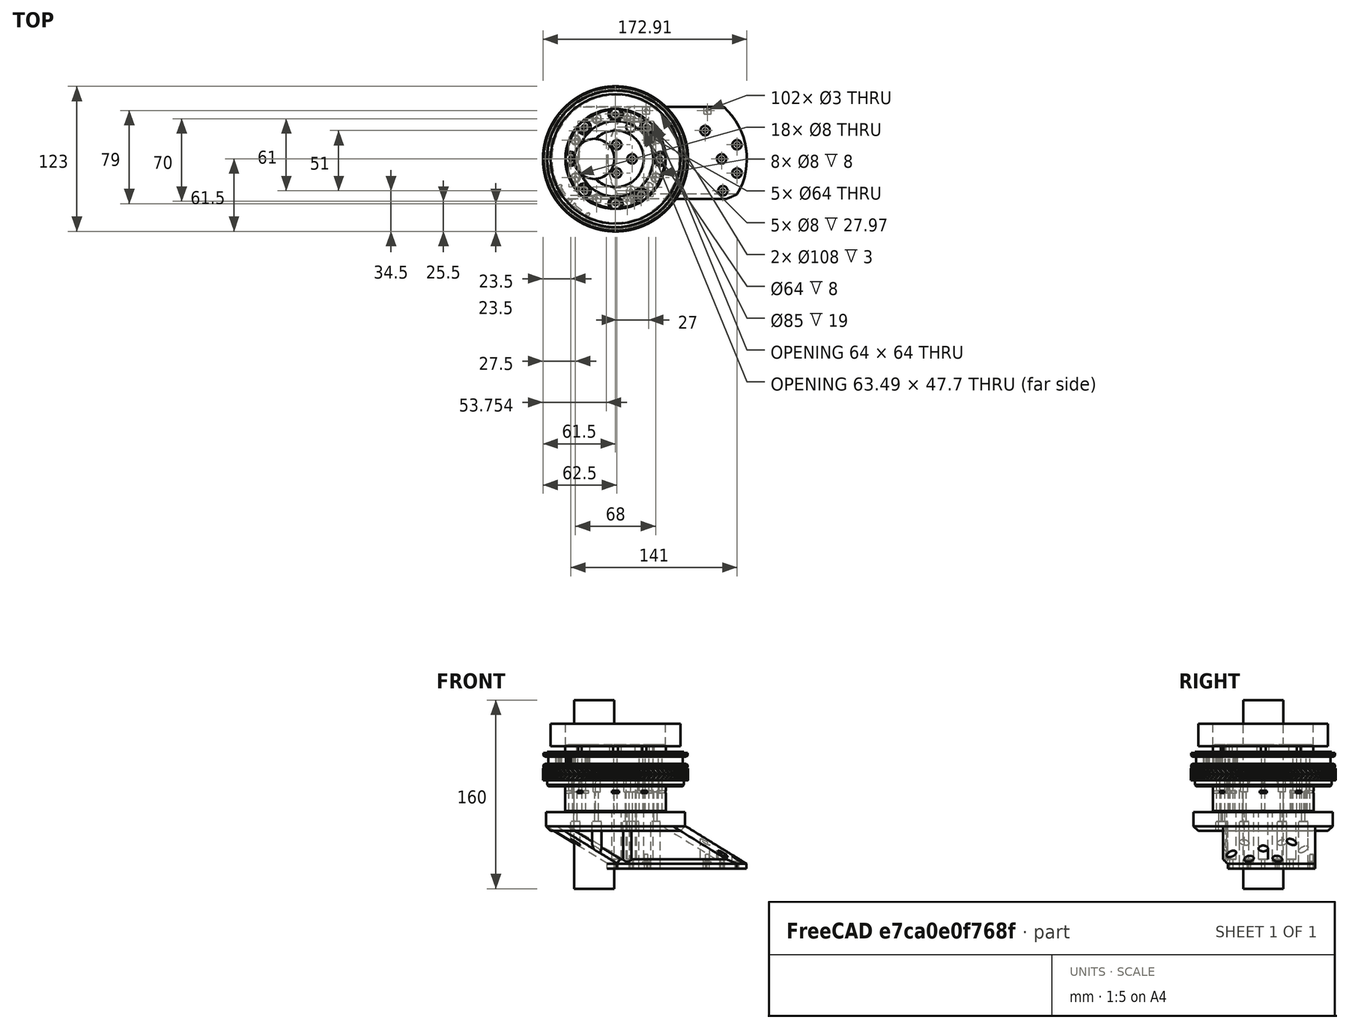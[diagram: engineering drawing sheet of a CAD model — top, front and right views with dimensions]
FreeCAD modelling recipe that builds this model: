
FCSTD DOCUMENT  (FreeCAD 0.19R24276 (Git))
Label: Base_inner-barrel_034
License: All rights reserved
LicenseURL: http://en.wikipedia.org/wiki/All_rights_reserved
objects: Part::Cylinder×576, Part::Box×255, Part::Compound×174, Part::Cut×167, Part::FeaturePython×49, Part::Chamfer×31, Part::Mirroring×10, Part::Fillet×9, Part::Common×3, Part::Torus×2, Mesh::Feature×2, Sketcher::SketchObject×1, Part::Extrusion×1
note: 1278 computed .brp shape members not serialized (recipe doc carries the construction recipe); baked Part::Feature solids carry a one-line shape summary decoded from their .brp

FEATURE [Part::Cylinder] Cylinder288  label="Válec288"
  Angle = 360
  AttacherType = Attacher::AttachEngine3D
  Height = 20
  Placement = pos=(0,-64.5,4.5) rot=(0,0,1;0rad)
  Radius = 3.5
FEATURE [Part::Cylinder] Cylinder371  label="Válec371"
  Angle = 360
  AttacherType = Attacher::AttachEngine3D
  Height = 50
  Placement = pos=(34,36,0) rot=(0,0,1;0rad)
  Radius = 1.5
FEATURE [Part::Cylinder] Cylinder372  label="Válec372"
  Angle = 360
  AttacherType = Attacher::AttachEngine3D
  Height = 50
  Placement = pos=(-34,-36,0) rot=(0,0,1;0rad)
  Radius = 1.5
FEATURE [Part::Torus] Torus  label="Anuloid"
  Angle1 = -180
  Angle2 = 180
  Angle3 = 360
  AttacherType = Attacher::AttachEngine3D
  Placement = pos=(0,0,24.5) rot=(0,0,1;0rad)
  Radius1 = 64.2
  Radius2 = 3.1
FEATURE [Part::FeaturePython] Tube019  # WARN: FeaturePython — macro-defined, semantics opaque (R4)
  AttacherType = Attacher::AttachEngine3D
  Height = 13
  InnerRadius = 38
  OuterRadius = 64
  Placement = pos=(0,0,18) rot=(0,0,1;0rad)
FEATURE [Part::Cut] Cut129
  Base = -> Tube019
  Tool = -> Torus
FEATURE [Part::Cut] Cut130
  Base = -> Cut129
  Tool = -> Cylinder288
FEATURE [Part::FeaturePython] Tube020  # WARN: FeaturePython — macro-defined, semantics opaque (R4)
  AttacherType = Attacher::AttachEngine3D
  Height = 1
  InnerRadius = 38
  OuterRadius = 58
  Placement = pos=(0,0,31) rot=(0,0,1;0rad)
FEATURE [Part::Box] Box149  label="Krychle149"
  AttacherType = Attacher::AttachEngine3D
  Height = 10
  Length = 6
  Placement = pos=(-37,33,40) rot=(0,0,1;0rad)
  Width = 6
FEATURE [Part::Cylinder] Cylinder378  label="Válec378"
  Angle = 360
  AttacherType = Attacher::AttachEngine3D
  Height = 50
  Placement = pos=(-51,6,0) rot=(0,0,1;0rad)
  Radius = 1.5
FEATURE [Part::Cylinder] Cylinder370  label="Válec370"
  Angle = 360
  AttacherType = Attacher::AttachEngine3D
  Height = 50
  Placement = pos=(-34,36,0) rot=(0,0,1;0rad)
  Radius = 1.5
FEATURE [Part::Cylinder] Cylinder373  label="Válec373"
  Angle = 360
  AttacherType = Attacher::AttachEngine3D
  Height = 50
  Placement = pos=(34,-36,0) rot=(0,0,1;0rad)
  Radius = 1.5
FEATURE [Part::Box] Box150  label="Krychle150"
  AttacherType = Attacher::AttachEngine3D
  Height = 10
  Length = 6
  Placement = pos=(31,-39,40) rot=(0,0,1;0rad)
  Width = 6
FEATURE [Part::Cylinder] Cylinder379  label="Válec379"
  Angle = 360
  AttacherType = Attacher::AttachEngine3D
  Height = 100
  Placement = pos=(51,-12,0) rot=(0,0,1;0rad)
  Radius = 1.5
FEATURE [Part::Cylinder] Cylinder377  label="Válec377"
  Angle = 360
  AttacherType = Attacher::AttachEngine3D
  Height = 50
  Placement = pos=(51,6,0) rot=(0,0,1;0rad)
  Radius = 1.5
FEATURE [Part::Cylinder] Cylinder375  label="Válec375"
  Angle = 360
  AttacherType = Attacher::AttachEngine3D
  Height = 50
  Placement = pos=(0,-50,0) rot=(0,0,1;0rad)
  Radius = 1.5
FEATURE [Part::Cylinder] Cylinder409  label="Válec409"
  Angle = 360
  AttacherType = Attacher::AttachEngine3D
  Height = 7
  Placement = pos=(51,6,50) rot=(0,0,1;0rad)
  Radius = 3
FEATURE [Part::Cylinder] Cylinder411  label="Válec411"
  Angle = 360
  AttacherType = Attacher::AttachEngine3D
  Height = 7
  Placement = pos=(51,-12,50) rot=(0,0,1;0rad)
  Radius = 3
FEATURE [Part::Cylinder] Cylinder406  label="Válec406"
  Angle = 360
  AttacherType = Attacher::AttachEngine3D
  Height = 7
  Placement = pos=(-51,-12,50) rot=(0,0,1;0rad)
  Radius = 3
FEATURE [Part::Cylinder] Cylinder405  label="Válec405"
  Angle = 360
  AttacherType = Attacher::AttachEngine3D
  Height = 7
  Placement = pos=(51,6,50) rot=(0,0,1;0rad)
  Radius = 3
FEATURE [Part::Cylinder] Cylinder404  label="Válec404"
  Angle = 360
  AttacherType = Attacher::AttachEngine3D
  Height = 7
  Placement = pos=(-51,6,50) rot=(0,0,1;0rad)
  Radius = 3
FEATURE [Part::Cylinder] Cylinder374  label="Válec374"
  Angle = 360
  AttacherType = Attacher::AttachEngine3D
  Height = 50
  Placement = pos=(0,50,0) rot=(0,0,1;0rad)
  Radius = 1.5
FEATURE [Part::Cylinder] Cylinder376  label="Válec376"
  Angle = 360
  AttacherType = Attacher::AttachEngine3D
  Height = 100
  Placement = pos=(-51,-12,0) rot=(0,0,1;0rad)
  Radius = 1.5
FEATURE [Part::Compound] Compound308
  Links = -> [Cylinder370,Cylinder371,Cylinder372,Cylinder373,Cylinder374,Cylinder375,Cylinder376,Cylinder377,Cylinder378,Cylinder379]
FEATURE [Part::Cut] Cut160
  Base = -> Cut130
  Tool = -> Compound308
FEATURE [Part::Cylinder] Cylinder408  label="Válec408"
  Angle = 360
  AttacherType = Attacher::AttachEngine3D
  Height = 7
  Placement = pos=(-51,-12,50) rot=(0,0,1;0rad)
  Radius = 3
FEATURE [Part::Box] Box153  label="Krychle153"
  AttacherType = Attacher::AttachEngine3D
  Height = 10
  Length = 6
  Placement = pos=(-37,33,40) rot=(0,0,1;0rad)
  Width = 6
FEATURE [Part::Box] Box154  label="Krychle154"
  AttacherType = Attacher::AttachEngine3D
  Height = 10
  Length = 6
  Placement = pos=(-37,-39,40) rot=(0,0,1;0rad)
  Width = 6
FEATURE [Part::Box] Box155  label="Krychle155"
  AttacherType = Attacher::AttachEngine3D
  Height = 10
  Length = 6
  Placement = pos=(31,33,40) rot=(0,0,1;0rad)
  Width = 6
FEATURE [Part::Cylinder] Cylinder410  label="Válec410"
  Angle = 360
  AttacherType = Attacher::AttachEngine3D
  Height = 7
  Placement = pos=(-51,6,50) rot=(0,0,1;0rad)
  Radius = 3
FEATURE [Part::Compound] Compound313
  Links = -> [Cylinder408,Cylinder411,Cylinder409,Cylinder410]
  Placement = pos=(0,0,-25) rot=(0,0,1;0rad)
FEATURE [Part::Cut] Cut162
  Base = -> Cut160
  Tool = -> Compound313
FEATURE [Part::Box] Box158  label="Krychle158"
  AttacherType = Attacher::AttachEngine3D
  Height = 2
  Length = 6
  Placement = pos=(43.284,-12.6687,25) rot=(0,0,1;1.35263rad)
  Width = 8
FEATURE [Part::Box] Box145  label="Krychle145"
  AttacherType = Attacher::AttachEngine3D
  Height = 10
  Length = 6
  Placement = pos=(-3,47,40) rot=(0,0,1;0rad)
  Width = 6
FEATURE [Part::Box] Box151  label="Krychle151"
  AttacherType = Attacher::AttachEngine3D
  Height = 10
  Length = 6
  Placement = pos=(-3,-53,40) rot=(0,0,1;0rad)
  Width = 6
FEATURE [Part::Box] Box159  label="Krychle159"
  AttacherType = Attacher::AttachEngine3D
  Height = 2
  Length = 6
  Placement = pos=(42.7226,14.4491,25) rot=(0,0,1;1.96349rad)
  Width = 8
FEATURE [Part::Box] Box146  label="Krychle146"
  AttacherType = Attacher::AttachEngine3D
  Height = 10
  Length = 6
  Placement = pos=(-3,-53,40) rot=(0,0,1;0rad)
  Width = 6
FEATURE [Part::Box] Box148  label="Krychle148"
  AttacherType = Attacher::AttachEngine3D
  Height = 10
  Length = 6
  Placement = pos=(31,33,40) rot=(0,0,1;0rad)
  Width = 6
FEATURE [Part::Box] Box157  label="Krychle157"
  AttacherType = Attacher::AttachEngine3D
  Height = 2
  Length = 6
  Placement = pos=(14.4491,-42.7226,25) rot=(0,0,1;0.392699rad)
  Width = 8
FEATURE [Part::Box] Box162  label="Krychle162"
  AttacherType = Attacher::AttachEngine3D
  Height = 2
  Length = 6
  Placement = pos=(-40.4265,19.9924,25) rot=(0,0,-1;1.96349rad)
  Width = 8
FEATURE [Part::Box] Box147  label="Krychle147"
  AttacherType = Attacher::AttachEngine3D
  Height = 10
  Length = 6
  Placement = pos=(-37,-39,40) rot=(0,0,1;0rad)
  Width = 6
FEATURE [Part::Compound] Compound315
  Links = -> [Box145,Box147,Box146,Box148,Box149,Box150]
  Placement = pos=(0,0,-18) rot=(0,0,1;0rad)
FEATURE [Part::Cylinder] Cylinder407  label="Válec407"
  Angle = 360
  AttacherType = Attacher::AttachEngine3D
  Height = 7
  Placement = pos=(51,-12,50) rot=(0,0,1;0rad)
  Radius = 3
FEATURE [Part::Compound] Compound312
  Links = -> [Cylinder406,Cylinder407,Cylinder405,Cylinder404]
  Placement = pos=(0,0,-25) rot=(0,0,1;0rad)
FEATURE [Part::Cut] Cut161
  Base = -> Tube020
  Tool = -> Compound312
FEATURE [Part::Box] Box156  label="Krychle156"
  AttacherType = Attacher::AttachEngine3D
  Height = 10
  Length = 6
  Placement = pos=(31,-39,40) rot=(0,0,1;0rad)
  Width = 6
FEATURE [Part::Box] Box152  label="Krychle152"
  AttacherType = Attacher::AttachEngine3D
  Height = 10
  Length = 6
  Placement = pos=(-3,47,40) rot=(0,0,1;0rad)
  Width = 6
FEATURE [Part::Compound] Compound316
  Links = -> [Box152,Box154,Box151,Box155,Box153,Box156]
  Placement = pos=(0,0,-18) rot=(0,0,1;0rad)
FEATURE [Part::Cut] Cut163
  Base = -> Cut161
  Tool = -> Compound316
FEATURE [Part::Cut] Cut164
  Base = -> Cut162
  Tool = -> Compound315
FEATURE [Part::Box] Box160  label="Krychle160"
  AttacherType = Attacher::AttachEngine3D
  Height = 2
  Length = 6
  Placement = pos=(19.9924,40.4265,25) rot=(0,0,1;2.74889rad)
  Width = 8
FEATURE [Part::Box] Box163  label="Krychle163"
  AttacherType = Attacher::AttachEngine3D
  Height = 2
  Length = 6
  Placement = pos=(-44.5826,-6.81089,25) rot=(0,0,-1;1.35263rad)
  Width = 8
FEATURE [Part::Cylinder] Cylinder444  label="Válec444"
  Angle = 360
  AttacherType = Attacher::AttachEngine3D
  Height = 100
  Placement = pos=(16.0727,-38.8029,0) rot=(0,0,1;0.785398rad)
  Radius = 1.5
FEATURE [Part::Cylinder] Cylinder445  label="Válec445"
  Angle = 360
  AttacherType = Attacher::AttachEngine3D
  Height = 100
  Placement = pos=(41.0044,-9.09046,0) rot=(0,0,1;1.74533rad)
  Radius = 1.5
FEATURE [Part::Cylinder] Cylinder446  label="Válec446"
  Angle = 360
  AttacherType = Attacher::AttachEngine3D
  Height = 100
  Placement = pos=(38.8029,16.0727,0) rot=(0,0,1;2.35619rad)
  Radius = 1.5
FEATURE [Part::Box] Box164  label="Krychle164"
  AttacherType = Attacher::AttachEngine3D
  Height = 2
  Length = 6
  Placement = pos=(-19.9924,-40.4265,25) rot=(0,0,-1;0.392699rad)
  Width = 8
FEATURE [Part::Cylinder] Cylinder447  label="Válec447"
  Angle = 360
  AttacherType = Attacher::AttachEngine3D
  Height = 100
  Placement = pos=(16.0727,38.8029,0) rot=(0,0,1;3.14159rad)
  Radius = 1.5
FEATURE [Part::Cylinder] Cylinder449  label="Válec449"
  Angle = 360
  AttacherType = Attacher::AttachEngine3D
  Height = 100
  Placement = pos=(-38.8029,16.0727,0) rot=(0,0,-1;1.5708rad)
  Radius = 1.5
FEATURE [Part::Cylinder] Cylinder450  label="Válec450"
  Angle = 360
  AttacherType = Attacher::AttachEngine3D
  Height = 100
  Placement = pos=(-41.0044,-9.09046,0) rot=(0,0,-1;0.959931rad)
  Radius = 1.5
FEATURE [Part::Cylinder] Cylinder471  label="Válec471"
  Angle = 360
  AttacherType = Attacher::AttachEngine3D
  Height = 100
  Placement = pos=(16.0727,38.8029,0) rot=(0,0,1;3.14159rad)
  Radius = 1.5
FEATURE [Part::Cylinder] Cylinder468  label="Válec468"
  Angle = 360
  AttacherType = Attacher::AttachEngine3D
  Height = 100
  Placement = pos=(16.0727,-38.8029,0) rot=(0,0,1;0.785398rad)
  Radius = 1.5
FEATURE [Part::Cylinder] Cylinder473  label="Válec473"
  Angle = 360
  AttacherType = Attacher::AttachEngine3D
  Height = 100
  Placement = pos=(-38.8029,16.0727,0) rot=(0,0,-1;1.5708rad)
  Radius = 1.5
FEATURE [Part::Cylinder] Cylinder474  label="Válec474"
  Angle = 360
  AttacherType = Attacher::AttachEngine3D
  Height = 100
  Placement = pos=(-41.0044,-9.09046,0) rot=(0,0,-1;0.959931rad)
  Radius = 1.5
FEATURE [Part::Cylinder] Cylinder448  label="Válec448"
  Angle = 360
  AttacherType = Attacher::AttachEngine3D
  Height = 100
  Placement = pos=(-16.0727,38.8029,0) rot=(0,0,1;3.92699rad)
  Radius = 1.5
FEATURE [Part::Cylinder] Cylinder451  label="Válec451"
  Angle = 360
  AttacherType = Attacher::AttachEngine3D
  Height = 100
  Placement = pos=(-16.0727,-38.8029,0) rot=(0,0,1;0rad)
  Radius = 1.5
FEATURE [Part::Compound] Compound325
  Links = -> [Cylinder444,Cylinder445,Cylinder446,Cylinder447,Cylinder448,Cylinder449,Cylinder450,Cylinder451]
FEATURE [Part::Cut] Cut173
  Base = -> Cut163
  Tool = -> Compound325
FEATURE [Part::Box] Box161  label="Krychle161"
  AttacherType = Attacher::AttachEngine3D
  Height = 2
  Length = 6
  Placement = pos=(-14.4491,42.7226,25) rot=(0,0,1;3.53429rad)
  Width = 8
FEATURE [Part::Compound] Compound322
  Links = -> [Box157,Box158,Box159,Box160,Box161,Box162,Box163,Box164]
FEATURE [Part::Cylinder] Cylinder469  label="Válec469"
  Angle = 360
  AttacherType = Attacher::AttachEngine3D
  Height = 100
  Placement = pos=(41.0044,-9.09046,0) rot=(0,0,1;1.74533rad)
  Radius = 1.5
FEATURE [Part::Cylinder] Cylinder529  label="Válec529"
  Angle = 360
  AttacherType = Attacher::AttachEngine3D
  Height = 100
  Placement = pos=(39,-21,0) rot=(0,0,1;0rad)
  Radius = 1.5
FEATURE [Part::Cylinder] Cylinder470  label="Válec470"
  Angle = 360
  AttacherType = Attacher::AttachEngine3D
  Height = 100
  Placement = pos=(38.8029,16.0727,0) rot=(0,0,1;2.35619rad)
  Radius = 1.5
FEATURE [Part::Cylinder] Cylinder472  label="Válec472"
  Angle = 360
  AttacherType = Attacher::AttachEngine3D
  Height = 100
  Placement = pos=(-16.0727,38.8029,0) rot=(0,0,1;3.92699rad)
  Radius = 1.5
FEATURE [Part::Cylinder] Cylinder475  label="Válec475"
  Angle = 360
  AttacherType = Attacher::AttachEngine3D
  Height = 100
  Placement = pos=(-16.0727,-38.8029,0) rot=(0,0,1;0rad)
  Radius = 1.5
FEATURE [Part::Compound] Compound328
  Links = -> [Cylinder468,Cylinder469,Cylinder470,Cylinder471,Cylinder472,Cylinder473,Cylinder474,Cylinder475]
  Placement = pos=(0,0,20) rot=(0,0,1;0rad)
FEATURE [Part::Cut] Cut174
  Base = -> Cut164
  Tool = -> Compound328
FEATURE [Part::Cut] Cut175
  Base = -> Cut174
  Tool = -> Compound322
FEATURE [Part::Cylinder] Cylinder533  label="Válec533"
  Angle = 360
  AttacherType = Attacher::AttachEngine3D
  Height = 7
  Placement = pos=(39,-21,50) rot=(0,0,1;0rad)
  Radius = 3
FEATURE [Part::Cylinder] Cylinder528  label="Válec528"
  Angle = 360
  AttacherType = Attacher::AttachEngine3D
  Height = 100
  Placement = pos=(-39,-21,0) rot=(0,0,1;0rad)
  Radius = 1.5
FEATURE [Part::Cylinder] Cylinder532  label="Válec532"
  Angle = 360
  AttacherType = Attacher::AttachEngine3D
  Height = 7
  Placement = pos=(-39,-21,50) rot=(0,0,1;0rad)
  Radius = 3
FEATURE [Part::Cylinder] Cylinder530  label="Válec530"
  Angle = 360
  AttacherType = Attacher::AttachEngine3D
  Height = 7
  Placement = pos=(-39,-21,50) rot=(0,0,1;0rad)
  Radius = 3
FEATURE [Part::Cylinder] Cylinder531  label="Válec531"
  Angle = 360
  AttacherType = Attacher::AttachEngine3D
  Height = 7
  Placement = pos=(39,-21,50) rot=(0,0,1;0rad)
  Radius = 3
FEATURE [Part::Compound] Compound
  Links = -> [Cylinder528,Cylinder529]
FEATURE [Part::Compound] Compound337
  Links = -> [Cylinder530,Cylinder531]
  Placement = pos=(0,0,-25) rot=(0,0,1;0rad)
FEATURE [Part::Cut] Cut
  Base = -> Cut173
  Tool = -> Compound337
FEATURE [Part::Compound] Compound338
  Links = -> [Cylinder532,Cylinder533]
  Placement = pos=(0,0,-25) rot=(0,0,1;0rad)
FEATURE [Part::Cut] Cut176
  Base = -> Cut175
  Tool = -> Compound338
FEATURE [Part::Cut] Cut177
  Base = -> Cut176
  Tool = -> Compound
FEATURE [Part::Compound] Compound339  label="bazovina-part-C_loziskovina"
  Links = -> [Cut,Cut177]
FEATURE [Part::Cylinder] Cylinder476  label="Válec476"
  Angle = 360
  AttacherType = Attacher::AttachEngine3D
  Height = 20
  Placement = pos=(0,-63.8,4.5) rot=(0,0,1;0rad)
  Radius = 3.5
FEATURE [Part::Box] Box176  label="Krychle176"
  AttacherType = Attacher::AttachEngine3D
  Height = 15
  Length = 148
  Placement = pos=(-74,0,16) rot=(0,0,1;0rad)
  Width = 48
FEATURE [Part::Cylinder] Cylinder482  label="Válec482"
  Angle = 360
  AttacherType = Attacher::AttachEngine3D
  Height = 15
  Placement = pos=(0,0,16) rot=(0,0,1;0rad)
  Radius = 74
FEATURE [Part::FeaturePython] Tube024  # WARN: FeaturePython — macro-defined, semantics opaque (R4)
  AttacherType = Attacher::AttachEngine3D
  Height = 15
  InnerRadius = 64.5
  OuterRadius = 74
  Placement = pos=(0,0,16) rot=(0,0,1;0rad)
FEATURE [Part::Torus] Torus001  label="Anuloid001"
  Angle1 = -180
  Angle2 = 180
  Angle3 = 360
  AttacherType = Attacher::AttachEngine3D
  Placement = pos=(0,0,24.5) rot=(0,0,1;0rad)
  Radius1 = 64.2
  Radius2 = 3.1
FEATURE [Part::Cut] Cut178
  Base = -> Tube024
  Tool = -> Torus001
FEATURE [Part::Cut] Cut179
  Base = -> Cut178
  Tool = -> Cylinder476
FEATURE [Part::Cut] Cut185
  Base = -> Box176
  Tool = -> Cylinder482
FEATURE [Part::Cylinder] Cylinder485  label="Válec485"
  Angle = 360
  AttacherType = Attacher::AttachEngine3D
  Height = 15
  Placement = pos=(0,0,16) rot=(0,0,1;0rad)
  Radius = 74
FEATURE [Part::Cut] Cut188
  Base = -> Cut185
  Tool = -> Cylinder485
FEATURE [Part::Compound] Compound341
  Links = -> [Cut188,Cut179]
FEATURE [Part::Cylinder] Cylinder509  label="Válec509"
  Angle = 360
  AttacherType = Attacher::AttachEngine3D
  Height = 50
  Placement = pos=(71,80,24) rot=(1,0,0;1.5708rad)
  Radius = 1.5
FEATURE [Part::Box] Box208  label="Krychle208"
  AttacherType = Attacher::AttachEngine3D
  Height = 6
  Length = 8
  Placement = pos=(67,38,21) rot=(0,0,1;0rad)
  Width = 2
FEATURE [Part::Cylinder] Cylinder510  label="Válec510"
  Angle = 360
  AttacherType = Attacher::AttachEngine3D
  Height = 50
  Placement = pos=(-71,80,24) rot=(1,0,0;1.5708rad)
  Radius = 1.5
FEATURE [Part::Compound] Compound342
  Links = -> [Cylinder509,Cylinder510]
FEATURE [Part::Box] Box209  label="Krychle209"
  AttacherType = Attacher::AttachEngine3D
  Height = 6
  Length = 8
  Placement = pos=(-75,38,21) rot=(0,0,1;0rad)
  Width = 2
FEATURE [Part::Compound] Compound340
  Links = -> [Box208,Box209]
FEATURE [Part::Cut] Cut201
  Base = -> Compound341
  Tool = -> Compound340
FEATURE [Part::Cut] Cut202
  Base = -> Cut201
  Tool = -> Compound342
FEATURE [Part::Box] Box179  label="Krychle179"
  AttacherType = Attacher::AttachEngine3D
  Height = 47
  Length = 56
  Placement = pos=(-28,0,29) rot=(0,0,1;0rad)
  Width = 200
FEATURE [Part::Cut] Cut203
  Base = -> Cut202
  Tool = -> Box179
FEATURE [Part::Cylinder] Cylinder982  label="Válec982"
  Angle = 360
  AttacherType = Attacher::AttachEngine3D
  Height = 60
  Placement = pos=(-71,2.7e-14,0) rot=(0,0,-1;1.5708rad)
  Radius = 1.5
FEATURE [Part::Cylinder] Cylinder978  label="Válec978"
  Angle = 360
  AttacherType = Attacher::AttachEngine3D
  Height = 60
  Placement = pos=(35.5,61.4878,0) rot=(0,0,1;2.61799rad)
  Radius = 1.5
FEATURE [Part::Cylinder] Cylinder983  label="Válec983"
  Angle = 360
  AttacherType = Attacher::AttachEngine3D
  Height = 60
  Placement = pos=(-61.4878,-35.5,0) rot=(0,0,-1;1.0472rad)
  Radius = 1.5
FEATURE [Part::Cylinder] Cylinder977  label="Válec977"
  Angle = 360
  AttacherType = Attacher::AttachEngine3D
  Height = 60
  Placement = pos=(61.4878,35.5,0) rot=(0,0,1;2.0944rad)
  Radius = 1.5
FEATURE [Part::Cylinder] Cylinder984  label="Válec984"
  Angle = 360
  AttacherType = Attacher::AttachEngine3D
  Height = 60
  Placement = pos=(-35.5,-61.4878,0) rot=(0,0,-1;0.523599rad)
  Radius = 1.5
FEATURE [Part::Cylinder] Cylinder974  label="Válec974"
  Angle = 360
  AttacherType = Attacher::AttachEngine3D
  Height = 60
  Placement = pos=(35.5,-61.4878,0) rot=(0,0,1;0.523599rad)
  Radius = 1.5
FEATURE [Part::Cylinder] Cylinder976  label="Válec976"
  Angle = 360
  AttacherType = Attacher::AttachEngine3D
  Height = 60
  Placement = pos=(71,-1.8e-14,0) rot=(0,0,1;1.5708rad)
  Radius = 1.5
FEATURE [Part::Cylinder] Cylinder973  label="Válec973"
  Angle = 360
  AttacherType = Attacher::AttachEngine3D
  Height = 60
  Placement = pos=(0,-71,0) rot=(0,0,1;0rad)
  Radius = 1.5
FEATURE [Part::Cylinder] Cylinder980  label="Válec980"
  Angle = 360
  AttacherType = Attacher::AttachEngine3D
  Height = 60
  Placement = pos=(-35.5,61.4878,0) rot=(0,0,1;3.66519rad)
  Radius = 1.5
FEATURE [Part::Cylinder] Cylinder981  label="Válec981"
  Angle = 360
  AttacherType = Attacher::AttachEngine3D
  Height = 60
  Placement = pos=(-61.4878,35.5,0) rot=(0,0,1;4.18879rad)
  Radius = 1.5
FEATURE [Part::Cylinder] Cylinder975  label="Válec975"
  Angle = 360
  AttacherType = Attacher::AttachEngine3D
  Height = 60
  Placement = pos=(61.4878,-35.5,0) rot=(0,0,1;1.0472rad)
  Radius = 1.5
FEATURE [Part::Compound] Compound525
  Links = -> [Cylinder973,Cylinder974,Cylinder975,Cylinder976,Cylinder977,Cylinder978,Cylinder980,Cylinder981,Cylinder982,Cylinder983,Cylinder984]
FEATURE [Part::Cut] Cut204  label="bazovina_part-E_lozo-okruh-novo"
  Base = -> Cut203
  Tool = -> Compound525
FEATURE [Part::FeaturePython] wormgear022  # WARN: FeaturePython — macro-defined, semantics opaque (R4)
  AttacherType = Attacher::AttachEngine3D
  Placement = pos=(0,0,100) rot=(0,0,1;0rad)
  beta = 33.6901
  clearance = 0.25
  diameter = 120
  head = 0
  height = 5
  module = 1
  pressure_angle = 20
  reverse_pitch = true
  teeth = 80
  version = 0.0.3
FEATURE [Part::FeaturePython] wormgear023  # WARN: FeaturePython — macro-defined, semantics opaque (R4)
  AttacherType = Attacher::AttachEngine3D
  Placement = pos=(0,0,95) rot=(0,0,1;0.032289rad)
  beta = 33.6901
  clearance = 0.25
  diameter = 120
  head = 0
  height = 5
  module = 1
  pressure_angle = 20
  reverse_pitch = false
  teeth = 80
  version = 0.0.3
FEATURE [Part::Cylinder] Cylinder289  label="Válec289"
  Angle = 360
  AttacherType = Attacher::AttachEngine3D
  Height = 20
  Placement = pos=(0,0,91) rot=(0,0,1;0rad)
  Radius = 38
FEATURE [Part::Cylinder] Cylinder290  label="Válec290"
  Angle = 360
  AttacherType = Attacher::AttachEngine3D
  Height = 20
  Placement = pos=(0,0,91) rot=(0,0,1;0rad)
  Radius = 38
FEATURE [Part::Cylinder] Cylinder461  label="Válec461"
  Angle = 360
  AttacherType = Attacher::AttachEngine3D
  Height = 100
  Placement = pos=(38.8029,-16.0727,0) rot=(0,0,1;1.5708rad)
  Radius = 1.5
FEATURE [Part::Cut] Cut128
  Base = -> wormgear022
  Placement = pos=(0,0,-63) rot=(0,0,1;0rad)
  Tool = -> Cylinder289
FEATURE [Part::Cut] Cut127
  Base = -> wormgear023
  Placement = pos=(0,0,-63) rot=(0,0,1;0rad)
  Tool = -> Cylinder290
FEATURE [Part::Cylinder] Cylinder452  label="Válec452"
  Angle = 360
  AttacherType = Attacher::AttachEngine3D
  Height = 100
  Placement = pos=(9.09046,-41.0044,0) rot=(0,0,1;0.610865rad)
  Radius = 1.5
FEATURE [Part::Cylinder] Cylinder456  label="Válec456"
  Angle = 360
  AttacherType = Attacher::AttachEngine3D
  Height = 100
  Placement = pos=(-16.0727,38.8029,0) rot=(0,0,1;3.92699rad)
  Radius = 1.5
FEATURE [Part::Cylinder] Cylinder457  label="Válec457"
  Angle = 360
  AttacherType = Attacher::AttachEngine3D
  Height = 100
  Placement = pos=(-38.8029,16.0727,0) rot=(0,0,-1;1.5708rad)
  Radius = 1.5
FEATURE [Part::Cylinder] Cylinder453  label="Válec453"
  Angle = 360
  AttacherType = Attacher::AttachEngine3D
  Height = 100
  Placement = pos=(38.8029,-16.0727,0) rot=(0,0,1;1.5708rad)
  Radius = 1.5
FEATURE [Part::Cylinder] Cylinder454  label="Válec454"
  Angle = 360
  AttacherType = Attacher::AttachEngine3D
  Height = 100
  Placement = pos=(38.8029,16.0727,0) rot=(0,0,1;2.35619rad)
  Radius = 1.5
FEATURE [Part::Cylinder] Cylinder455  label="Válec455"
  Angle = 360
  AttacherType = Attacher::AttachEngine3D
  Height = 100
  Placement = pos=(9.09046,41.0044,0) rot=(0,0,1;3.31613rad)
  Radius = 1.5
FEATURE [Part::Cylinder] Cylinder459  label="Válec459"
  Angle = 360
  AttacherType = Attacher::AttachEngine3D
  Height = 100
  Placement = pos=(-16.0727,-38.8029,0) rot=(0,0,1;0rad)
  Radius = 1.5
FEATURE [Part::Cylinder] Cylinder458  label="Válec458"
  Angle = 360
  AttacherType = Attacher::AttachEngine3D
  Height = 100
  Placement = pos=(-38.8029,-16.0727,0) rot=(0,0,-1;0.785398rad)
  Radius = 1.5
FEATURE [Part::Compound] Compound326
  Links = -> [Cylinder452,Cylinder453,Cylinder454,Cylinder455,Cylinder456,Cylinder457,Cylinder458,Cylinder459]
FEATURE [Part::Cut] Cut171
  Base = -> Cut128
  Tool = -> Compound326
FEATURE [Part::Cylinder] Cylinder466  label="Válec466"
  Angle = 360
  AttacherType = Attacher::AttachEngine3D
  Height = 100
  Placement = pos=(-38.8029,-16.0727,0) rot=(0,0,-1;0.785398rad)
  Radius = 1.5
FEATURE [Part::Cylinder] Cylinder465  label="Válec465"
  Angle = 360
  AttacherType = Attacher::AttachEngine3D
  Height = 100
  Placement = pos=(-38.8029,16.0727,0) rot=(0,0,-1;1.5708rad)
  Radius = 1.5
FEATURE [Part::Cylinder] Cylinder462  label="Válec462"
  Angle = 360
  AttacherType = Attacher::AttachEngine3D
  Height = 100
  Placement = pos=(38.8029,16.0727,0) rot=(0,0,1;2.35619rad)
  Radius = 1.5
FEATURE [Part::Cylinder] Cylinder460  label="Válec460"
  Angle = 360
  AttacherType = Attacher::AttachEngine3D
  Height = 100
  Placement = pos=(9.09046,-41.0044,0) rot=(0,0,1;0.610865rad)
  Radius = 1.5
FEATURE [Part::Cylinder] Cylinder467  label="Válec467"
  Angle = 360
  AttacherType = Attacher::AttachEngine3D
  Height = 100
  Placement = pos=(-16.0727,-38.8029,0) rot=(0,0,1;0rad)
  Radius = 1.5
FEATURE [Part::Cylinder] Cylinder756  label="Válec756"
  Angle = 360
  AttacherType = Attacher::AttachEngine3D
  Height = 100
  Placement = pos=(-16.0727,-38.8029,0) rot=(0,0,1;0rad)
  Radius = 1.5
FEATURE [Part::Cylinder] Cylinder463  label="Válec463"
  Angle = 360
  AttacherType = Attacher::AttachEngine3D
  Height = 100
  Placement = pos=(9.09046,41.0044,0) rot=(0,0,1;3.31613rad)
  Radius = 1.5
FEATURE [Part::Cylinder] Cylinder464  label="Válec464"
  Angle = 360
  AttacherType = Attacher::AttachEngine3D
  Height = 100
  Placement = pos=(-16.0727,38.8029,0) rot=(0,0,1;3.92699rad)
  Radius = 1.5
FEATURE [Part::Compound] Compound327
  Links = -> [Cylinder460,Cylinder461,Cylinder462,Cylinder463,Cylinder464,Cylinder465,Cylinder466,Cylinder467]
FEATURE [Part::Cut] Cut172
  Base = -> Cut127
  Tool = -> Compound327
FEATURE [Part::FeaturePython] Tube079  # WARN: FeaturePython — macro-defined, semantics opaque (R4)
  AttacherType = Attacher::AttachEngine3D
  Height = 1
  InnerRadius = 38
  OuterRadius = 58
  Placement = pos=(0,0,42) rot=(0,0,1;0rad)
FEATURE [Part::Compound] Compound335  label="bazovina-part-D_ozubo2"
  Links = -> [Cut171,Cut172]
FEATURE [Part::Cylinder] Cylinder758  label="Válec758"
  Angle = 360
  AttacherType = Attacher::AttachEngine3D
  Height = 100
  Placement = pos=(-41.0044,-9.09046,0) rot=(0,0,-1;0.959931rad)
  Radius = 1.5
FEATURE [Part::Cylinder] Cylinder759  label="Válec759"
  Angle = 360
  AttacherType = Attacher::AttachEngine3D
  Height = 100
  Placement = pos=(16.0727,38.8029,0) rot=(0,0,1;3.14159rad)
  Radius = 1.5
FEATURE [Part::Cylinder] Cylinder755  label="Válec755"
  Angle = 360
  AttacherType = Attacher::AttachEngine3D
  Height = 100
  Placement = pos=(38.8029,16.0727,0) rot=(0,0,1;2.35619rad)
  Radius = 1.5
FEATURE [Part::Cylinder] Cylinder760  label="Válec760"
  Angle = 360
  AttacherType = Attacher::AttachEngine3D
  Height = 100
  Placement = pos=(16.0727,-38.8029,0) rot=(0,0,1;0.785398rad)
  Radius = 1.5
FEATURE [Part::Cylinder] Cylinder761  label="Válec761"
  Angle = 360
  AttacherType = Attacher::AttachEngine3D
  Height = 100
  Placement = pos=(-16.0727,38.8029,0) rot=(0,0,1;3.92699rad)
  Radius = 1.5
FEATURE [Part::Cylinder] Cylinder757  label="Válec757"
  Angle = 360
  AttacherType = Attacher::AttachEngine3D
  Height = 100
  Placement = pos=(41.0044,-9.09046,0) rot=(0,0,1;1.74533rad)
  Radius = 1.5
FEATURE [Part::Cylinder] Cylinder754  label="Válec754"
  Angle = 360
  AttacherType = Attacher::AttachEngine3D
  Height = 100
  Placement = pos=(-38.8029,16.0727,0) rot=(0,0,-1;1.5708rad)
  Radius = 1.5
FEATURE [Part::Compound] Compound709
  Links = -> [Cylinder760,Cylinder757,Cylinder755,Cylinder759,Cylinder761,Cylinder754,Cylinder758,Cylinder756]
FEATURE [Part::Cut] Cut325  label="bazovina_part-F_washer001"
  Base = -> Tube079
  Placement = pos=(0,0,0) rot=(0,0,1;1.5708rad)
  Tool = -> Compound709
FEATURE [Part::Compound] Compound710  label="bazovina_part-D_ozubo-washer"
  Links = -> [Compound335,Cut325]
FEATURE [Part::Cylinder] Cylinder746  label="Válec746"
  Angle = 360
  AttacherType = Attacher::AttachEngine3D
  Height = 20
  Placement = pos=(-38.8029,16.0727,0) rot=(0,0,-1;1.5708rad)
  Radius = 8
FEATURE [Part::Cylinder] Cylinder749  label="Válec749"
  Angle = 360
  AttacherType = Attacher::AttachEngine3D
  Height = 20
  Placement = pos=(41.0044,-9.09046,0) rot=(0,0,1;1.74533rad)
  Radius = 8
FEATURE [Part::Cylinder] Cylinder751  label="Válec751"
  Angle = 360
  AttacherType = Attacher::AttachEngine3D
  Height = 20
  Placement = pos=(16.0727,38.8029,0) rot=(0,0,1;3.14159rad)
  Radius = 8
FEATURE [Part::Cylinder] Cylinder747  label="Válec747"
  Angle = 360
  AttacherType = Attacher::AttachEngine3D
  Height = 20
  Placement = pos=(38.8029,16.0727,0) rot=(0,0,1;2.35619rad)
  Radius = 8
FEATURE [Part::Cylinder] Cylinder748  label="Válec748"
  Angle = 360
  AttacherType = Attacher::AttachEngine3D
  Height = 20
  Placement = pos=(-16.0727,-38.8029,0) rot=(0,0,1;0rad)
  Radius = 8
FEATURE [Part::Cylinder] Cylinder750  label="Válec750"
  Angle = 360
  AttacherType = Attacher::AttachEngine3D
  Height = 20
  Placement = pos=(-41.0044,-9.09046,0) rot=(0,0,-1;0.959931rad)
  Radius = 8
FEATURE [Part::Cylinder] Cylinder752  label="Válec752"
  Angle = 360
  AttacherType = Attacher::AttachEngine3D
  Height = 20
  Placement = pos=(16.0727,-38.8029,0) rot=(0,0,1;0.785398rad)
  Radius = 8
FEATURE [Part::Cylinder] Cylinder762  label="Válec762"
  Angle = 360
  AttacherType = Attacher::AttachEngine3D
  Height = 20
  Placement = pos=(-16.0727,38.8029,0) rot=(0,0,1;3.92699rad)
  Radius = 8
FEATURE [Part::Cylinder] Cylinder764  label="Válec764"
  Angle = 360
  AttacherType = Attacher::AttachEngine3D
  Height = 20
  Placement = pos=(-41.0044,-9.09046,0) rot=(0,0,-1;0.959931rad)
  Radius = 8
FEATURE [Part::Cylinder] Cylinder766  label="Válec766"
  Angle = 360
  AttacherType = Attacher::AttachEngine3D
  Height = 20
  Placement = pos=(41.0044,-9.09046,0) rot=(0,0,1;1.74533rad)
  Radius = 8
FEATURE [Part::Cylinder] Cylinder763  label="Válec763"
  Angle = 360
  AttacherType = Attacher::AttachEngine3D
  Height = 20
  Placement = pos=(-16.0727,-38.8029,0) rot=(0,0,1;0rad)
  Radius = 8
FEATURE [Part::Cylinder] Cylinder753  label="Válec753"
  Angle = 360
  AttacherType = Attacher::AttachEngine3D
  Height = 20
  Placement = pos=(-16.0727,38.8029,0) rot=(0,0,1;3.92699rad)
  Radius = 8
FEATURE [Part::Compound] Compound708
  Links = -> [Cylinder752,Cylinder749,Cylinder747,Cylinder751,Cylinder753,Cylinder746,Cylinder750,Cylinder748]
  Placement = pos=(0,0,56) rot=(0,0,1;0rad)
FEATURE [Part::Cylinder] Cylinder765  label="Válec765"
  Angle = 360
  AttacherType = Attacher::AttachEngine3D
  Height = 20
  Placement = pos=(38.8029,16.0727,0) rot=(0,0,1;2.35619rad)
  Radius = 8
FEATURE [Part::Cylinder] Cylinder767  label="Válec767"
  Angle = 360
  AttacherType = Attacher::AttachEngine3D
  Height = 20
  Placement = pos=(16.0727,38.8029,0) rot=(0,0,1;3.14159rad)
  Radius = 8
FEATURE [Part::Cylinder] Cylinder769  label="Válec769"
  Angle = 360
  AttacherType = Attacher::AttachEngine3D
  Height = 20
  Placement = pos=(-38.8029,16.0727,0) rot=(0,0,-1;1.5708rad)
  Radius = 8
FEATURE [Part::Cylinder] Cylinder768  label="Válec768"
  Angle = 360
  AttacherType = Attacher::AttachEngine3D
  Height = 20
  Placement = pos=(16.0727,-38.8029,0) rot=(0,0,1;0.785398rad)
  Radius = 8
FEATURE [Part::Compound] Compound719
  Links = -> [Cylinder768,Cylinder766,Cylinder765,Cylinder767,Cylinder762,Cylinder769,Cylinder764,Cylinder763]
  Placement = pos=(0,0,56) rot=(0,0,1;0rad)
FEATURE [Part::Cylinder] Cylinder796  label="Válec796"
  Angle = 360
  AttacherType = Attacher::AttachEngine3D
  Height = 100
  Placement = pos=(-38.8029,16.0727,0) rot=(0,0,-1;1.5708rad)
  Radius = 1.5
FEATURE [Part::Cylinder] Cylinder798  label="Válec798"
  Angle = 360
  AttacherType = Attacher::AttachEngine3D
  Height = 100
  Placement = pos=(-16.0727,-38.8029,0) rot=(0,0,1;0rad)
  Radius = 1.5
FEATURE [Part::Cylinder] Cylinder797  label="Válec797"
  Angle = 360
  AttacherType = Attacher::AttachEngine3D
  Height = 100
  Placement = pos=(38.8029,16.0727,0) rot=(0,0,1;2.35619rad)
  Radius = 1.5
FEATURE [Part::Cylinder] Cylinder799  label="Válec799"
  Angle = 360
  AttacherType = Attacher::AttachEngine3D
  Height = 100
  Placement = pos=(41.0044,-9.09046,0) rot=(0,0,1;1.74533rad)
  Radius = 1.5
FEATURE [Part::FeaturePython] Tube084  # WARN: FeaturePython — macro-defined, semantics opaque (R4)
  AttacherType = Attacher::AttachEngine3D
  Height = 7
  InnerRadius = 53
  OuterRadius = 54.4
  Placement = pos=(0,0,-22) rot=(0,0,1;0rad)
FEATURE [Part::FeaturePython] Tube081  # WARN: FeaturePython — macro-defined, semantics opaque (R4)
  AttacherType = Attacher::AttachEngine3D
  Height = 8
  InnerRadius = 30
  OuterRadius = 38.75
  Placement = pos=(0,0,58) rot=(0,0,1;0rad)
FEATURE [Part::Cut] Cut331
  Base = -> Tube081
  Tool = -> Compound708
FEATURE [Part::Chamfer] Chamfer004
  Base = -> Cut331
  Edges = 9 edges r=1: [Edge4,Edge5,Edge26,Edge28,Edge30,Edge32,Edge34,Edge36,Edge38]
FEATURE [Part::FeaturePython] Tube082  # WARN: FeaturePython — macro-defined, semantics opaque (R4)
  AttacherType = Attacher::AttachEngine3D
  Height = 8
  InnerRadius = 30
  OuterRadius = 58
  Placement = pos=(0,0,52) rot=(0,0,1;0rad)
FEATURE [Part::Cut] Cut332
  Base = -> Tube082
  Tool = -> Compound719
FEATURE [Part::FeaturePython] Tube083  # WARN: FeaturePython — macro-defined, semantics opaque (R4)
  AttacherType = Attacher::AttachEngine3D
  Height = 3
  InnerRadius = 54
  OuterRadius = 61
  Placement = pos=(0,0,52) rot=(0,0,1;0rad)
FEATURE [Part::Chamfer] Chamfer003
  Base = -> Tube083
  Edges = 1 edges r=1: [Edge3]
FEATURE [Part::FeaturePython] Tube085  # WARN: FeaturePython — macro-defined, semantics opaque (R4)
  AttacherType = Attacher::AttachEngine3D
  Height = 7
  InnerRadius = 53
  OuterRadius = 54.4
  Placement = pos=(0,0,-22) rot=(0,0,1;0rad)
FEATURE [Part::FeaturePython] Tube086  # WARN: FeaturePython — macro-defined, semantics opaque (R4)
  AttacherType = Attacher::AttachEngine3D
  Height = 3
  InnerRadius = 54
  OuterRadius = 61
  Placement = pos=(0,0,42) rot=(0,0,1;0rad)
FEATURE [Part::FeaturePython] Tube087  # WARN: FeaturePython — macro-defined, semantics opaque (R4)
  AttacherType = Attacher::AttachEngine3D
  Height = 10
  InnerRadius = 30
  OuterRadius = 57
  Placement = pos=(0,0,42) rot=(0,0,1;0rad)
FEATURE [Part::Cylinder] Cylinder807  label="Válec807"
  Angle = 360
  AttacherType = Attacher::AttachEngine3D
  Height = 100
  Placement = pos=(-16.0727,-38.8029,0) rot=(0,0,1;0rad)
  Radius = 1.5
FEATURE [Part::Box] Box312  label="Krychle312"
  AttacherType = Attacher::AttachEngine3D
  Height = 7
  Length = 60
  Placement = pos=(0,0,-22) rot=(0,0,-1;0.034907rad)
  Width = 60
FEATURE [Part::Cylinder] Cylinder800  label="Válec800"
  Angle = 360
  AttacherType = Attacher::AttachEngine3D
  Height = 100
  Placement = pos=(-41.0044,-9.09046,0) rot=(0,0,-1;0.959931rad)
  Radius = 1.5
FEATURE [Part::Cylinder] Cylinder801  label="Válec801"
  Angle = 360
  AttacherType = Attacher::AttachEngine3D
  Height = 100
  Placement = pos=(16.0727,38.8029,0) rot=(0,0,1;3.14159rad)
  Radius = 1.5
FEATURE [Part::Cylinder] Cylinder802  label="Válec802"
  Angle = 360
  AttacherType = Attacher::AttachEngine3D
  Height = 100
  Placement = pos=(16.0727,-38.8029,0) rot=(0,0,1;0.785398rad)
  Radius = 1.5
FEATURE [Part::Cylinder] Cylinder803  label="Válec803"
  Angle = 360
  AttacherType = Attacher::AttachEngine3D
  Height = 100
  Placement = pos=(-16.0727,38.8029,0) rot=(0,0,1;3.92699rad)
  Radius = 1.5
FEATURE [Part::Compound] Compound716
  Links = -> [Cylinder802,Cylinder799,Cylinder797,Cylinder801,Cylinder803,Cylinder796,Cylinder800,Cylinder798]
FEATURE [Part::Cut] Cut333
  Base = -> Cut332
  Tool = -> Compound716
FEATURE [Part::Compound] Compound717  label="bazovina_part-F_pedestal-axial-B"
  Links = -> [Chamfer003,Chamfer004,Cut333]
FEATURE [Part::Box] Box309  label="Krychle309"
  AttacherType = Attacher::AttachEngine3D
  Height = 7
  Length = 120
  Placement = pos=(-60,-60,-22) rot=(0,0,-1;0rad)
  Width = 60
FEATURE [Part::Cut] Cut334
  Base = -> Tube085
  Tool = -> Box309
FEATURE [Part::Box] Box311  label="Krychle311"
  AttacherType = Attacher::AttachEngine3D
  Height = 7
  Length = 60
  Placement = pos=(-59.9909,-1.04714,-22) rot=(0,0,1;0.017453rad)
  Width = 60
FEATURE [Part::Compound] Compound720
  Links = -> [Box312,Box311]
FEATURE [Part::Box] Box307  label="Krychle307"
  AttacherType = Attacher::AttachEngine3D
  Height = 7
  Length = 60
  Placement = pos=(0,0,-22) rot=(0,0,-1;0.349066rad)
  Width = 60
FEATURE [Part::Cylinder] Cylinder804  label="Válec804"
  Angle = 360
  AttacherType = Attacher::AttachEngine3D
  Height = 7
  Placement = pos=(0,0,-22) rot=(0,0,1;0rad)
  Radius = 52
FEATURE [Part::Box] Box314  label="Krychle314"
  AttacherType = Attacher::AttachEngine3D
  Height = 7
  Length = 1.4
  Placement = pos=(0,0,-22) rot=(0,0,-1;0.034907rad)
  Width = 60
FEATURE [Part::Box] Box308  label="Krychle308"
  AttacherType = Attacher::AttachEngine3D
  Height = 7
  Length = 60
  Placement = pos=(-56.3816,-20.5212,-22) rot=(0,0,1;0.349066rad)
  Width = 60
FEATURE [Part::Compound] Compound718
  Links = -> [Box307,Box308]
FEATURE [Part::Cut] Cut336
  Base = -> Cut334
  Placement = pos=(0,0,-7) rot=(0,0,1;0rad)
  Tool = -> Compound718
FEATURE [Part::Box] Box313  label="Krychle313"
  AttacherType = Attacher::AttachEngine3D
  Height = 7
  Length = 1.4
  Placement = pos=(0,0,-22) rot=(0,0,1;0.047124rad)
  Width = 60
FEATURE [Part::Cylinder] Cylinder805  label="Válec805"
  Angle = 360
  AttacherType = Attacher::AttachEngine3D
  Height = 100
  Placement = pos=(-38.8029,16.0727,0) rot=(0,0,-1;1.5708rad)
  Radius = 1.5
FEATURE [Part::Box] Box310  label="Krychle310"
  AttacherType = Attacher::AttachEngine3D
  Height = 7
  Length = 120
  Placement = pos=(-60,-60,-22) rot=(0,0,-1;0rad)
  Width = 60
FEATURE [Part::Cut] Cut337
  Base = -> Tube084
  Tool = -> Box310
FEATURE [Part::Cut] Cut338
  Base = -> Cut337
  Placement = pos=(0,0,-7) rot=(0,0,1;0rad)
  Tool = -> Compound720
FEATURE [Part::Cut] Cut335
  Base = -> Cut336
  Placement = pos=(0,0,74) rot=(0,0,1;3.92699rad)
  Tool = -> Cut338
FEATURE [Part::Cylinder] Cylinder806  label="Válec806"
  Angle = 360
  AttacherType = Attacher::AttachEngine3D
  Height = 100
  Placement = pos=(38.8029,16.0727,0) rot=(0,0,1;2.35619rad)
  Radius = 1.5
FEATURE [Part::Cylinder] Cylinder808  label="Válec808"
  Angle = 360
  AttacherType = Attacher::AttachEngine3D
  Height = 100
  Placement = pos=(41.0044,-9.09046,0) rot=(0,0,1;1.74533rad)
  Radius = 1.5
FEATURE [Part::Cylinder] Cylinder809  label="Válec809"
  Angle = 360
  AttacherType = Attacher::AttachEngine3D
  Height = 100
  Placement = pos=(-41.0044,-9.09046,0) rot=(0,0,-1;0.959931rad)
  Radius = 1.5
FEATURE [Part::Cylinder] Cylinder811  label="Válec811"
  Angle = 360
  AttacherType = Attacher::AttachEngine3D
  Height = 100
  Placement = pos=(16.0727,-38.8029,0) rot=(0,0,1;0.785398rad)
  Radius = 1.5
FEATURE [Part::Cylinder] Cylinder810  label="Válec810"
  Angle = 360
  AttacherType = Attacher::AttachEngine3D
  Height = 100
  Placement = pos=(16.0727,38.8029,0) rot=(0,0,1;3.14159rad)
  Radius = 1.5
FEATURE [Part::Cylinder] Cylinder812  label="Válec812"
  Angle = 360
  AttacherType = Attacher::AttachEngine3D
  Height = 100
  Placement = pos=(-16.0727,38.8029,0) rot=(0,0,1;3.92699rad)
  Radius = 1.5
FEATURE [Part::Chamfer] Chamfer005
  Base = -> Tube086
  Edges = 1 edges r=1: [Edge1]
FEATURE [Part::Compound] Compound723
  Links = -> [Box314,Box313]
FEATURE [Part::Cut] Cut339
  Base = -> Compound723
  Placement = pos=(0,0,67) rot=(0,0,1;3.92524rad)
  Tool = -> Cylinder804
FEATURE [Part::Compound] Compound721
  Links = -> [Cylinder811,Cylinder808,Cylinder806,Cylinder810,Cylinder812,Cylinder805,Cylinder809,Cylinder807]
FEATURE [Part::Cut] Cut340
  Base = -> Tube087
  Tool = -> Compound721
FEATURE [Part::Cut] Cut341
  Base = -> Cut340
  Tool = -> Cut339
FEATURE [Part::Cut] Cut342
  Base = -> Cut341
  Tool = -> Cut335
FEATURE [Part::Compound] Compound722  label="bazovina_part-F_pedestal-axial-A-belt"
  Links = -> [Chamfer005,Cut342]
FEATURE [Part::Cylinder] Cylinder2007  label="Válec2007"
  Angle = 360
  AttacherType = Attacher::AttachEngine3D
  Height = 72
  Placement = pos=(35.5,-61.4878,0) rot=(0,0,1;0.523599rad)
  Radius = 1.5
FEATURE [Part::Cylinder] Cylinder2006  label="Válec2006"
  Angle = 360
  AttacherType = Attacher::AttachEngine3D
  Height = 72
  Placement = pos=(61.4878,-35.5,0) rot=(0,0,1;1.0472rad)
  Radius = 1.5
FEATURE [Part::Cylinder] Cylinder2011  label="Válec2011"
  Angle = 360
  AttacherType = Attacher::AttachEngine3D
  Height = 72
  Placement = pos=(71,-1.8e-14,0) rot=(0,0,1;1.5708rad)
  Radius = 1.5
FEATURE [Part::Cylinder] Cylinder2019  label="Válec2019"
  Angle = 360
  AttacherType = Attacher::AttachEngine3D
  Height = 72
  Placement = pos=(35.5,-61.4878,0) rot=(0,0,1;0.523599rad)
  Radius = 1.5
FEATURE [Part::Cylinder] Cylinder2021  label="Válec2021"
  Angle = 360
  AttacherType = Attacher::AttachEngine3D
  Height = 72
  Placement = pos=(0,-71,0) rot=(0,0,1;0rad)
  Radius = 1.5
FEATURE [Part::Cylinder] Cylinder2009  label="Válec2009"
  Angle = 360
  AttacherType = Attacher::AttachEngine3D
  Height = 72
  Placement = pos=(0,-71,0) rot=(0,0,1;0rad)
  Radius = 1.5
FEATURE [Part::Cylinder] Cylinder2016  label="Válec2016"
  Angle = 360
  AttacherType = Attacher::AttachEngine3D
  Height = 72
  Placement = pos=(-61.4878,35.5,0) rot=(0,0,1;4.18879rad)
  Radius = 1.5
FEATURE [Part::Cylinder] Cylinder2015  label="Válec2015"
  Angle = 360
  AttacherType = Attacher::AttachEngine3D
  Height = 72
  Placement = pos=(-71,2.7e-14,0) rot=(0,0,-1;1.5708rad)
  Radius = 1.5
FEATURE [Part::Cylinder] Cylinder2010  label="Válec2010"
  Angle = 360
  AttacherType = Attacher::AttachEngine3D
  Height = 72
  Placement = pos=(3.1e-14,71,0) rot=(0,0,1;3.14159rad)
  Radius = 1.5
FEATURE [Part::Cylinder] Cylinder2008  label="Válec2008"
  Angle = 360
  AttacherType = Attacher::AttachEngine3D
  Height = 72
  Placement = pos=(-61.4878,-35.5,0) rot=(0,0,-1;1.0472rad)
  Radius = 1.5
FEATURE [Part::Cylinder] Cylinder2012  label="Válec2012"
  Angle = 360
  AttacherType = Attacher::AttachEngine3D
  Height = 72
  Placement = pos=(61.4878,35.5,0) rot=(0,0,1;2.0944rad)
  Radius = 1.5
FEATURE [Part::Cylinder] Cylinder2013  label="Válec2013"
  Angle = 360
  AttacherType = Attacher::AttachEngine3D
  Height = 72
  Placement = pos=(35.5,61.4878,0) rot=(0,0,1;2.61799rad)
  Radius = 1.5
FEATURE [Part::Cylinder] Cylinder2014  label="Válec2014"
  Angle = 360
  AttacherType = Attacher::AttachEngine3D
  Height = 72
  Placement = pos=(-35.5,-61.4878,0) rot=(0,0,-1;0.523599rad)
  Radius = 1.5
FEATURE [Part::Cylinder] Cylinder2017  label="Válec2017"
  Angle = 360
  AttacherType = Attacher::AttachEngine3D
  Height = 72
  Placement = pos=(-35.5,61.4878,0) rot=(0,0,1;3.66519rad)
  Radius = 1.5
FEATURE [Part::Cylinder] Cylinder2018  label="Válec2018"
  Angle = 360
  AttacherType = Attacher::AttachEngine3D
  Height = 72
  Placement = pos=(61.4878,-35.5,0) rot=(0,0,1;1.0472rad)
  Radius = 1.5
FEATURE [Part::Cylinder] Cylinder2020  label="Válec2020"
  Angle = 360
  AttacherType = Attacher::AttachEngine3D
  Height = 72
  Placement = pos=(-61.4878,-35.5,0) rot=(0,0,-1;1.0472rad)
  Radius = 1.5
FEATURE [Part::Cylinder] Cylinder2025  label="Válec2025"
  Angle = 360
  AttacherType = Attacher::AttachEngine3D
  Height = 72
  Placement = pos=(35.5,61.4878,0) rot=(0,0,1;2.61799rad)
  Radius = 1.5
FEATURE [Part::Cylinder] Cylinder2029  label="Válec2029"
  Angle = 360
  AttacherType = Attacher::AttachEngine3D
  Height = 72
  Placement = pos=(-71,2.7e-14,0) rot=(0,0,-1;1.5708rad)
  Radius = 1.5
FEATURE [Part::Cylinder] Cylinder2031  label="Válec2031"
  Angle = 360
  AttacherType = Attacher::AttachEngine3D
  Height = 32
  Placement = pos=(35.5,-61.4878,0) rot=(0,0,1;0.523599rad)
  Radius = 4
FEATURE [Part::Cylinder] Cylinder2032  label="Válec2032"
  Angle = 360
  AttacherType = Attacher::AttachEngine3D
  Height = 32
  Placement = pos=(-61.4878,-35.5,0) rot=(0,0,-1;1.0472rad)
  Radius = 4
FEATURE [Part::Cylinder] Cylinder2036  label="Válec2036"
  Angle = 360
  AttacherType = Attacher::AttachEngine3D
  Height = 32
  Placement = pos=(61.4878,35.5,0) rot=(0,0,1;2.0944rad)
  Radius = 4
FEATURE [Part::Cylinder] Cylinder2034  label="Válec2034"
  Angle = 360
  AttacherType = Attacher::AttachEngine3D
  Height = 32
  Placement = pos=(3.1e-14,71,0) rot=(0,0,1;3.14159rad)
  Radius = 4
FEATURE [Part::Cylinder] Cylinder2035  label="Válec2035"
  Angle = 360
  AttacherType = Attacher::AttachEngine3D
  Height = 32
  Placement = pos=(71,-1.8e-14,0) rot=(0,0,1;1.5708rad)
  Radius = 4
FEATURE [Part::Cylinder] Cylinder2037  label="Válec2037"
  Angle = 360
  AttacherType = Attacher::AttachEngine3D
  Height = 32
  Placement = pos=(35.5,61.4878,0) rot=(0,0,1;2.61799rad)
  Radius = 4
FEATURE [Part::Cylinder] Cylinder2038  label="Válec2038"
  Angle = 360
  AttacherType = Attacher::AttachEngine3D
  Height = 32
  Placement = pos=(-61.4878,35.5,0) rot=(0,0,1;4.18879rad)
  Radius = 4
FEATURE [Part::Cylinder] Cylinder2039  label="Válec2039"
  Angle = 360
  AttacherType = Attacher::AttachEngine3D
  Height = 32
  Placement = pos=(-35.5,61.4878,0) rot=(0,0,1;3.66519rad)
  Radius = 4
FEATURE [Part::Cylinder] Cylinder2022  label="Válec2022"
  Angle = 360
  AttacherType = Attacher::AttachEngine3D
  Height = 72
  Placement = pos=(3.1e-14,71,0) rot=(0,0,1;3.14159rad)
  Radius = 1.5
FEATURE [Part::Cylinder] Cylinder2028  label="Válec2028"
  Angle = 360
  AttacherType = Attacher::AttachEngine3D
  Height = 72
  Placement = pos=(-35.5,-61.4878,0) rot=(0,0,-1;0.523599rad)
  Radius = 1.5
FEATURE [Part::Cylinder] Cylinder2040  label="Válec2040"
  Angle = 360
  AttacherType = Attacher::AttachEngine3D
  Height = 32
  Placement = pos=(-35.5,-61.4878,0) rot=(0,0,-1;0.523599rad)
  Radius = 4
FEATURE [Part::Cylinder] Cylinder2023  label="Válec2023"
  Angle = 360
  AttacherType = Attacher::AttachEngine3D
  Height = 72
  Placement = pos=(71,-1.8e-14,0) rot=(0,0,1;1.5708rad)
  Radius = 1.5
FEATURE [Part::Cylinder] Cylinder2026  label="Válec2026"
  Angle = 360
  AttacherType = Attacher::AttachEngine3D
  Height = 72
  Placement = pos=(-61.4878,35.5,0) rot=(0,0,1;4.18879rad)
  Radius = 1.5
FEATURE [Part::Cylinder] Cylinder2024  label="Válec2024"
  Angle = 360
  AttacherType = Attacher::AttachEngine3D
  Height = 72
  Placement = pos=(61.4878,35.5,0) rot=(0,0,1;2.0944rad)
  Radius = 1.5
FEATURE [Part::Cylinder] Cylinder2027  label="Válec2027"
  Angle = 360
  AttacherType = Attacher::AttachEngine3D
  Height = 72
  Placement = pos=(-35.5,61.4878,0) rot=(0,0,1;3.66519rad)
  Radius = 1.5
FEATURE [Part::Cylinder] Cylinder2030  label="Válec2030"
  Angle = 360
  AttacherType = Attacher::AttachEngine3D
  Height = 32
  Placement = pos=(61.4878,-35.5,0) rot=(0,0,1;1.0472rad)
  Radius = 4
FEATURE [Part::Cylinder] Cylinder2033  label="Válec2033"
  Angle = 360
  AttacherType = Attacher::AttachEngine3D
  Height = 32
  Placement = pos=(0,-71,0) rot=(0,0,1;0rad)
  Radius = 4
FEATURE [Part::Cylinder] Cylinder2041  label="Válec2041"
  Angle = 360
  AttacherType = Attacher::AttachEngine3D
  Height = 32
  Placement = pos=(-71,2.7e-14,0) rot=(0,0,-1;1.5708rad)
  Radius = 4
FEATURE [Part::Box] Box315  label="Krychle315"
  AttacherType = Attacher::AttachEngine3D
  Height = 15
  Length = 148
  Placement = pos=(-74,0,16) rot=(0,0,1;0rad)
  Width = 48
FEATURE [Part::Box] Box316  label="Krychle316"
  AttacherType = Attacher::AttachEngine3D
  Height = 6
  Length = 8
  Placement = pos=(67,38,21) rot=(0,0,1;0rad)
  Width = 2
FEATURE [Part::Cylinder] Cylinder2042  label="Válec2042"
  Angle = 360
  AttacherType = Attacher::AttachEngine3D
  Height = 15
  Placement = pos=(0,0,16) rot=(0,0,1;0rad)
  Radius = 74
FEATURE [Part::Cylinder] Cylinder2043  label="Válec2043"
  Angle = 360
  AttacherType = Attacher::AttachEngine3D
  Height = 15
  Placement = pos=(0,0,16) rot=(0,0,1;0rad)
  Radius = 74
FEATURE [Part::Cylinder] Cylinder2044  label="Válec2044"
  Angle = 360
  AttacherType = Attacher::AttachEngine3D
  Height = 50
  Placement = pos=(-71,80,24) rot=(1,0,0;1.5708rad)
  Radius = 1.5
FEATURE [Part::Cylinder] Cylinder2045  label="Válec2045"
  Angle = 360
  AttacherType = Attacher::AttachEngine3D
  Height = 50
  Placement = pos=(71,80,24) rot=(1,0,0;1.5708rad)
  Radius = 1.5
FEATURE [Part::Box] Box317  label="Krychle317"
  AttacherType = Attacher::AttachEngine3D
  Height = 6
  Length = 8
  Placement = pos=(-75,38,21) rot=(0,0,1;0rad)
  Width = 2
FEATURE [Part::Box] Box318  label="Krychle318"
  AttacherType = Attacher::AttachEngine3D
  Height = 47
  Length = 56
  Placement = pos=(-28,0,27) rot=(0,0,1;0rad)
  Width = 200
FEATURE [Part::Cut] Cut684
  Base = -> Box315
  Tool = -> Cylinder2043
FEATURE [Part::Cut] Cut685
  Base = -> Cut684
  Tool = -> Cylinder2042
FEATURE [Part::FeaturePython] Tube052  label="ring001"  # WARN: FeaturePython — macro-defined, semantics opaque (R4)
  AttacherType = Attacher::AttachEngine3D
  Height = 4
  InnerRadius = 60
  OuterRadius = 74
  Placement = pos=(0,0,25) rot=(0,0,1;0rad)
FEATURE [Part::FeaturePython] Tube051  label="ring"  # WARN: FeaturePython — macro-defined, semantics opaque (R4)
  AttacherType = Attacher::AttachEngine3D
  Height = 22
  InnerRadius = 65.1
  OuterRadius = 74
  Placement = pos=(0,0,3) rot=(0,0,1;0rad)
FEATURE [Part::Compound] Compound1086
  Links = -> [Cylinder2033,Cylinder2031,Cylinder2030,Cylinder2035,Cylinder2036,Cylinder2037,Cylinder2034,Cylinder2039,Cylinder2038,Cylinder2041,Cylinder2032,Cylinder2040]
  Placement = pos=(0,0,-18) rot=(0,0,1;0rad)
FEATURE [Part::Compound] Compound1084
  Links = -> [Cylinder2009,Cylinder2007,Cylinder2006,Cylinder2011,Cylinder2012,Cylinder2013,Cylinder2010,Cylinder2017,Cylinder2016,Cylinder2015,Cylinder2008,Cylinder2014]
  Placement = pos=(0,0,-4) rot=(0,0,1;0rad)
FEATURE [Part::Cut] Cut678
  Base = -> Tube052
  Tool = -> Compound1084
FEATURE [Part::Cut] Cut683
  Base = -> Cut678
  Tool = -> Box318
FEATURE [Part::Compound] Compound1087
  Links = -> [Box316,Box317]
FEATURE [Part::Cut] Cut681
  Base = -> Cut685
  Tool = -> Compound1087
FEATURE [Part::Compound] Compound1085
  Links = -> [Cylinder2021,Cylinder2019,Cylinder2018,Cylinder2023,Cylinder2024,Cylinder2025,Cylinder2022,Cylinder2027,Cylinder2026,Cylinder2029,Cylinder2020,Cylinder2028]
  Placement = pos=(0,0,-4) rot=(0,0,1;0rad)
FEATURE [Part::Cut] Cut679
  Base = -> Tube051
  Tool = -> Compound1085
FEATURE [Part::Cut] Cut680
  Base = -> Cut679
  Tool = -> Compound1086
FEATURE [Part::Compound] Compound1088
  Links = -> [Cylinder2045,Cylinder2044]
FEATURE [Part::Cut] Cut682
  Base = -> Cut681
  Placement = pos=(0,0,-2) rot=(0,0,1;0rad)
  Tool = -> Compound1088
FEATURE [Part::Cylinder] Cylinder2105  label="Válec2105"
  Angle = 360
  AttacherType = Attacher::AttachEngine3D
  Height = 32
  Placement = pos=(61.4878,35.5,0) rot=(0,0,1;2.0944rad)
  Radius = 1.5
FEATURE [Part::Cylinder] Cylinder2103  label="Válec2103"
  Angle = 360
  AttacherType = Attacher::AttachEngine3D
  Height = 32
  Placement = pos=(3.1e-14,71,0) rot=(0,0,1;3.14159rad)
  Radius = 1.5
FEATURE [Part::Cylinder] Cylinder2104  label="Válec2104"
  Angle = 360
  AttacherType = Attacher::AttachEngine3D
  Height = 32
  Placement = pos=(71,-1.8e-14,0) rot=(0,0,1;1.5708rad)
  Radius = 1.5
FEATURE [Part::Cylinder] Cylinder2099  label="Válec2099"
  Angle = 360
  AttacherType = Attacher::AttachEngine3D
  Height = 32
  Placement = pos=(61.4878,-35.5,0) rot=(0,0,1;1.0472rad)
  Radius = 1.5
FEATURE [Part::Cylinder] Cylinder2106  label="Válec2106"
  Angle = 360
  AttacherType = Attacher::AttachEngine3D
  Height = 32
  Placement = pos=(35.5,61.4878,0) rot=(0,0,1;2.61799rad)
  Radius = 1.5
FEATURE [Part::Box] Box1003  label="Krychle1003"
  AttacherType = Attacher::AttachEngine3D
  Height = 2
  Length = 6
  Placement = pos=(-40.0981,-63.4519,39) rot=(0,0,-1;0.523599rad)
  Width = 8
FEATURE [Part::Cylinder] Cylinder2107  label="Válec2107"
  Angle = 360
  AttacherType = Attacher::AttachEngine3D
  Height = 32
  Placement = pos=(-35.5,-61.4878,0) rot=(0,0,-1;0.523599rad)
  Radius = 1.5
FEATURE [Part::Cylinder] Cylinder2102  label="Válec2102"
  Angle = 360
  AttacherType = Attacher::AttachEngine3D
  Height = 32
  Placement = pos=(0,-71,0) rot=(0,0,1;0rad)
  Radius = 1.5
FEATURE [Part::Cylinder] Cylinder2108  label="Válec2108"
  Angle = 360
  AttacherType = Attacher::AttachEngine3D
  Height = 32
  Placement = pos=(-71,2.7e-14,0) rot=(0,0,-1;1.5708rad)
  Radius = 1.5
FEATURE [Part::Cylinder] Cylinder2110  label="Válec2110"
  Angle = 360
  AttacherType = Attacher::AttachEngine3D
  Height = 32
  Placement = pos=(-35.5,61.4878,0) rot=(0,0,1;3.66519rad)
  Radius = 1.5
FEATURE [Part::Cylinder] Cylinder2101  label="Válec2101"
  Angle = 360
  AttacherType = Attacher::AttachEngine3D
  Height = 32
  Placement = pos=(-61.4878,-35.5,0) rot=(0,0,-1;1.0472rad)
  Radius = 1.5
FEATURE [Part::Cylinder] Cylinder2100  label="Válec2100"
  Angle = 360
  AttacherType = Attacher::AttachEngine3D
  Height = 32
  Placement = pos=(35.5,-61.4878,0) rot=(0,0,1;0.523599rad)
  Radius = 1.5
FEATURE [Part::Cylinder] Cylinder2109  label="Válec2109"
  Angle = 360
  AttacherType = Attacher::AttachEngine3D
  Height = 32
  Placement = pos=(-61.4878,35.5,0) rot=(0,0,1;4.18879rad)
  Radius = 1.5
FEATURE [Part::Box] Box992  label="Krychle992"
  AttacherType = Attacher::AttachEngine3D
  Height = 2
  Length = 6
  Placement = pos=(66.4519,34.9019,39) rot=(0,0,1;2.0944rad)
  Width = 8
FEATURE [Part::Box] Box993  label="Krychle993"
  AttacherType = Attacher::AttachEngine3D
  Height = 2
  Length = 6
  Placement = pos=(75,-3,39) rot=(0,0,1;1.5708rad)
  Width = 8
FEATURE [Part::Box] Box995  label="Krychle995"
  AttacherType = Attacher::AttachEngine3D
  Height = 2
  Length = 6
  Placement = pos=(-63.4519,40.0981,39) rot=(0,0,1;4.18879rad)
  Width = 8
FEATURE [Part::Box] Box997  label="Krychle997"
  AttacherType = Attacher::AttachEngine3D
  Height = 2
  Length = 6
  Placement = pos=(34.9019,-66.4519,39) rot=(0,0,1;0.523599rad)
  Width = 8
FEATURE [Part::Box] Box998  label="Krychle998"
  AttacherType = Attacher::AttachEngine3D
  Height = 2
  Length = 6
  Placement = pos=(-34.9019,66.4519,39) rot=(0,0,1;3.66519rad)
  Width = 8
FEATURE [Part::Box] Box999  label="Krychle999"
  AttacherType = Attacher::AttachEngine3D
  Height = 2
  Length = 6
  Placement = pos=(40.0981,63.4519,39) rot=(0,0,1;2.61799rad)
  Width = 8
FEATURE [Part::Box] Box1000  label="Krychle1000"
  AttacherType = Attacher::AttachEngine3D
  Height = 2
  Length = 6
  Placement = pos=(-75,3,39) rot=(0,0,-1;1.5708rad)
  Width = 8
FEATURE [Part::Box] Box1001  label="Krychle1001"
  AttacherType = Attacher::AttachEngine3D
  Height = 2
  Length = 6
  Placement = pos=(63.4519,-40.0981,39) rot=(0,0,1;1.0472rad)
  Width = 8
FEATURE [Part::Box] Box996  label="Krychle996"
  AttacherType = Attacher::AttachEngine3D
  Height = 2
  Length = 6
  Placement = pos=(-3,-75,39) rot=(0,0,1;0rad)
  Width = 8
FEATURE [Part::Box] Box1002  label="Krychle1002"
  AttacherType = Attacher::AttachEngine3D
  Height = 2
  Length = 6
  Placement = pos=(-66.4519,-34.9019,39) rot=(0,0,-1;1.0472rad)
  Width = 8
FEATURE [Part::Box] Box994  label="Krychle994"
  AttacherType = Attacher::AttachEngine3D
  Height = 2
  Length = 6
  Placement = pos=(3,75,39) rot=(0,0,1;3.14159rad)
  Width = 8
FEATURE [Part::Compound] Compound1114
  Links = -> [Cylinder2102,Cylinder2100,Cylinder2099,Cylinder2104,Cylinder2105,Cylinder2106,Cylinder2103,Cylinder2110,Cylinder2109,Cylinder2108,Cylinder2101,Cylinder2107]
  Placement = pos=(0,0,-13) rot=(0,0,1;0.261799rad)
FEATURE [Part::Compound] Compound1113
  Links = -> [Box996,Box997,Box1001,Box993,Box992,Box999,Box994,Box998,Box995,Box1000,Box1002,Box1003]
  Placement = pos=(0,0,-30) rot=(0,0,1;0.261799rad)
FEATURE [Part::Fillet] Fillet
  Base = -> Cut680
  Edges = 4 edges r=8: [Edge29,Edge31,Edge33,Edge35]
FEATURE [Part::Fillet] Fillet001
  Base = -> Fillet
  Edges = 4 edges r=8: [Edge26,Edge30,Edge34,Edge38]
FEATURE [Part::Fillet] Fillet002
  Base = -> Fillet001
  Edges = 4 edges r=8: [Edge26,Edge30,Edge34,Edge45]
FEATURE [Part::Fillet] Fillet003
  Base = -> Fillet002
  Edges = 6 edges r=8: [Edge33,Edge37,Edge41,Edge45,Edge49,Edge53]
FEATURE [Part::Fillet] Fillet004
  Base = -> Fillet003
  Edges = 6 edges r=8: [Edge37,Edge41,Edge45,Edge49,Edge53,Edge57]
FEATURE [Part::Cut] Cut703
  Base = -> Fillet004
  Tool = -> Compound1113
FEATURE [Part::Cut] Cut704
  Base = -> Cut703
  Tool = -> Compound1114
FEATURE [Part::Chamfer] Chamfer082
  Base = -> Cut704
  Edges = 1 edges r=1: [Edge171]
FEATURE [Part::Compound] Compound1115  label="Base_turret-big-ring"
  Links = -> [Cut682,Cut683,Chamfer082]
  Placement = pos=(0,0,2) rot=(0,0,1;0rad)
FEATURE [Part::Cylinder] Cylinder1631  label="Válec1631"
  Angle = 360
  AttacherType = Attacher::AttachEngine3D
  Height = 100
  Placement = pos=(-34,-16,-60) rot=(0,0,1;0rad)
  Radius = 1.5
FEATURE [Part::Cylinder] Cylinder1636  label="Válec1636"
  Angle = 360
  AttacherType = Attacher::AttachEngine3D
  Height = 100
  Placement = pos=(-16,-34,-60) rot=(0,0,1;0rad)
  Radius = 1.5
FEATURE [Part::Cylinder] Cylinder1634  label="Válec1634"
  Angle = 360
  AttacherType = Attacher::AttachEngine3D
  Height = 100
  Placement = pos=(16,34,-60) rot=(0,0,1;0rad)
  Radius = 1.5
FEATURE [Part::Cylinder] Cylinder1635  label="Válec1635"
  Angle = 360
  AttacherType = Attacher::AttachEngine3D
  Height = 100
  Placement = pos=(10,-36,-60) rot=(0,0,1;0rad)
  Radius = 1.5
FEATURE [Part::Cylinder] Cylinder1633  label="Válec1633"
  Angle = 360
  AttacherType = Attacher::AttachEngine3D
  Height = 100
  Placement = pos=(34,16,-60) rot=(0,0,1;0rad)
  Radius = 1.5
FEATURE [Part::Cylinder] Cylinder1632  label="Válec1632"
  Angle = 360
  AttacherType = Attacher::AttachEngine3D
  Height = 100
  Placement = pos=(34,-16,-60) rot=(0,0,1;0rad)
  Radius = 1.5
FEATURE [Part::Cylinder] Cylinder1630  label="Válec1630"
  Angle = 360
  AttacherType = Attacher::AttachEngine3D
  Height = 100
  Placement = pos=(-34,16,-60) rot=(0,0,1;0rad)
  Radius = 1.5
FEATURE [Part::Cylinder] Cylinder1637  label="Válec1637"
  Angle = 360
  AttacherType = Attacher::AttachEngine3D
  Height = 100
  Placement = pos=(-16,34,-60) rot=(0,0,1;0rad)
  Radius = 1.5
FEATURE [Part::Compound] Compound928  label="sbouby_baze009"
  Links = -> [Cylinder1630,Cylinder1631,Cylinder1632,Cylinder1633,Cylinder1634,Cylinder1635,Cylinder1636,Cylinder1637]
  Placement = pos=(0,0,40) rot=(0,0,1;0rad)
FEATURE [Part::FeaturePython] Tube044  label="ZKL-6017"  # WARN: FeaturePython — macro-defined, semantics opaque (R4)
  AttacherType = Attacher::AttachEngine3D
  Height = 22
  InnerRadius = 42.5
  OuterRadius = 65
  Placement = pos=(0,0,5) rot=(0,0,1;0rad)
FEATURE [Part::FeaturePython] Tube  # WARN: FeaturePython — macro-defined, semantics opaque (R4)
  AttacherType = Attacher::AttachEngine3D
  Height = 22
  InnerRadius = 24
  OuterRadius = 42.6
  Placement = pos=(0,0,5) rot=(0,0,1;0rad)
FEATURE [Part::Box] Box  label="Krychle"
  AttacherType = Attacher::AttachEngine3D
  Height = 20
  Length = 6
  Placement = pos=(13,31,0) rot=(0,0,1;0rad)
  Width = 6
FEATURE [Part::Box] Box1004  label="Krychle1004"
  AttacherType = Attacher::AttachEngine3D
  Height = 20
  Length = 6
  Placement = pos=(-19,31,0) rot=(0,0,1;0rad)
  Width = 6
FEATURE [Part::Box] Box1005  label="Krychle1005"
  AttacherType = Attacher::AttachEngine3D
  Height = 20
  Length = 6
  Placement = pos=(-19,-37,0) rot=(0,0,1;0rad)
  Width = 6
FEATURE [Part::Box] Box1006  label="Krychle1006"
  AttacherType = Attacher::AttachEngine3D
  Height = 20
  Length = 6
  Placement = pos=(7,-39,0) rot=(0,0,1;0rad)
  Width = 6
FEATURE [Part::Box] Box1007  label="Krychle1007"
  AttacherType = Attacher::AttachEngine3D
  Height = 20
  Length = 6
  Placement = pos=(31,13,0) rot=(0,0,1;0rad)
  Width = 6
FEATURE [Part::Box] Box1008  label="Krychle1008"
  AttacherType = Attacher::AttachEngine3D
  Height = 20
  Length = 6
  Placement = pos=(31,-19,0) rot=(0,0,1;0rad)
  Width = 6
FEATURE [Part::Box] Box1009  label="Krychle1009"
  AttacherType = Attacher::AttachEngine3D
  Height = 20
  Length = 6
  Placement = pos=(-37,13,0) rot=(0,0,1;0rad)
  Width = 6
FEATURE [Part::Box] Box1010  label="Krychle1010"
  AttacherType = Attacher::AttachEngine3D
  Height = 20
  Length = 6
  Placement = pos=(-37,-19,0) rot=(0,0,1;0rad)
  Width = 6
FEATURE [Part::Compound] Compound1116
  Links = -> [Box,Box1004,Box1005,Box1006,Box1007,Box1008,Box1009,Box1010]
  Placement = pos=(0,0,22) rot=(0,0,1;0rad)
FEATURE [Part::FeaturePython] Tube088  # WARN: FeaturePython — macro-defined, semantics opaque (R4)
  AttacherType = Attacher::AttachEngine3D
  Height = 5
  InnerRadius = 24
  OuterRadius = 58
  Placement = pos=(0,0,27) rot=(0,0,1;0rad)
FEATURE [Part::Cylinder] Cylinder1449  label="Válec1449"
  Angle = 360
  AttacherType = Attacher::AttachEngine3D
  Height = 40
  Placement = pos=(91,-27,-18) rot=(0,0,1;0rad)
  Radius = 4
FEATURE [Part::Cylinder] Cylinder1452  label="Válec1452"
  Angle = 360
  AttacherType = Attacher::AttachEngine3D
  Height = 40
  Placement = pos=(1,-12,-18) rot=(0,0,1;0rad)
  Radius = 4
FEATURE [Part::Cylinder] Cylinder1448  label="Válec1448"
  Angle = 360
  AttacherType = Attacher::AttachEngine3D
  Height = 40
  Placement = pos=(76,24,-18) rot=(0,0,1;0rad)
  Radius = 4
FEATURE [Part::Cylinder] Cylinder1446  label="Válec1446"
  Angle = 360
  AttacherType = Attacher::AttachEngine3D
  Height = 40
  Placement = pos=(103,-12,-20) rot=(0,0,1;0rad)
  Radius = 4
FEATURE [Part::Cylinder] Cylinder1451  label="Válec1451"
  Angle = 360
  AttacherType = Attacher::AttachEngine3D
  Height = 40
  Placement = pos=(28,24,-18) rot=(0,0,1;0rad)
  Radius = 4
FEATURE [Part::Cylinder] Cylinder1453  label="Válec1453"
  Angle = 360
  AttacherType = Attacher::AttachEngine3D
  Height = 40
  Placement = pos=(1,12,-18) rot=(0,0,1;0rad)
  Radius = 4
FEATURE [Part::Cylinder] Cylinder1447  label="Válec1447"
  Angle = 360
  AttacherType = Attacher::AttachEngine3D
  Height = 40
  Placement = pos=(103,12,-20) rot=(0,0,1;0rad)
  Radius = 4
FEATURE [Part::Cylinder] Cylinder1450  label="Válec1450"
  Angle = 360
  AttacherType = Attacher::AttachEngine3D
  Height = 40
  Placement = pos=(13,-27,-18) rot=(0,0,1;0rad)
  Radius = 4
FEATURE [Part::Compound] Compound664  label="srouby_monoblok_silne003"
  Links = -> [Cylinder1446,Cylinder1447,Cylinder1448,Cylinder1449,Cylinder1450,Cylinder1451,Cylinder1452,Cylinder1453]
  Placement = pos=(0,0,20) rot=(0,0,1;0rad)
FEATURE [Part::Cylinder] Cylinder2111  label="Válec2111"
  Angle = 360
  AttacherType = Attacher::AttachEngine3D
  Height = 40
  Placement = pos=(1,-12,-18) rot=(0,0,1;0rad)
  Radius = 4
FEATURE [Part::Cylinder] Cylinder2112  label="Válec2112"
  Angle = 360
  AttacherType = Attacher::AttachEngine3D
  Height = 40
  Placement = pos=(28,24,-18) rot=(0,0,1;0rad)
  Radius = 4
FEATURE [Part::Cylinder] Cylinder2113  label="Válec2113"
  Angle = 360
  AttacherType = Attacher::AttachEngine3D
  Height = 40
  Placement = pos=(103,12,-20) rot=(0,0,1;0rad)
  Radius = 4
FEATURE [Part::Cylinder] Cylinder2114  label="Válec2114"
  Angle = 360
  AttacherType = Attacher::AttachEngine3D
  Height = 40
  Placement = pos=(103,-12,-20) rot=(0,0,1;0rad)
  Radius = 4
FEATURE [Part::Cylinder] Cylinder2115  label="Válec2115"
  Angle = 360
  AttacherType = Attacher::AttachEngine3D
  Height = 40
  Placement = pos=(76,24,-18) rot=(0,0,1;0rad)
  Radius = 4
FEATURE [Part::Cylinder] Cylinder2116  label="Válec2116"
  Angle = 360
  AttacherType = Attacher::AttachEngine3D
  Height = 40
  Placement = pos=(1,12,-18) rot=(0,0,1;0rad)
  Radius = 4
FEATURE [Part::Cylinder] Cylinder2117  label="Válec2117"
  Angle = 360
  AttacherType = Attacher::AttachEngine3D
  Height = 40
  Placement = pos=(13,-27,-18) rot=(0,0,1;0rad)
  Radius = 4
FEATURE [Part::Cylinder] Cylinder2118  label="Válec2118"
  Angle = 360
  AttacherType = Attacher::AttachEngine3D
  Height = 40
  Placement = pos=(91,-27,-18) rot=(0,0,1;0rad)
  Radius = 4
FEATURE [Part::Compound] Compound1117  label="srouby_monoblok_silne004"
  Links = -> [Cylinder2114,Cylinder2113,Cylinder2115,Cylinder2118,Cylinder2117,Cylinder2112,Cylinder2111,Cylinder2116]
  Placement = pos=(0,0,20) rot=(0,0,1;0rad)
FEATURE [Part::Box] Box1011  label="Krychle1011"
  AttacherType = Attacher::AttachEngine3D
  Height = 20
  Length = 6
  Placement = pos=(13,31,0) rot=(0,0,1;0rad)
  Width = 6
FEATURE [Part::Box] Box1012  label="Krychle1012"
  AttacherType = Attacher::AttachEngine3D
  Height = 20
  Length = 6
  Placement = pos=(7,-39,0) rot=(0,0,1;0rad)
  Width = 6
FEATURE [Part::Box] Box1013  label="Krychle1013"
  AttacherType = Attacher::AttachEngine3D
  Height = 20
  Length = 6
  Placement = pos=(-37,13,0) rot=(0,0,1;0rad)
  Width = 6
FEATURE [Part::Box] Box1014  label="Krychle1014"
  AttacherType = Attacher::AttachEngine3D
  Height = 20
  Length = 6
  Placement = pos=(-19,31,0) rot=(0,0,1;0rad)
  Width = 6
FEATURE [Part::Box] Box1015  label="Krychle1015"
  AttacherType = Attacher::AttachEngine3D
  Height = 20
  Length = 6
  Placement = pos=(-19,-37,0) rot=(0,0,1;0rad)
  Width = 6
FEATURE [Part::Box] Box1016  label="Krychle1016"
  AttacherType = Attacher::AttachEngine3D
  Height = 20
  Length = 6
  Placement = pos=(31,13,0) rot=(0,0,1;0rad)
  Width = 6
FEATURE [Part::Box] Box1017  label="Krychle1017"
  AttacherType = Attacher::AttachEngine3D
  Height = 20
  Length = 6
  Placement = pos=(31,-19,0) rot=(0,0,1;0rad)
  Width = 6
FEATURE [Part::Box] Box1018  label="Krychle1018"
  AttacherType = Attacher::AttachEngine3D
  Height = 20
  Length = 6
  Placement = pos=(-37,-19,0) rot=(0,0,1;0rad)
  Width = 6
FEATURE [Part::Compound] Compound1118
  Links = -> [Box1011,Box1014,Box1015,Box1012,Box1016,Box1017,Box1013,Box1018]
  Placement = pos=(0,0,22) rot=(0,0,1;0rad)
FEATURE [Part::Cylinder] Cylinder2119  label="Válec2119"
  Angle = 360
  AttacherType = Attacher::AttachEngine3D
  Height = 100
  Placement = pos=(-34,-16,-60) rot=(0,0,1;0rad)
  Radius = 1.5
FEATURE [Part::Cylinder] Cylinder2120  label="Válec2120"
  Angle = 360
  AttacherType = Attacher::AttachEngine3D
  Height = 100
  Placement = pos=(-16,-34,-60) rot=(0,0,1;0rad)
  Radius = 1.5
FEATURE [Part::Cylinder] Cylinder2121  label="Válec2121"
  Angle = 360
  AttacherType = Attacher::AttachEngine3D
  Height = 100
  Placement = pos=(16,34,-60) rot=(0,0,1;0rad)
  Radius = 1.5
FEATURE [Part::Cylinder] Cylinder2122  label="Válec2122"
  Angle = 360
  AttacherType = Attacher::AttachEngine3D
  Height = 100
  Placement = pos=(-16,34,-60) rot=(0,0,1;0rad)
  Radius = 1.5
FEATURE [Part::Cylinder] Cylinder2123  label="Válec2123"
  Angle = 360
  AttacherType = Attacher::AttachEngine3D
  Height = 100
  Placement = pos=(34,-16,-60) rot=(0,0,1;0rad)
  Radius = 1.5
FEATURE [Part::Cylinder] Cylinder2124  label="Válec2124"
  Angle = 360
  AttacherType = Attacher::AttachEngine3D
  Height = 100
  Placement = pos=(-34,16,-60) rot=(0,0,1;0rad)
  Radius = 1.5
FEATURE [Part::Cylinder] Cylinder2125  label="Válec2125"
  Angle = 360
  AttacherType = Attacher::AttachEngine3D
  Height = 100
  Placement = pos=(10,-36,-60) rot=(0,0,1;0rad)
  Radius = 1.5
FEATURE [Part::Cylinder] Cylinder2126  label="Válec2126"
  Angle = 360
  AttacherType = Attacher::AttachEngine3D
  Height = 100
  Placement = pos=(34,16,-60) rot=(0,0,1;0rad)
  Radius = 1.5
FEATURE [Part::Compound] Compound1119  label="sbouby_baze010"
  Links = -> [Cylinder2124,Cylinder2119,Cylinder2123,Cylinder2126,Cylinder2121,Cylinder2125,Cylinder2120,Cylinder2122]
  Placement = pos=(0,0,40) rot=(0,0,1;0rad)
FEATURE [Part::Cut] Cut705
  Base = -> Tube088
  Tool = -> Compound1116
FEATURE [Part::Cut] Cut706
  Base = -> Tube
  Tool = -> Compound1118
FEATURE [Part::Chamfer] Chamfer
  Base = -> Cut706
  Edges = 1 edges r=1: [Edge3]
FEATURE [Part::Cut] Cut707
  Base = -> Chamfer
  Tool = -> Compound928
FEATURE [Part::Cut] Cut708
  Base = -> Cut705
  Tool = -> Compound1117
FEATURE [Part::Cut] Cut709
  Base = -> Cut707
  Tool = -> Compound664
FEATURE [Part::Cylinder] Cylinder2127  label="Válec2127"
  Angle = 360
  AttacherType = Attacher::AttachEngine3D
  Height = 100
  Placement = pos=(0,-38,0) rot=(0,0,1;0rad)
  Radius = 1.5
FEATURE [Part::Box] Box1019  label="Krychle1019"
  AttacherType = Attacher::AttachEngine3D
  Height = 2
  Length = 6
  Placement = pos=(-3,-33,31) rot=(0,0,1;0rad)
  Width = 10
FEATURE [Part::Box] Box1020  label="Krychle1020"
  AttacherType = Attacher::AttachEngine3D
  Height = 2
  Length = 6
  Placement = pos=(21.2132,-25.4558,31) rot=(0,0,1;0.785398rad)
  Width = 10
FEATURE [Part::Box] Box1021  label="Krychle1021"
  AttacherType = Attacher::AttachEngine3D
  Height = 2
  Length = 6
  Placement = pos=(33,-3,31) rot=(0,0,1;1.5708rad)
  Width = 10
FEATURE [Part::Box] Box1022  label="Krychle1022"
  AttacherType = Attacher::AttachEngine3D
  Height = 2
  Length = 6
  Placement = pos=(25.4558,21.2132,31) rot=(0,0,1;2.35619rad)
  Width = 10
FEATURE [Part::Box] Box1023  label="Krychle1023"
  AttacherType = Attacher::AttachEngine3D
  Height = 2
  Length = 6
  Placement = pos=(3,33,31) rot=(0,0,1;3.14159rad)
  Width = 10
FEATURE [Part::Box] Box1024  label="Krychle1024"
  AttacherType = Attacher::AttachEngine3D
  Height = 2
  Length = 6
  Placement = pos=(-21.2132,25.4558,31) rot=(0,0,1;3.92699rad)
  Width = 10
FEATURE [Part::Box] Box1025  label="Krychle1025"
  AttacherType = Attacher::AttachEngine3D
  Height = 2
  Length = 6
  Placement = pos=(-33,3,31) rot=(0,0,-1;1.5708rad)
  Width = 10
FEATURE [Part::Box] Box1026  label="Krychle1026"
  AttacherType = Attacher::AttachEngine3D
  Height = 2
  Length = 6
  Placement = pos=(-25.4558,-21.2132,31) rot=(0,0,-1;0.785398rad)
  Width = 10
FEATURE [Part::Compound] Compound1120
  Links = -> [Box1019,Box1020,Box1021,Box1022,Box1023,Box1024,Box1025,Box1026]
FEATURE [Part::Box] Box1027  label="Krychle1027"
  AttacherType = Attacher::AttachEngine3D
  Height = 2
  Length = 6
  Placement = pos=(-3,-43,5) rot=(0,0,1;0rad)
  Width = 8
FEATURE [Part::Box] Box1028  label="Krychle1028"
  AttacherType = Attacher::AttachEngine3D
  Height = 2
  Length = 6
  Placement = pos=(28.2843,-32.5269,5) rot=(0,0,1;0.785398rad)
  Width = 8
FEATURE [Part::Box] Box1029  label="Krychle1029"
  AttacherType = Attacher::AttachEngine3D
  Height = 2
  Length = 6
  Placement = pos=(43,-3,5) rot=(0,0,1;1.5708rad)
  Width = 8
FEATURE [Part::Box] Box1030  label="Krychle1030"
  AttacherType = Attacher::AttachEngine3D
  Height = 2
  Length = 6
  Placement = pos=(32.5269,28.2843,5) rot=(0,0,1;2.35619rad)
  Width = 8
FEATURE [Part::Box] Box1031  label="Krychle1031"
  AttacherType = Attacher::AttachEngine3D
  Height = 2
  Length = 6
  Placement = pos=(27.1212,33.5028,5) rot=(0,0,1;2.53073rad)
  Width = 8
FEATURE [Part::Box] Box1032  label="Krychle1032"
  AttacherType = Attacher::AttachEngine3D
  Height = 2
  Length = 6
  Placement = pos=(3,43,5) rot=(0,0,1;3.14159rad)
  Width = 8
FEATURE [Part::Box] Box1033  label="Krychle1033"
  AttacherType = Attacher::AttachEngine3D
  Height = 2
  Length = 6
  Placement = pos=(-28.2843,32.5269,5) rot=(0,0,1;3.92699rad)
  Width = 8
FEATURE [Part::Box] Box1034  label="Krychle1034"
  AttacherType = Attacher::AttachEngine3D
  Height = 2
  Length = 6
  Placement = pos=(-43,3,5) rot=(0,0,-1;1.5708rad)
  Width = 8
FEATURE [Part::Box] Box1035  label="Krychle1035"
  AttacherType = Attacher::AttachEngine3D
  Height = 2
  Length = 6
  Placement = pos=(-32.5269,-28.2843,5) rot=(0,0,-1;0.785398rad)
  Width = 8
FEATURE [Part::Compound] Compound1121
  Links = -> [Box1027,Box1028,Box1029,Box1031,Box1032,Box1033,Box1034,Box1035]
  Placement = pos=(0,0,16) rot=(0,0,1;0rad)
FEATURE [Part::Cylinder] Cylinder2128  label="Válec2128"
  Angle = 360
  AttacherType = Attacher::AttachEngine3D
  Height = 100
  Placement = pos=(26.8701,-26.8701,0) rot=(0,0,1;0.785398rad)
  Radius = 1.5
FEATURE [Part::Cylinder] Cylinder2129  label="Válec2129"
  Angle = 360
  AttacherType = Attacher::AttachEngine3D
  Height = 100
  Placement = pos=(38,3e-15,0) rot=(0,0,1;1.5708rad)
  Radius = 1.5
FEATURE [Part::Cylinder] Cylinder2130  label="Válec2130"
  Angle = 360
  AttacherType = Attacher::AttachEngine3D
  Height = 100
  Placement = pos=(21.7959,31.1278,0) rot=(0,0,1;2.53073rad)
  Radius = 1.5
FEATURE [Part::Cylinder] Cylinder2131  label="Válec2131"
  Angle = 360
  AttacherType = Attacher::AttachEngine3D
  Height = 100
  Placement = pos=(-1e-15,38,0) rot=(0,0,1;3.14159rad)
  Radius = 1.5
FEATURE [Part::Cylinder] Cylinder2132  label="Válec2132"
  Angle = 360
  AttacherType = Attacher::AttachEngine3D
  Height = 100
  Placement = pos=(-26.8701,26.8701,0) rot=(0,0,1;3.92699rad)
  Radius = 1.5
FEATURE [Part::Cylinder] Cylinder2133  label="Válec2133"
  Angle = 360
  AttacherType = Attacher::AttachEngine3D
  Height = 100
  Placement = pos=(-38,-6e-15,0) rot=(0,0,-1;1.5708rad)
  Radius = 1.5
FEATURE [Part::Cylinder] Cylinder2134  label="Válec2134"
  Angle = 360
  AttacherType = Attacher::AttachEngine3D
  Height = 100
  Placement = pos=(-26.8701,-26.8701,0) rot=(0,0,-1;0.785398rad)
  Radius = 1.5
FEATURE [Part::Cylinder] Cylinder2135  label="Válec2135"
  Angle = 360
  AttacherType = Attacher::AttachEngine3D
  Height = 100
  Placement = pos=(0,-38,0) rot=(0,0,1;0rad)
  Radius = 1.5
FEATURE [Part::Cylinder] Cylinder2136  label="Válec2136"
  Angle = 360
  AttacherType = Attacher::AttachEngine3D
  Height = 100
  Placement = pos=(38,3e-15,0) rot=(0,0,1;1.5708rad)
  Radius = 1.5
FEATURE [Part::Cylinder] Cylinder2137  label="Válec2137"
  Angle = 360
  AttacherType = Attacher::AttachEngine3D
  Height = 100
  Placement = pos=(-1e-15,38,0) rot=(0,0,1;3.14159rad)
  Radius = 1.5
FEATURE [Part::Cylinder] Cylinder2138  label="Válec2138"
  Angle = 360
  AttacherType = Attacher::AttachEngine3D
  Height = 100
  Placement = pos=(26.8701,-26.8701,0) rot=(0,0,1;0.785398rad)
  Radius = 1.5
FEATURE [Part::Cylinder] Cylinder2139  label="Válec2139"
  Angle = 360
  AttacherType = Attacher::AttachEngine3D
  Height = 100
  Placement = pos=(21.7959,31.1278,0) rot=(0,0,1;2.53073rad)
  Radius = 1.5
FEATURE [Part::Cylinder] Cylinder2140  label="Válec2140"
  Angle = 360
  AttacherType = Attacher::AttachEngine3D
  Height = 100
  Placement = pos=(-26.8701,26.8701,0) rot=(0,0,1;3.92699rad)
  Radius = 1.5
FEATURE [Part::Cylinder] Cylinder2141  label="Válec2141"
  Angle = 360
  AttacherType = Attacher::AttachEngine3D
  Height = 100
  Placement = pos=(-38,-6e-15,0) rot=(0,0,-1;1.5708rad)
  Radius = 1.5
FEATURE [Part::Cylinder] Cylinder2142  label="Válec2142"
  Angle = 360
  AttacherType = Attacher::AttachEngine3D
  Height = 100
  Placement = pos=(-26.8701,-26.8701,0) rot=(0,0,-1;0.785398rad)
  Radius = 1.5
FEATURE [Part::Compound] Compound1123
  Links = -> [Cylinder2138,Cylinder2136,Cylinder2139,Cylinder2137,Cylinder2140,Cylinder2141,Cylinder2142,Cylinder2135]
FEATURE [Part::Cut] Cut711
  Base = -> Cut708
  Tool = -> Compound1123
FEATURE [Part::Chamfer] Chamfer083
  Base = -> Cut711
  Edges = 1 edges r=1: [Edge3]
FEATURE [Part::Cylinder] Cylinder2143  label="Válec2143"
  Angle = 360
  AttacherType = Attacher::AttachEngine3D
  Height = 100
  Placement = pos=(0,-38,0) rot=(0,0,1;0rad)
  Radius = 1.5
FEATURE [Part::Cylinder] Cylinder2144  label="Válec2144"
  Angle = 360
  AttacherType = Attacher::AttachEngine3D
  Height = 100
  Placement = pos=(26.8701,-26.8701,0) rot=(0,0,1;0.785398rad)
  Radius = 1.5
FEATURE [Part::Cylinder] Cylinder2145  label="Válec2145"
  Angle = 360
  AttacherType = Attacher::AttachEngine3D
  Height = 100
  Placement = pos=(38,3e-15,0) rot=(0,0,1;1.5708rad)
  Radius = 1.5
FEATURE [Part::Cylinder] Cylinder2146  label="Válec2146"
  Angle = 360
  AttacherType = Attacher::AttachEngine3D
  Height = 100
  Placement = pos=(21.7959,31.1278,0) rot=(0,0,1;2.53073rad)
  Radius = 1.5
FEATURE [Part::Cylinder] Cylinder2147  label="Válec2147"
  Angle = 360
  AttacherType = Attacher::AttachEngine3D
  Height = 100
  Placement = pos=(-1e-15,38,0) rot=(0,0,1;3.14159rad)
  Radius = 1.5
FEATURE [Part::Cylinder] Cylinder2148  label="Válec2148"
  Angle = 360
  AttacherType = Attacher::AttachEngine3D
  Height = 100
  Placement = pos=(-26.8701,26.8701,0) rot=(0,0,1;3.92699rad)
  Radius = 1.5
FEATURE [Part::Cylinder] Cylinder2149  label="Válec2149"
  Angle = 360
  AttacherType = Attacher::AttachEngine3D
  Height = 100
  Placement = pos=(-38,-6e-15,0) rot=(0,0,-1;1.5708rad)
  Radius = 1.5
FEATURE [Part::Cylinder] Cylinder2150  label="Válec2150"
  Angle = 360
  AttacherType = Attacher::AttachEngine3D
  Height = 100
  Placement = pos=(-26.8701,-26.8701,0) rot=(0,0,-1;0.785398rad)
  Radius = 1.5
FEATURE [Part::Compound] Compound1125
  Links = -> [Cylinder2144,Cylinder2145,Cylinder2146,Cylinder2147,Cylinder2148,Cylinder2149,Cylinder2150,Cylinder2143]
FEATURE [Part::Cylinder] Cylinder2151  label="Válec2151"
  Angle = 360
  AttacherType = Attacher::AttachEngine3D
  Height = 20
  Placement = pos=(0,0,91) rot=(0,0,1;0rad)
  Radius = 32
FEATURE [Part::FeaturePython] wormgear024  # WARN: FeaturePython — macro-defined, semantics opaque (R4)
  AttacherType = Attacher::AttachEngine3D
  Placement = pos=(0,0,100) rot=(0,0,1;0rad)
  beta = 45
  clearance = 0.25
  diameter = 120
  head = 0
  height = 5
  module = 1.5
  pressure_angle = 20
  reverse_pitch = true
  teeth = 80
  version = 0.0.3
FEATURE [Part::Cut] Cut713
  Base = -> wormgear024
  Placement = pos=(0,0,-63) rot=(0,0,1;0rad)
  Tool = -> Cylinder2151
FEATURE [Part::FeaturePython] wormgear025  # WARN: FeaturePython — macro-defined, semantics opaque (R4)
  AttacherType = Attacher::AttachEngine3D
  Placement = pos=(0,0,95) rot=(0,0,1;0.073827rad)
  beta = 45
  clearance = 0.25
  diameter = 120
  head = 0
  height = 5
  module = 1.5
  pressure_angle = 20
  reverse_pitch = false
  teeth = 80
  version = 0.0.3
FEATURE [Part::Cylinder] Cylinder2152  label="Válec2152"
  Angle = 360
  AttacherType = Attacher::AttachEngine3D
  Height = 20
  Placement = pos=(0,0,91) rot=(0,0,1;0rad)
  Radius = 32
FEATURE [Part::Cut] Cut714
  Base = -> wormgear025
  Placement = pos=(0,0,-63) rot=(0,0,1;0rad)
  Tool = -> Cylinder2152
FEATURE [Part::Cylinder] Cylinder2153  label="Válec2153"
  Angle = 360
  AttacherType = Attacher::AttachEngine3D
  Height = 100
  Placement = pos=(26.8701,-26.8701,0) rot=(0,0,1;0.785398rad)
  Radius = 1.5
FEATURE [Part::Cylinder] Cylinder2154  label="Válec2154"
  Angle = 360
  AttacherType = Attacher::AttachEngine3D
  Height = 100
  Placement = pos=(0,-38,0) rot=(0,0,1;0rad)
  Radius = 1.5
FEATURE [Part::Cylinder] Cylinder2155  label="Válec2155"
  Angle = 360
  AttacherType = Attacher::AttachEngine3D
  Height = 100
  Placement = pos=(38,3e-15,0) rot=(0,0,1;1.5708rad)
  Radius = 1.5
FEATURE [Part::Cylinder] Cylinder2156  label="Válec2156"
  Angle = 360
  AttacherType = Attacher::AttachEngine3D
  Height = 100
  Placement = pos=(21.7959,31.1278,0) rot=(0,0,1;2.53073rad)
  Radius = 1.5
FEATURE [Part::Cylinder] Cylinder2157  label="Válec2157"
  Angle = 360
  AttacherType = Attacher::AttachEngine3D
  Height = 100
  Placement = pos=(-1e-15,38,0) rot=(0,0,1;3.14159rad)
  Radius = 1.5
FEATURE [Part::Cylinder] Cylinder2158  label="Válec2158"
  Angle = 360
  AttacherType = Attacher::AttachEngine3D
  Height = 100
  Placement = pos=(-26.8701,26.8701,0) rot=(0,0,1;3.92699rad)
  Radius = 1.5
FEATURE [Part::Cylinder] Cylinder2159  label="Válec2159"
  Angle = 360
  AttacherType = Attacher::AttachEngine3D
  Height = 100
  Placement = pos=(-38,-6e-15,0) rot=(0,0,-1;1.5708rad)
  Radius = 1.5
FEATURE [Part::Cylinder] Cylinder2160  label="Válec2160"
  Angle = 360
  AttacherType = Attacher::AttachEngine3D
  Height = 100
  Placement = pos=(-26.8701,-26.8701,0) rot=(0,0,-1;0.785398rad)
  Radius = 1.5
FEATURE [Part::Compound] Compound1126
  Links = -> [Cylinder2153,Cylinder2155,Cylinder2156,Cylinder2157,Cylinder2158,Cylinder2159,Cylinder2160,Cylinder2154]
FEATURE [Part::Cylinder] Cylinder2161  label="Válec2161"
  Angle = 360
  AttacherType = Attacher::AttachEngine3D
  Height = 100
  Placement = pos=(26.8701,-26.8701,0) rot=(0,0,1;0.785398rad)
  Radius = 1.5
FEATURE [Part::Cylinder] Cylinder2162  label="Válec2162"
  Angle = 360
  AttacherType = Attacher::AttachEngine3D
  Height = 100
  Placement = pos=(0,-38,0) rot=(0,0,1;0rad)
  Radius = 1.5
FEATURE [Part::Cylinder] Cylinder2163  label="Válec2163"
  Angle = 360
  AttacherType = Attacher::AttachEngine3D
  Height = 100
  Placement = pos=(38,3e-15,0) rot=(0,0,1;1.5708rad)
  Radius = 1.5
FEATURE [Part::Cylinder] Cylinder2164  label="Válec2164"
  Angle = 360
  AttacherType = Attacher::AttachEngine3D
  Height = 100
  Placement = pos=(21.7959,31.1278,0) rot=(0,0,1;2.53073rad)
  Radius = 1.5
FEATURE [Part::Cylinder] Cylinder2165  label="Válec2165"
  Angle = 360
  AttacherType = Attacher::AttachEngine3D
  Height = 100
  Placement = pos=(-1e-15,38,0) rot=(0,0,1;3.14159rad)
  Radius = 1.5
FEATURE [Part::Cylinder] Cylinder2166  label="Válec2166"
  Angle = 360
  AttacherType = Attacher::AttachEngine3D
  Height = 100
  Placement = pos=(-26.8701,26.8701,0) rot=(0,0,1;3.92699rad)
  Radius = 1.5
FEATURE [Part::Cylinder] Cylinder2167  label="Válec2167"
  Angle = 360
  AttacherType = Attacher::AttachEngine3D
  Height = 100
  Placement = pos=(-38,-6e-15,0) rot=(0,0,-1;1.5708rad)
  Radius = 1.5
FEATURE [Part::Cylinder] Cylinder2168  label="Válec2168"
  Angle = 360
  AttacherType = Attacher::AttachEngine3D
  Height = 100
  Placement = pos=(-26.8701,-26.8701,0) rot=(0,0,-1;0.785398rad)
  Radius = 1.5
FEATURE [Part::Compound] Compound1127
  Links = -> [Cylinder2161,Cylinder2163,Cylinder2164,Cylinder2165,Cylinder2166,Cylinder2167,Cylinder2168,Cylinder2162]
FEATURE [Part::FeaturePython] Tube089  # WARN: FeaturePython — macro-defined, semantics opaque (R4)
  AttacherType = Attacher::AttachEngine3D
  Height = 1
  InnerRadius = 32
  OuterRadius = 58
  Placement = pos=(0,0,42) rot=(0,0,1;0rad)
FEATURE [Part::Cut] Cut715
  Base = -> Tube089
  Tool = -> Compound1127
FEATURE [Part::Cut] Cut716
  Base = -> Cut714
  Tool = -> Compound1126
FEATURE [Part::Cut] Cut717
  Base = -> Cut713
  Tool = -> Compound1125
FEATURE [Part::Compound] Compound1128  label="Base_super-gear"
  Links = -> [Cut715,Cut716,Cut717]
FEATURE [Mesh::Feature] Mesh001  label="Base_super-gear (Meshed)"
FEATURE [Part::FeaturePython] Tube090  # WARN: FeaturePython — macro-defined, semantics opaque (R4)
  AttacherType = Attacher::AttachEngine3D
  Height = 7
  InnerRadius = 53
  OuterRadius = 54.4
  Placement = pos=(0,0,-22) rot=(0,0,1;0rad)
FEATURE [Part::Box] Box1036  label="Krychle1036"
  AttacherType = Attacher::AttachEngine3D
  Height = 7
  Length = 60
  Placement = pos=(0,0,-22) rot=(0,0,-1;0.034907rad)
  Width = 60
FEATURE [Part::FeaturePython] Tube091  # WARN: FeaturePython — macro-defined, semantics opaque (R4)
  AttacherType = Attacher::AttachEngine3D
  Height = 7
  InnerRadius = 52
  OuterRadius = 53.4
  Placement = pos=(0,0,-22) rot=(0,0,1;0rad)
FEATURE [Part::FeaturePython] Tube092  # WARN: FeaturePython — macro-defined, semantics opaque (R4)
  AttacherType = Attacher::AttachEngine3D
  Height = 10
  InnerRadius = 32
  OuterRadius = 57
  Placement = pos=(0,0,42) rot=(0,0,1;0rad)
FEATURE [Part::Box] Box1037  label="Krychle1037"
  AttacherType = Attacher::AttachEngine3D
  Height = 7
  Length = 120
  Placement = pos=(-60,-60,-22) rot=(0,0,-1;0rad)
  Width = 60
FEATURE [Part::Cut] Cut718
  Base = -> Tube091
  Tool = -> Box1037
FEATURE [Part::Box] Box1038  label="Krychle1038"
  AttacherType = Attacher::AttachEngine3D
  Height = 7
  Length = 60
  Placement = pos=(-59.9909,-1.04714,-22) rot=(0,0,1;0.017453rad)
  Width = 60
FEATURE [Part::Compound] Compound1130
  Links = -> [Box1036,Box1038]
FEATURE [Part::Box] Box1039  label="Krychle1039"
  AttacherType = Attacher::AttachEngine3D
  Height = 7
  Length = 60
  Placement = pos=(0,0,-22) rot=(0,0,-1;0.349066rad)
  Width = 60
FEATURE [Part::Cylinder] Cylinder2170  label="Válec2170"
  Angle = 360
  AttacherType = Attacher::AttachEngine3D
  Height = 7
  Placement = pos=(0,0,-22) rot=(0,0,1;0rad)
  Radius = 51
FEATURE [Part::Box] Box1040  label="Krychle1040"
  AttacherType = Attacher::AttachEngine3D
  Height = 7
  Length = 1.4
  Placement = pos=(0,0,-22) rot=(0,0,-1;0.034907rad)
  Width = 60
FEATURE [Part::Box] Box1041  label="Krychle1041"
  AttacherType = Attacher::AttachEngine3D
  Height = 7
  Length = 60
  Placement = pos=(-56.3816,-20.5212,-22) rot=(0,0,1;0.349066rad)
  Width = 60
FEATURE [Part::Compound] Compound1129
  Links = -> [Box1039,Box1041]
FEATURE [Part::Cut] Cut724
  Base = -> Cut718
  Placement = pos=(0,0,-7) rot=(0,0,1;0rad)
  Tool = -> Compound1129
FEATURE [Part::Box] Box1042  label="Krychle1042"
  AttacherType = Attacher::AttachEngine3D
  Height = 7
  Length = 1.4
  Placement = pos=(0,0,-22) rot=(0,0,1;0.047124rad)
  Width = 60
FEATURE [Part::Box] Box1043  label="Krychle1043"
  AttacherType = Attacher::AttachEngine3D
  Height = 7
  Length = 120
  Placement = pos=(-60,-60,-22) rot=(0,0,-1;0rad)
  Width = 60
FEATURE [Part::Cut] Cut726
  Base = -> Tube090
  Tool = -> Box1043
FEATURE [Part::Cut] Cut723
  Base = -> Cut726
  Placement = pos=(0,0,-7) rot=(0,0,1;0rad)
  Tool = -> Compound1130
FEATURE [Part::Cut] Cut721
  Base = -> Cut724
  Placement = pos=(0,0,74) rot=(0,0,1;0.785398rad)
  Tool = -> Cut723
FEATURE [Part::Compound] Compound1131
  Links = -> [Box1040,Box1042]
FEATURE [Part::Cut] Cut722
  Base = -> Compound1131
  Placement = pos=(0,0,67) rot=(0,0,1;0.785398rad)
  Tool = -> Cylinder2170
FEATURE [Part::Compound] Compound1132
  Links = -> [Cylinder2128,Cylinder2129,Cylinder2130,Cylinder2131,Cylinder2132,Cylinder2133,Cylinder2134,Cylinder2127]
FEATURE [Part::Cut] Cut725
  Base = -> Tube092
  Tool = -> Compound1132
FEATURE [Part::Cut] Cut719
  Base = -> Cut725
  Tool = -> Cut722
FEATURE [Part::Cut] Cut720
  Base = -> Cut719
  Tool = -> Cut721
FEATURE [Part::Cylinder] Cylinder2171  label="Válec2171"
  Angle = 360
  AttacherType = Attacher::AttachEngine3D
  Height = 7
  Placement = pos=(0,0,-22) rot=(0,0,1;0rad)
  Radius = 51
FEATURE [Part::Box] Box1044  label="Krychle1044"
  AttacherType = Attacher::AttachEngine3D
  Height = 7
  Length = 1.4
  Placement = pos=(0,0,-22) rot=(0,0,-1;0.314159rad)
  Width = 60
FEATURE [Part::Box] Box1045  label="Krychle1045"
  AttacherType = Attacher::AttachEngine3D
  Height = 7
  Length = 1.4
  Placement = pos=(0,0,-22) rot=(0,0,1;0.34383rad)
  Width = 60
FEATURE [Part::Compound] Compound1133
  Links = -> [Box1044,Box1045]
FEATURE [Part::Cut] Cut727
  Base = -> Compound1133
  Placement = pos=(0,0,67) rot=(0,0,1;0.785398rad)
  Tool = -> Cylinder2171
FEATURE [Part::Cylinder] Cylinder2172  label="Válec2172"
  Angle = 360
  AttacherType = Attacher::AttachEngine3D
  Height = 7
  Placement = pos=(0,0,45) rot=(0,0,1;0rad)
  Radius = 56
FEATURE [Part::Common] Common
  Base = -> Cut727
  Tool = -> Cylinder2172
FEATURE [Part::Cut] Cut728
  Base = -> Cut720
  Tool = -> Common
FEATURE [Part::FeaturePython] Tube093  # WARN: FeaturePython — macro-defined, semantics opaque (R4)
  AttacherType = Attacher::AttachEngine3D
  Height = 3
  InnerRadius = 54
  OuterRadius = 61
  Placement = pos=(0,0,42) rot=(0,0,1;0rad)
FEATURE [Part::Chamfer] Chamfer084
  Base = -> Tube093
  Edges = 1 edges r=1: [Edge1]
FEATURE [Part::Compound] Compound1134  label="Base_inner-cylinder-belt-A-old"
  Links = -> [Cut728,Chamfer084]
  Placement = pos=(0,0,1) rot=(0,0,1;0rad)
FEATURE [Sketcher::SketchObject] Sketch004
  FullyConstrained = false
  sketch-geometry (1):
    g0: Circle CenterX=-186.411 CenterY=73.9277 CenterZ=0 NormalX=0 NormalY=0 NormalZ=1 AngleXU=0 Radius=59
FEATURE [Part::Extrusion] Extrude002
  Base = -> Sketch004
  Dir = (52,0,32)
  DirMode = 0
  FaceMakerClass = Part::FaceMakerBullseye
  LengthFwd = 61
  LengthRev = 0
  Placement = pos=(-134,74,-22) rot=(0,0,1;3.14159rad)
  Solid = true
  Symmetric = false
FEATURE [Part::Cylinder] Cylinder1256  label="Válec1256"
  Angle = 360
  AttacherType = Attacher::AttachEngine3D
  Height = 100
  Placement = pos=(16,34,-90) rot=(0,0,1;0rad)
  Radius = 4
FEATURE [Part::Cylinder] Cylinder1257  label="Válec1257"
  Angle = 360
  AttacherType = Attacher::AttachEngine3D
  Height = 100
  Placement = pos=(-34,-16,-90) rot=(0,0,1;0rad)
  Radius = 4
FEATURE [Part::Cylinder] Cylinder1258  label="Válec1258"
  Angle = 360
  AttacherType = Attacher::AttachEngine3D
  Height = 100
  Placement = pos=(-16,34,-90) rot=(0,0,1;0rad)
  Radius = 4
FEATURE [Part::Cylinder] Cylinder1259  label="Válec1259"
  Angle = 360
  AttacherType = Attacher::AttachEngine3D
  Height = 100
  Placement = pos=(-16,-34,-90) rot=(0,0,1;0rad)
  Radius = 4
FEATURE [Part::Cylinder] Cylinder1260  label="Válec1260"
  Angle = 360
  AttacherType = Attacher::AttachEngine3D
  Height = 100
  Placement = pos=(34,-16,-90) rot=(0,0,1;0rad)
  Radius = 4
FEATURE [Part::Cylinder] Cylinder1261  label="Válec1261"
  Angle = 360
  AttacherType = Attacher::AttachEngine3D
  Height = 100
  Placement = pos=(10,-36,-90) rot=(0,0,1;0rad)
  Radius = 4
FEATURE [Part::Cylinder] Cylinder1262  label="Válec1262"
  Angle = 360
  AttacherType = Attacher::AttachEngine3D
  Height = 100
  Placement = pos=(16,34,-60) rot=(0,0,1;0rad)
  Radius = 1.5
FEATURE [Part::Cylinder] Cylinder1263  label="Válec1263"
  Angle = 360
  AttacherType = Attacher::AttachEngine3D
  Height = 100
  Placement = pos=(-34,16,-60) rot=(0,0,1;0rad)
  Radius = 1.5
FEATURE [Part::Cylinder] Cylinder1264  label="Válec1264"
  Angle = 360
  AttacherType = Attacher::AttachEngine3D
  Height = 100
  Placement = pos=(-34,-16,-60) rot=(0,0,1;0rad)
  Radius = 1.5
FEATURE [Part::Cylinder] Cylinder1265  label="Válec1265"
  Angle = 360
  AttacherType = Attacher::AttachEngine3D
  Height = 100
  Placement = pos=(34,-16,-60) rot=(0,0,1;0rad)
  Radius = 1.5
FEATURE [Part::Cylinder] Cylinder1266  label="Válec1266"
  Angle = 360
  AttacherType = Attacher::AttachEngine3D
  Height = 100
  Placement = pos=(34,16,-60) rot=(0,0,1;0rad)
  Radius = 1.5
FEATURE [Part::Cylinder] Cylinder1267  label="Válec1267"
  Angle = 360
  AttacherType = Attacher::AttachEngine3D
  Height = 100
  Placement = pos=(10,-36,-60) rot=(0,0,1;0rad)
  Radius = 1.5
FEATURE [Part::Box] Box240  label="Krychle240"
  AttacherType = Attacher::AttachEngine3D
  Height = 100
  Length = 200
  Placement = pos=(-60,-134,-90) rot=(0,0,1;0rad)
  Width = 100
FEATURE [Part::Box] Box241  label="Krychle241"
  AttacherType = Attacher::AttachEngine3D
  Height = 100
  Length = 200
  Placement = pos=(-60,44,-90) rot=(0,0,1;0rad)
  Width = 100
FEATURE [Part::Cylinder] Cylinder1268  label="Válec1268"
  Angle = 360
  AttacherType = Attacher::AttachEngine3D
  Height = 100
  Placement = pos=(90,0,-60) rot=(0,0,1;0rad)
  Radius = 1.5
FEATURE [Part::Cylinder] Cylinder1269  label="Válec1269"
  Angle = 360
  AttacherType = Attacher::AttachEngine3D
  Height = 100
  Placement = pos=(14,0,-60) rot=(0,0,1;0rad)
  Radius = 1.5
FEATURE [Part::Cylinder] Cylinder1270  label="Válec1270"
  Angle = 360
  AttacherType = Attacher::AttachEngine3D
  Height = 100
  Placement = pos=(90,0,-18) rot=(0,0,1;0rad)
  Radius = 4
FEATURE [Part::Cylinder] Cylinder1271  label="Válec1271"
  Angle = 360
  AttacherType = Attacher::AttachEngine3D
  Height = 100
  Placement = pos=(14,0,-18) rot=(0,0,1;0rad)
  Radius = 4
FEATURE [Part::Compound] Compound669  label="srouby_troj_silne002"
  Links = -> [Cylinder1270,Cylinder1271]
FEATURE [Part::Compound] Compound670  label="srouby_troj002"
  Links = -> [Cylinder1268,Cylinder1269]
FEATURE [Part::Box] Box242  label="Krychle242"
  AttacherType = Attacher::AttachEngine3D
  Height = 2
  Length = 6
  Placement = pos=(75,38,-22) rot=(0,0,1;0rad)
  Width = 6
FEATURE [Part::Box] Box243  label="Krychle243"
  AttacherType = Attacher::AttachEngine3D
  Height = 2
  Length = 6
  Placement = pos=(23,38,-22) rot=(0,0,1;0rad)
  Width = 6
FEATURE [Part::Compound] Compound667
  Links = -> [Box242,Box243]
FEATURE [Part::Cylinder] Cylinder1272  label="Válec1272"
  Angle = 360
  AttacherType = Attacher::AttachEngine3D
  Height = 32
  Placement = pos=(26,41,-46) rot=(0,0,1;0rad)
  Radius = 1.5
FEATURE [Part::Cylinder] Cylinder1273  label="Válec1273"
  Angle = 360
  AttacherType = Attacher::AttachEngine3D
  Height = 32
  Placement = pos=(78,41,-46) rot=(0,0,1;0rad)
  Radius = 1.5
FEATURE [Part::Compound] Compound668
  Links = -> [Cylinder1272,Cylinder1273]
FEATURE [Part::Cylinder] Cylinder1274  label="Válec1274"
  Angle = 360
  AttacherType = Attacher::AttachEngine3D
  Height = 100
  Placement = pos=(-34,16,-90) rot=(0,0,1;0rad)
  Radius = 4
FEATURE [Part::Cylinder] Cylinder1275  label="Válec1275"
  Angle = 360
  AttacherType = Attacher::AttachEngine3D
  Height = 100
  Placement = pos=(34,16,-90) rot=(0,0,1;0rad)
  Radius = 4
FEATURE [Part::Compound] Compound665  label="sbouby_baze_silne003"
  Links = -> [Cylinder1257,Cylinder1258,Cylinder1259,Cylinder1260,Cylinder1256,Cylinder1261,Cylinder1274,Cylinder1275]
FEATURE [Part::Cylinder] Cylinder1292  label="Válec1292"
  Angle = 360
  AttacherType = Attacher::AttachEngine3D
  Height = 100
  Placement = pos=(-16,-34,-60) rot=(0,0,1;0rad)
  Radius = 1.5
FEATURE [Part::Cylinder] Cylinder1293  label="Válec1293"
  Angle = 360
  AttacherType = Attacher::AttachEngine3D
  Height = 100
  Placement = pos=(-16,34,-60) rot=(0,0,1;0rad)
  Radius = 1.5
FEATURE [Part::Compound] Compound666  label="sbouby_baze002"
  Links = -> [Cylinder1263,Cylinder1264,Cylinder1265,Cylinder1266,Cylinder1262,Cylinder1267,Cylinder1292,Cylinder1293]
FEATURE [Part::Cylinder] Cylinder1294  label="Válec1294"
  Angle = 360
  AttacherType = Attacher::AttachEngine3D
  Height = 100
  Placement = pos=(-34,16,-60) rot=(0,0,1;0rad)
  Radius = 1.5
FEATURE [Part::Cylinder] Cylinder1295  label="Válec1295"
  Angle = 360
  AttacherType = Attacher::AttachEngine3D
  Height = 100
  Placement = pos=(-34,-16,-60) rot=(0,0,1;0rad)
  Radius = 1.5
FEATURE [Part::Cylinder] Cylinder1296  label="Válec1296"
  Angle = 360
  AttacherType = Attacher::AttachEngine3D
  Height = 100
  Placement = pos=(34,-16,-60) rot=(0,0,1;0rad)
  Radius = 1.5
FEATURE [Part::Cylinder] Cylinder1297  label="Válec1297"
  Angle = 360
  AttacherType = Attacher::AttachEngine3D
  Height = 100
  Placement = pos=(34,16,-60) rot=(0,0,1;0rad)
  Radius = 1.5
FEATURE [Part::Cylinder] Cylinder1298  label="Válec1298"
  Angle = 360
  AttacherType = Attacher::AttachEngine3D
  Height = 100
  Placement = pos=(16,34,-60) rot=(0,0,1;0rad)
  Radius = 1.5
FEATURE [Part::Cylinder] Cylinder1299  label="Válec1299"
  Angle = 360
  AttacherType = Attacher::AttachEngine3D
  Height = 100
  Placement = pos=(10,-36,-60) rot=(0,0,1;0rad)
  Radius = 1.5
FEATURE [Part::Cylinder] Cylinder1300  label="Válec1300"
  Angle = 360
  AttacherType = Attacher::AttachEngine3D
  Height = 100
  Placement = pos=(-16,-34,-60) rot=(0,0,1;0rad)
  Radius = 1.5
FEATURE [Part::Cylinder] Cylinder1301  label="Válec1301"
  Angle = 360
  AttacherType = Attacher::AttachEngine3D
  Height = 100
  Placement = pos=(-16,34,-60) rot=(0,0,1;0rad)
  Radius = 1.5
FEATURE [Part::Compound] Compound671  label="sbouby_baze003"
  Links = -> [Cylinder1294,Cylinder1295,Cylinder1296,Cylinder1297,Cylinder1298,Cylinder1299,Cylinder1300,Cylinder1301]
FEATURE [Part::Cylinder] Cylinder1308  label="Válec1308"
  Angle = 360
  AttacherType = Attacher::AttachEngine3D
  Height = 16
  Placement = pos=(0,0,2) rot=(0,0,1;0rad)
  Radius = 59
FEATURE [Part::Cylinder] Cylinder1309  label="Válec1309"
  Angle = 360
  AttacherType = Attacher::AttachEngine3D
  Height = 20
  Placement = pos=(103,-12,-20) rot=(0,0,1;0rad)
  Radius = 4
FEATURE [Part::Cylinder] Cylinder1310  label="Válec1310"
  Angle = 360
  AttacherType = Attacher::AttachEngine3D
  Height = 20
  Placement = pos=(103,12,-20) rot=(0,0,1;0rad)
  Radius = 4
FEATURE [Part::Cylinder] Cylinder1311  label="Válec1311"
  Angle = 360
  AttacherType = Attacher::AttachEngine3D
  Height = 20
  Placement = pos=(76,24,-18) rot=(0,0,1;0rad)
  Radius = 4
FEATURE [Part::Cylinder] Cylinder1312  label="Válec1312"
  Angle = 360
  AttacherType = Attacher::AttachEngine3D
  Height = 20
  Placement = pos=(91,-27,-18) rot=(0,0,1;0rad)
  Radius = 4
FEATURE [Part::Cylinder] Cylinder1313  label="Válec1313"
  Angle = 360
  AttacherType = Attacher::AttachEngine3D
  Height = 40
  Placement = pos=(13,-27,-18) rot=(0,0,1;0rad)
  Radius = 4
FEATURE [Part::Cylinder] Cylinder1314  label="Válec1314"
  Angle = 360
  AttacherType = Attacher::AttachEngine3D
  Height = 40
  Placement = pos=(28,24,-18) rot=(0,0,1;0rad)
  Radius = 4
FEATURE [Part::Cylinder] Cylinder1315  label="Válec1315"
  Angle = 360
  AttacherType = Attacher::AttachEngine3D
  Height = 40
  Placement = pos=(1,-12,-18) rot=(0,0,1;0rad)
  Radius = 4
FEATURE [Part::Cylinder] Cylinder1316  label="Válec1316"
  Angle = 360
  AttacherType = Attacher::AttachEngine3D
  Height = 40
  Placement = pos=(1,12,-18) rot=(0,0,1;0rad)
  Radius = 4
FEATURE [Part::Compound] Compound672  label="srouby_monoblok_silne006"
  Links = -> [Cylinder1309,Cylinder1310,Cylinder1311,Cylinder1312,Cylinder1313,Cylinder1314,Cylinder1315,Cylinder1316]
FEATURE [Part::Cut] Cut305
  Base = -> Cylinder1308
  Tool = -> Compound672
FEATURE [Part::Cylinder] Cylinder1317  label="Válec1317"
  Angle = 360
  AttacherType = Attacher::AttachEngine3D
  Height = 100
  Placement = pos=(90,0,-18) rot=(0,0,1;0rad)
  Radius = 4
FEATURE [Part::Cylinder] Cylinder1318  label="Válec1318"
  Angle = 360
  AttacherType = Attacher::AttachEngine3D
  Height = 100
  Placement = pos=(14,0,-18) rot=(0,0,1;0rad)
  Radius = 4
FEATURE [Part::Compound] Compound674  label="srouby_troj_silne003"
  Links = -> [Cylinder1317,Cylinder1318]
FEATURE [Part::Cylinder] Cylinder1319  label="Válec1319"
  Angle = 360
  AttacherType = Attacher::AttachEngine3D
  Height = 100
  Placement = pos=(-16,-34,-90) rot=(0,0,1;0rad)
  Radius = 4
FEATURE [Part::Cylinder] Cylinder1320  label="Válec1320"
  Angle = 360
  AttacherType = Attacher::AttachEngine3D
  Height = 100
  Placement = pos=(-34,-16,-90) rot=(0,0,1;0rad)
  Radius = 4
FEATURE [Part::Cylinder] Cylinder1321  label="Válec1321"
  Angle = 360
  AttacherType = Attacher::AttachEngine3D
  Height = 100
  Placement = pos=(-16,34,-90) rot=(0,0,1;0rad)
  Radius = 4
FEATURE [Part::Cylinder] Cylinder1322  label="Válec1322"
  Angle = 360
  AttacherType = Attacher::AttachEngine3D
  Height = 100
  Placement = pos=(34,-16,-90) rot=(0,0,1;0rad)
  Radius = 4
FEATURE [Part::Cylinder] Cylinder1323  label="Válec1323"
  Angle = 360
  AttacherType = Attacher::AttachEngine3D
  Height = 100
  Placement = pos=(16,34,-90) rot=(0,0,1;0rad)
  Radius = 4
FEATURE [Part::Cylinder] Cylinder1324  label="Válec1324"
  Angle = 360
  AttacherType = Attacher::AttachEngine3D
  Height = 100
  Placement = pos=(10,-36,-90) rot=(0,0,1;0rad)
  Radius = 4
FEATURE [Part::Cylinder] Cylinder1325  label="Válec1325"
  Angle = 360
  AttacherType = Attacher::AttachEngine3D
  Height = 100
  Placement = pos=(-34,16,-90) rot=(0,0,1;0rad)
  Radius = 4
FEATURE [Part::Cylinder] Cylinder1326  label="Válec1326"
  Angle = 360
  AttacherType = Attacher::AttachEngine3D
  Height = 100
  Placement = pos=(34,16,-90) rot=(0,0,1;0rad)
  Radius = 4
FEATURE [Part::Compound] Compound673  label="sbouby_baze_silne004"
  Links = -> [Cylinder1320,Cylinder1321,Cylinder1319,Cylinder1322,Cylinder1323,Cylinder1324,Cylinder1325,Cylinder1326]
FEATURE [Part::Cut] Cut306
  Base = -> Cut305
  Tool = -> Compound673
FEATURE [Part::Cut] Cut307
  Base = -> Cut306
  Tool = -> Compound671
FEATURE [Part::Chamfer] Chamfer038
  Base = -> Cut307
  Edges = 1 edges r=4: [Edge3]
FEATURE [Part::Cut] Cut308
  Base = -> Chamfer038
  Placement = pos=(0,0,4) rot=(0,0,1;0rad)
  Tool = -> Compound674
FEATURE [Part::Cylinder] Cylinder1438  label="Válec1438"
  Angle = 360
  AttacherType = Attacher::AttachEngine3D
  Height = 100
  Placement = pos=(103,-12,-60) rot=(0,0,1;0rad)
  Radius = 1.5
FEATURE [Part::Cylinder] Cylinder1439  label="Válec1439"
  Angle = 360
  AttacherType = Attacher::AttachEngine3D
  Height = 100
  Placement = pos=(103,12,-60) rot=(0,0,1;0rad)
  Radius = 1.5
FEATURE [Part::Cylinder] Cylinder1440  label="Válec1440"
  Angle = 360
  AttacherType = Attacher::AttachEngine3D
  Height = 100
  Placement = pos=(76,24,-60) rot=(0,0,1;0rad)
  Radius = 1.5
FEATURE [Part::Cylinder] Cylinder1441  label="Válec1441"
  Angle = 360
  AttacherType = Attacher::AttachEngine3D
  Height = 100
  Placement = pos=(91,-27,-60) rot=(0,0,1;0rad)
  Radius = 1.5
FEATURE [Part::Cylinder] Cylinder1442  label="Válec1442"
  Angle = 360
  AttacherType = Attacher::AttachEngine3D
  Height = 100
  Placement = pos=(13,-27,-60) rot=(0,0,1;0rad)
  Radius = 1.5
FEATURE [Part::Cylinder] Cylinder1443  label="Válec1443"
  Angle = 360
  AttacherType = Attacher::AttachEngine3D
  Height = 100
  Placement = pos=(28,24,-60) rot=(0,0,1;0rad)
  Radius = 1.5
FEATURE [Part::Cylinder] Cylinder1444  label="Válec1444"
  Angle = 360
  AttacherType = Attacher::AttachEngine3D
  Height = 100
  Placement = pos=(1,-12,-60) rot=(0,0,1;0rad)
  Radius = 1.5
FEATURE [Part::Cylinder] Cylinder1445  label="Válec1445"
  Angle = 360
  AttacherType = Attacher::AttachEngine3D
  Height = 100
  Placement = pos=(1,12,-60) rot=(0,0,1;0rad)
  Radius = 1.5
FEATURE [Part::Compound] Compound663  label="srouby_monoblok002"
  Links = -> [Cylinder1438,Cylinder1439,Cylinder1440,Cylinder1441,Cylinder1442,Cylinder1443,Cylinder1444,Cylinder1445]
FEATURE [Part::Cut] Cut296
  Base = -> Extrude002
  Tool = -> Compound663
FEATURE [Part::Cylinder] Cylinder2173  label="Válec2173"
  Angle = 360
  AttacherType = Attacher::AttachEngine3D
  Height = 20
  Placement = pos=(103,-12,-20) rot=(0,0,1;0rad)
  Radius = 4
FEATURE [Part::Cylinder] Cylinder2174  label="Válec2174"
  Angle = 360
  AttacherType = Attacher::AttachEngine3D
  Height = 20
  Placement = pos=(103,12,-20) rot=(0,0,1;0rad)
  Radius = 4
FEATURE [Part::Cylinder] Cylinder2175  label="Válec2175"
  Angle = 360
  AttacherType = Attacher::AttachEngine3D
  Height = 20
  Placement = pos=(76,24,-18) rot=(0,0,1;0rad)
  Radius = 4
FEATURE [Part::Cylinder] Cylinder2176  label="Válec2176"
  Angle = 360
  AttacherType = Attacher::AttachEngine3D
  Height = 20
  Placement = pos=(91,-27,-18) rot=(0,0,1;0rad)
  Radius = 4
FEATURE [Part::Cylinder] Cylinder2177  label="Válec2177"
  Angle = 360
  AttacherType = Attacher::AttachEngine3D
  Height = 40
  Placement = pos=(13,-27,-18) rot=(0,0,1;0rad)
  Radius = 4
FEATURE [Part::Cylinder] Cylinder2178  label="Válec2178"
  Angle = 360
  AttacherType = Attacher::AttachEngine3D
  Height = 40
  Placement = pos=(28,24,-18) rot=(0,0,1;0rad)
  Radius = 4
FEATURE [Part::Cylinder] Cylinder2179  label="Válec2179"
  Angle = 360
  AttacherType = Attacher::AttachEngine3D
  Height = 40
  Placement = pos=(1,-12,-18) rot=(0,0,1;0rad)
  Radius = 4
FEATURE [Part::Cylinder] Cylinder2180  label="Válec2180"
  Angle = 360
  AttacherType = Attacher::AttachEngine3D
  Height = 40
  Placement = pos=(1,12,-18) rot=(0,0,1;0rad)
  Radius = 4
FEATURE [Part::Compound] Compound1135  label="srouby_monoblok_silne005"
  Links = -> [Cylinder2173,Cylinder2174,Cylinder2175,Cylinder2176,Cylinder2177,Cylinder2178,Cylinder2179,Cylinder2180]
FEATURE [Part::Cut] Cut295
  Base = -> Cut296
  Tool = -> Compound1135
FEATURE [Part::Cut] Cut297
  Base = -> Cut295
  Tool = -> Compound665
FEATURE [Part::Cut] Cut298
  Base = -> Cut297
  Tool = -> Compound666
FEATURE [Part::Cut] Cut299
  Base = -> Cut298
  Tool = -> Box240
FEATURE [Part::Cut] Cut300
  Base = -> Cut299
  Tool = -> Box241
FEATURE [Part::Cut] Cut301
  Base = -> Cut300
  Tool = -> Compound667
FEATURE [Part::Cut] Cut302
  Base = -> Cut301
  Tool = -> Compound668
FEATURE [Part::Cut] Cut303
  Base = -> Cut302
  Tool = -> Compound670
FEATURE [Part::Cut] Cut304
  Base = -> Cut303
  Tool = -> Compound669
FEATURE [Part::Chamfer] Chamfer085
  Base = -> Cut304
  Edges = 1 edges r=4: [Edge44]
FEATURE [Part::Chamfer] Chamfer039
  Base = -> Chamfer085
  Edges = 2 edges r=3.5: [Edge4,Edge6]
FEATURE [Part::Cylinder] Cylinder1454  label="Válec1454"
  Angle = 360
  AttacherType = Attacher::AttachEngine3D
  Height = 4
  Placement = pos=(52,0,-26) rot=(0,0,1;0rad)
  Radius = 59
FEATURE [Part::Cylinder] Cylinder1455  label="Válec1455"
  Angle = 360
  AttacherType = Attacher::AttachEngine3D
  Height = 100
  Placement = pos=(103,-12,-60) rot=(0,0,1;0rad)
  Radius = 1.5
FEATURE [Part::Cylinder] Cylinder1456  label="Válec1456"
  Angle = 360
  AttacherType = Attacher::AttachEngine3D
  Height = 100
  Placement = pos=(103,12,-60) rot=(0,0,1;0rad)
  Radius = 1.5
FEATURE [Part::Cylinder] Cylinder1457  label="Válec1457"
  Angle = 360
  AttacherType = Attacher::AttachEngine3D
  Height = 100
  Placement = pos=(76,24,-60) rot=(0,0,1;0rad)
  Radius = 1.5
FEATURE [Part::Cylinder] Cylinder1458  label="Válec1458"
  Angle = 360
  AttacherType = Attacher::AttachEngine3D
  Height = 100
  Placement = pos=(91,-27,-60) rot=(0,0,1;0rad)
  Radius = 1.5
FEATURE [Part::Cylinder] Cylinder1459  label="Válec1459"
  Angle = 360
  AttacherType = Attacher::AttachEngine3D
  Height = 100
  Placement = pos=(13,-27,-60) rot=(0,0,1;0rad)
  Radius = 1.5
FEATURE [Part::Cylinder] Cylinder1460  label="Válec1460"
  Angle = 360
  AttacherType = Attacher::AttachEngine3D
  Height = 100
  Placement = pos=(28,24,-60) rot=(0,0,1;0rad)
  Radius = 1.5
FEATURE [Part::Cylinder] Cylinder1461  label="Válec1461"
  Angle = 360
  AttacherType = Attacher::AttachEngine3D
  Height = 100
  Placement = pos=(1,-12,-60) rot=(0,0,1;0rad)
  Radius = 1.5
FEATURE [Part::Cylinder] Cylinder1462  label="Válec1462"
  Angle = 360
  AttacherType = Attacher::AttachEngine3D
  Height = 100
  Placement = pos=(1,12,-60) rot=(0,0,1;0rad)
  Radius = 1.5
FEATURE [Part::Compound] Compound885  label="srouby_monoblok003"
  Links = -> [Cylinder1455,Cylinder1456,Cylinder1457,Cylinder1458,Cylinder1459,Cylinder1460,Cylinder1461,Cylinder1462]
FEATURE [Part::Cut] Cut505
  Base = -> Cylinder1454
  Tool = -> Compound885
FEATURE [Part::Box] Box515  label="Krychle515"
  AttacherType = Attacher::AttachEngine3D
  Height = 100
  Length = 200
  Placement = pos=(-60,-130,-90) rot=(0,0,1;0rad)
  Width = 100
FEATURE [Part::Box] Box516  label="Krychle516"
  AttacherType = Attacher::AttachEngine3D
  Height = 100
  Length = 200
  Placement = pos=(-60,44,-90) rot=(0,0,1;0rad)
  Width = 100
FEATURE [Part::Cylinder] Cylinder1463  label="Válec1463"
  Angle = 360
  AttacherType = Attacher::AttachEngine3D
  Height = 100
  Placement = pos=(-34,-16,-90) rot=(0,0,1;0rad)
  Radius = 4
FEATURE [Part::Cylinder] Cylinder1464  label="Válec1464"
  Angle = 360
  AttacherType = Attacher::AttachEngine3D
  Height = 100
  Placement = pos=(-16,34,-90) rot=(0,0,1;0rad)
  Radius = 4
FEATURE [Part::Cylinder] Cylinder1465  label="Válec1465"
  Angle = 360
  AttacherType = Attacher::AttachEngine3D
  Height = 100
  Placement = pos=(-16,-34,-90) rot=(0,0,1;0rad)
  Radius = 4
FEATURE [Part::Cylinder] Cylinder1466  label="Válec1466"
  Angle = 360
  AttacherType = Attacher::AttachEngine3D
  Height = 100
  Placement = pos=(34,-16,-90) rot=(0,0,1;0rad)
  Radius = 4
FEATURE [Part::Cylinder] Cylinder1467  label="Válec1467"
  Angle = 360
  AttacherType = Attacher::AttachEngine3D
  Height = 100
  Placement = pos=(16,34,-90) rot=(0,0,1;0rad)
  Radius = 4
FEATURE [Part::Cylinder] Cylinder1468  label="Válec1468"
  Angle = 360
  AttacherType = Attacher::AttachEngine3D
  Height = 100
  Placement = pos=(16,-34,-90) rot=(0,0,1;0rad)
  Radius = 4
FEATURE [Part::Cylinder] Cylinder1469  label="Válec1469"
  Angle = 360
  AttacherType = Attacher::AttachEngine3D
  Height = 100
  Placement = pos=(-34,16,-90) rot=(0,0,1;0rad)
  Radius = 4
FEATURE [Part::Cylinder] Cylinder1470  label="Válec1470"
  Angle = 360
  AttacherType = Attacher::AttachEngine3D
  Height = 100
  Placement = pos=(34,16,-90) rot=(0,0,1;0rad)
  Radius = 4
FEATURE [Part::Compound] Compound886  label="sbouby_baze_silne005"
  Links = -> [Cylinder1463,Cylinder1464,Cylinder1465,Cylinder1466,Cylinder1467,Cylinder1468,Cylinder1469,Cylinder1470]
FEATURE [Part::Cut] Cut506
  Base = -> Cut505
  Tool = -> Compound886
FEATURE [Part::Cut] Cut507
  Base = -> Cut506
  Tool = -> Box515
FEATURE [Part::Cut] Cut508
  Base = -> Cut507
  Tool = -> Box516
FEATURE [Part::Cylinder] Cylinder1471  label="Válec1471"
  Angle = 360
  AttacherType = Attacher::AttachEngine3D
  Height = 32
  Placement = pos=(26,41,-42) rot=(0,0,1;0rad)
  Radius = 1.5
FEATURE [Part::Cylinder] Cylinder1472  label="Válec1472"
  Angle = 360
  AttacherType = Attacher::AttachEngine3D
  Height = 32
  Placement = pos=(78,41,-42) rot=(0,0,1;0rad)
  Radius = 1.5
FEATURE [Part::Compound] Compound887
  Links = -> [Cylinder1471,Cylinder1472]
FEATURE [Part::Cut] Cut729
  Base = -> Cut508
  Tool = -> Compound887
FEATURE [Part::Cylinder] Cylinder1473  label="Válec1473"
  Angle = 360
  AttacherType = Attacher::AttachEngine3D
  Height = 100
  Placement = pos=(90,0,-60) rot=(0,0,1;0rad)
  Radius = 1.5
FEATURE [Part::Cylinder] Cylinder1474  label="Válec1474"
  Angle = 360
  AttacherType = Attacher::AttachEngine3D
  Height = 100
  Placement = pos=(14,0,-60) rot=(0,0,1;0rad)
  Radius = 1.5
FEATURE [Part::Compound] Compound888  label="srouby_troj003"
  Links = -> [Cylinder1473,Cylinder1474]
FEATURE [Part::Cut] Cut509
  Base = -> Cut729
  Tool = -> Compound888
FEATURE [Part::Compound] Compound1136  label="Base_deep-neck"
  Links = -> [Chamfer039,Cut308,Cut509]
  Placement = pos=(0,0,-17) rot=(0,0,1;0rad)
FEATURE [Part::FeaturePython] Tube049  label="ZKL-51117A-NF"  # WARN: FeaturePython — macro-defined, semantics opaque (R4)
  AttacherType = Attacher::AttachEngine3D
  Height = 19
  InnerRadius = 42.5
  OuterRadius = 55
  Placement = pos=(0,0,61) rot=(0,0,1;0rad)
FEATURE [Part::FeaturePython] Tube094  # WARN: FeaturePython — macro-defined, semantics opaque (R4)
  AttacherType = Attacher::AttachEngine3D
  Height = 8
  InnerRadius = 32
  OuterRadius = 58
  Placement = pos=(0,0,52) rot=(0,0,1;0rad)
FEATURE [Part::Cylinder] Cylinder2197  label="Válec2197"
  Angle = 360
  AttacherType = Attacher::AttachEngine3D
  Height = 100
  Placement = pos=(0,-38,0) rot=(0,0,1;0rad)
  Radius = 1.5
FEATURE [Part::Cylinder] Cylinder2198  label="Válec2198"
  Angle = 360
  AttacherType = Attacher::AttachEngine3D
  Height = 100
  Placement = pos=(26.8701,-26.8701,0) rot=(0,0,1;0.785398rad)
  Radius = 1.5
FEATURE [Part::Cylinder] Cylinder2199  label="Válec2199"
  Angle = 360
  AttacherType = Attacher::AttachEngine3D
  Height = 100
  Placement = pos=(38,3e-15,0) rot=(0,0,1;1.5708rad)
  Radius = 1.5
FEATURE [Part::Cylinder] Cylinder2200  label="Válec2200"
  Angle = 360
  AttacherType = Attacher::AttachEngine3D
  Height = 100
  Placement = pos=(21.7959,31.1278,0) rot=(0,0,1;2.53073rad)
  Radius = 1.5
FEATURE [Part::Cylinder] Cylinder2201  label="Válec2201"
  Angle = 360
  AttacherType = Attacher::AttachEngine3D
  Height = 100
  Placement = pos=(-1e-15,38,0) rot=(0,0,1;3.14159rad)
  Radius = 1.5
FEATURE [Part::Cylinder] Cylinder2202  label="Válec2202"
  Angle = 360
  AttacherType = Attacher::AttachEngine3D
  Height = 100
  Placement = pos=(-26.8701,26.8701,0) rot=(0,0,1;3.92699rad)
  Radius = 1.5
FEATURE [Part::Cylinder] Cylinder2203  label="Válec2203"
  Angle = 360
  AttacherType = Attacher::AttachEngine3D
  Height = 100
  Placement = pos=(-38,-6e-15,0) rot=(0,0,-1;1.5708rad)
  Radius = 1.5
FEATURE [Part::Cylinder] Cylinder2204  label="Válec2204"
  Angle = 360
  AttacherType = Attacher::AttachEngine3D
  Height = 100
  Placement = pos=(-26.8701,-26.8701,0) rot=(0,0,-1;0.785398rad)
  Radius = 1.5
FEATURE [Part::Compound] Compound1137
  Links = -> [Cylinder2198,Cylinder2199,Cylinder2200,Cylinder2201,Cylinder2202,Cylinder2203,Cylinder2204,Cylinder2197]
FEATURE [Part::Cylinder] Cylinder2205  label="Válec2205"
  Angle = 360
  AttacherType = Attacher::AttachEngine3D
  Height = 100
  Placement = pos=(0,-38,0) rot=(0,0,1;0rad)
  Radius = 5
FEATURE [Part::Cylinder] Cylinder2206  label="Válec2206"
  Angle = 360
  AttacherType = Attacher::AttachEngine3D
  Height = 100
  Placement = pos=(26.8701,-26.8701,0) rot=(0,0,1;0.785398rad)
  Radius = 5
FEATURE [Part::Cylinder] Cylinder2207  label="Válec2207"
  Angle = 360
  AttacherType = Attacher::AttachEngine3D
  Height = 100
  Placement = pos=(38,3e-15,0) rot=(0,0,1;1.5708rad)
  Radius = 5
FEATURE [Part::Cylinder] Cylinder2208  label="Válec2208"
  Angle = 360
  AttacherType = Attacher::AttachEngine3D
  Height = 100
  Placement = pos=(21.7959,31.1278,0) rot=(0,0,1;2.53073rad)
  Radius = 5
FEATURE [Part::Cylinder] Cylinder2209  label="Válec2209"
  Angle = 360
  AttacherType = Attacher::AttachEngine3D
  Height = 100
  Placement = pos=(-1e-15,38,0) rot=(0,0,1;3.14159rad)
  Radius = 5
FEATURE [Part::Cylinder] Cylinder2210  label="Válec2210"
  Angle = 360
  AttacherType = Attacher::AttachEngine3D
  Height = 100
  Placement = pos=(-26.8701,26.8701,0) rot=(0,0,1;3.92699rad)
  Radius = 5
FEATURE [Part::Cylinder] Cylinder2211  label="Válec2211"
  Angle = 360
  AttacherType = Attacher::AttachEngine3D
  Height = 100
  Placement = pos=(-38,-6e-15,0) rot=(0,0,-1;1.5708rad)
  Radius = 5
FEATURE [Part::Cylinder] Cylinder2212  label="Válec2212"
  Angle = 360
  AttacherType = Attacher::AttachEngine3D
  Height = 100
  Placement = pos=(-26.8701,-26.8701,0) rot=(0,0,-1;0.785398rad)
  Radius = 5
FEATURE [Part::Compound] Compound1138
  Links = -> [Cylinder2206,Cylinder2207,Cylinder2208,Cylinder2209,Cylinder2210,Cylinder2211,Cylinder2212,Cylinder2205]
  Placement = pos=(0,0,56) rot=(0,0,1;0rad)
FEATURE [Part::Cut] Cut730
  Base = -> Tube094
  Tool = -> Compound1138
FEATURE [Part::Cut] Cut731
  Base = -> Cut730
  Tool = -> Compound1137
FEATURE [Part::FeaturePython] Tube095  # WARN: FeaturePython — macro-defined, semantics opaque (R4)
  AttacherType = Attacher::AttachEngine3D
  Height = 3
  InnerRadius = 54
  OuterRadius = 61
  Placement = pos=(0,0,52) rot=(0,0,1;0rad)
FEATURE [Part::Chamfer] Chamfer086
  Base = -> Tube095
  Edges = 1 edges r=1: [Edge3]
FEATURE [Part::FeaturePython] Tube096  # WARN: FeaturePython — macro-defined, semantics opaque (R4)
  AttacherType = Attacher::AttachEngine3D
  Height = 8
  InnerRadius = 32
  OuterRadius = 42.6
  Placement = pos=(0,0,58) rot=(0,0,1;0rad)
FEATURE [Part::Chamfer] Chamfer087
  Base = -> Tube096
  Edges = 1 edges r=1: [Edge1]
FEATURE [Part::Cylinder] Cylinder2213  label="Válec2213"
  Angle = 360
  AttacherType = Attacher::AttachEngine3D
  Height = 100
  Placement = pos=(0,-38,0) rot=(0,0,1;0rad)
  Radius = 5
FEATURE [Part::Cylinder] Cylinder2214  label="Válec2214"
  Angle = 360
  AttacherType = Attacher::AttachEngine3D
  Height = 100
  Placement = pos=(26.8701,-26.8701,0) rot=(0,0,1;0.785398rad)
  Radius = 5
FEATURE [Part::Cylinder] Cylinder2215  label="Válec2215"
  Angle = 360
  AttacherType = Attacher::AttachEngine3D
  Height = 100
  Placement = pos=(38,3e-15,0) rot=(0,0,1;1.5708rad)
  Radius = 5
FEATURE [Part::Cylinder] Cylinder2216  label="Válec2216"
  Angle = 360
  AttacherType = Attacher::AttachEngine3D
  Height = 100
  Placement = pos=(21.7959,31.1278,0) rot=(0,0,1;2.53073rad)
  Radius = 5
FEATURE [Part::Cylinder] Cylinder2217  label="Válec2217"
  Angle = 360
  AttacherType = Attacher::AttachEngine3D
  Height = 100
  Placement = pos=(-1e-15,38,0) rot=(0,0,1;3.14159rad)
  Radius = 5
FEATURE [Part::Cylinder] Cylinder2218  label="Válec2218"
  Angle = 360
  AttacherType = Attacher::AttachEngine3D
  Height = 100
  Placement = pos=(-26.8701,26.8701,0) rot=(0,0,1;3.92699rad)
  Radius = 5
FEATURE [Part::Cylinder] Cylinder2219  label="Válec2219"
  Angle = 360
  AttacherType = Attacher::AttachEngine3D
  Height = 100
  Placement = pos=(-38,-6e-15,0) rot=(0,0,-1;1.5708rad)
  Radius = 5
FEATURE [Part::Cylinder] Cylinder2220  label="Válec2220"
  Angle = 360
  AttacherType = Attacher::AttachEngine3D
  Height = 100
  Placement = pos=(-26.8701,-26.8701,0) rot=(0,0,-1;0.785398rad)
  Radius = 5
FEATURE [Part::Compound] Compound1139
  Links = -> [Cylinder2214,Cylinder2215,Cylinder2216,Cylinder2217,Cylinder2218,Cylinder2219,Cylinder2220,Cylinder2213]
  Placement = pos=(0,0,56) rot=(0,0,1;0rad)
FEATURE [Part::Cut] Cut732
  Base = -> Chamfer087
  Tool = -> Compound1139
FEATURE [Part::FeaturePython] Tube047  # WARN: FeaturePython — macro-defined, semantics opaque (R4)
  AttacherType = Attacher::AttachEngine3D
  Height = 55
  InnerRadius = 68
  OuterRadius = 74
  Placement = pos=(0,0,29) rot=(0,0,1;0rad)
FEATURE [Part::Cylinder] Cylinder1893  label="Válec1893"
  Angle = 360
  AttacherType = Attacher::AttachEngine3D
  Height = 72
  Placement = pos=(0,-71,0) rot=(0,0,1;0rad)
  Radius = 1.5
FEATURE [Part::Box] Box876  label="Krychle876"
  AttacherType = Attacher::AttachEngine3D
  Height = 49
  Length = 56
  Placement = pos=(-28,35,29) rot=(0,0,1;0rad)
  Width = 200
FEATURE [Part::Box] Box877  label="Krychle877"
  AttacherType = Attacher::AttachEngine3D
  Height = 55
  Length = 148
  Placement = pos=(-74,68,29) rot=(0,0,1;0rad)
  Width = 26
FEATURE [Part::Box] Box878  label="Krychle878"
  AttacherType = Attacher::AttachEngine3D
  Height = 60
  Length = 200
  Placement = pos=(0,0,-5) rot=(0,0,-1;0.383972rad)
  Width = 200
FEATURE [Part::Box] Box879  label="Krychle879"
  AttacherType = Attacher::AttachEngine3D
  Height = 60
  Length = 200
  Placement = pos=(70.7107,70.7107,-5) rot=(0,0,1;3.92699rad)
  Width = 120
FEATURE [Part::Cut] Cut628
  Base = -> Box879
  Tool = -> Box878
FEATURE [Part::Box] Box880  label="Krychle880"
  AttacherType = Attacher::AttachEngine3D
  Height = 60
  Length = 200
  Placement = pos=(0,0,-5) rot=(0,0,1;3.52556rad)
  Width = 200
FEATURE [Part::Cut] Cut629
  Base = -> Cut628
  Tool = -> Box880
FEATURE [Part::Box] Box881  label="Krychle881"
  AttacherType = Attacher::AttachEngine3D
  Height = 2
  Length = 6
  Placement = pos=(-3,-75,39) rot=(0,0,1;0rad)
  Width = 8
FEATURE [Part::Box] Box882  label="Krychle882"
  AttacherType = Attacher::AttachEngine3D
  Height = 2
  Length = 6
  Placement = pos=(34.9,-66.45,58) rot=(0,0,1;0.523599rad)
  Width = 8
FEATURE [Part::Box] Box883  label="Krychle883"
  AttacherType = Attacher::AttachEngine3D
  Height = 2
  Length = 6
  Placement = pos=(-75,3,39) rot=(0,0,-1;1.5708rad)
  Width = 8
FEATURE [Part::Box] Box884  label="Krychle884"
  AttacherType = Attacher::AttachEngine3D
  Height = 2
  Length = 6
  Placement = pos=(40.0981,63.4519,39) rot=(0,0,1;2.61799rad)
  Width = 8
FEATURE [Part::Cylinder] Cylinder1894  label="Válec1894"
  Angle = 360
  AttacherType = Attacher::AttachEngine3D
  Height = 72
  Placement = pos=(61.4878,35.5,0) rot=(0,0,1;2.0944rad)
  Radius = 1.5
FEATURE [Part::Box] Box885  label="Krychle885"
  AttacherType = Attacher::AttachEngine3D
  Height = 2
  Length = 6
  Placement = pos=(75,-3,39) rot=(0,0,1;1.5708rad)
  Width = 8
FEATURE [Part::Box] Box886  label="Krychle886"
  AttacherType = Attacher::AttachEngine3D
  Height = 2
  Length = 6
  Placement = pos=(-34.9019,66.4519,39) rot=(0,0,1;3.66519rad)
  Width = 8
FEATURE [Part::Box] Box887  label="Krychle887"
  AttacherType = Attacher::AttachEngine3D
  Height = 2
  Length = 6
  Placement = pos=(63.45,-40.1,58) rot=(0,0,1;1.0472rad)
  Width = 8
FEATURE [Part::Box] Box888  label="Krychle888"
  AttacherType = Attacher::AttachEngine3D
  Height = 2
  Length = 6
  Placement = pos=(3,75,39) rot=(0,0,1;3.14159rad)
  Width = 8
FEATURE [Part::Box] Box889  label="Krychle889"
  AttacherType = Attacher::AttachEngine3D
  Height = 2
  Length = 6
  Placement = pos=(-66.4519,-34.9019,39) rot=(0,0,-1;1.0472rad)
  Width = 8
FEATURE [Part::Box] Box890  label="Krychle890"
  AttacherType = Attacher::AttachEngine3D
  Height = 2
  Length = 6
  Placement = pos=(66.4519,34.9019,39) rot=(0,0,1;2.0944rad)
  Width = 8
FEATURE [Part::Box] Box891  label="Krychle891"
  AttacherType = Attacher::AttachEngine3D
  Height = 2
  Length = 6
  Placement = pos=(-40.0981,-63.4519,39) rot=(0,0,-1;0.523599rad)
  Width = 8
FEATURE [Part::Box] Box892  label="Krychle892"
  AttacherType = Attacher::AttachEngine3D
  Height = 2
  Length = 6
  Placement = pos=(-63.4519,40.0981,39) rot=(0,0,1;4.18879rad)
  Width = 8
FEATURE [Part::Compound] Compound998
  Links = -> [Box881,Box882,Box887,Box885,Box890,Box884,Box888,Box886,Box892,Box883,Box889,Box891]
FEATURE [Part::Cylinder] Cylinder1895  label="Válec1895"
  Angle = 360
  AttacherType = Attacher::AttachEngine3D
  Height = 72
  Placement = pos=(71,-1.8e-14,0) rot=(0,0,1;1.5708rad)
  Radius = 1.5
FEATURE [Part::Cylinder] Cylinder1896  label="Válec1896"
  Angle = 360
  AttacherType = Attacher::AttachEngine3D
  Height = 72
  Placement = pos=(35.5,61.4878,0) rot=(0,0,1;2.61799rad)
  Radius = 1.5
FEATURE [Part::Cylinder] Cylinder1897  label="Válec1897"
  Angle = 360
  AttacherType = Attacher::AttachEngine3D
  Height = 72
  Placement = pos=(61.4878,-35.5,0) rot=(0,0,1;1.0472rad)
  Radius = 1.5
FEATURE [Part::Cylinder] Cylinder1898  label="Válec1898"
  Angle = 360
  AttacherType = Attacher::AttachEngine3D
  Height = 72
  Placement = pos=(35.5,-61.4878,0) rot=(0,0,1;0.523599rad)
  Radius = 1.5
FEATURE [Part::Cylinder] Cylinder1899  label="Válec1899"
  Angle = 360
  AttacherType = Attacher::AttachEngine3D
  Height = 72
  Placement = pos=(-35.5,-61.4878,0) rot=(0,0,-1;0.523599rad)
  Radius = 1.5
FEATURE [Part::Cylinder] Cylinder1900  label="Válec1900"
  Angle = 360
  AttacherType = Attacher::AttachEngine3D
  Height = 72
  Placement = pos=(-71,2.7e-14,0) rot=(0,0,-1;1.5708rad)
  Radius = 1.5
FEATURE [Part::Cylinder] Cylinder1901  label="Válec1901"
  Angle = 360
  AttacherType = Attacher::AttachEngine3D
  Height = 72
  Placement = pos=(-61.4878,-35.5,0) rot=(0,0,-1;1.0472rad)
  Radius = 1.5
FEATURE [Part::Cylinder] Cylinder1902  label="Válec1902"
  Angle = 360
  AttacherType = Attacher::AttachEngine3D
  Height = 72
  Placement = pos=(-35.5,61.4878,0) rot=(0,0,1;3.66519rad)
  Radius = 1.5
FEATURE [Part::Cylinder] Cylinder1903  label="Válec1903"
  Angle = 360
  AttacherType = Attacher::AttachEngine3D
  Height = 72
  Placement = pos=(-61.4878,35.5,0) rot=(0,0,1;4.18879rad)
  Radius = 1.5
FEATURE [Part::Cylinder] Cylinder1904  label="Válec1904"
  Angle = 360
  AttacherType = Attacher::AttachEngine3D
  Height = 72
  Placement = pos=(3.1e-14,71,0) rot=(0,0,1;3.14159rad)
  Radius = 1.5
FEATURE [Part::Compound] Compound1000
  Links = -> [Cylinder1893,Cylinder1898,Cylinder1897,Cylinder1895,Cylinder1894,Cylinder1896,Cylinder1904,Cylinder1902,Cylinder1903,Cylinder1900,Cylinder1901,Cylinder1899]
  Placement = pos=(0,0,-4) rot=(0,0,1;0rad)
FEATURE [Part::Cylinder] Cylinder1905  label="Válec1905"
  Angle = 360
  AttacherType = Attacher::AttachEngine3D
  Height = 50
  Placement = pos=(-18,100,72) rot=(1,0,0;1.5708rad)
  Radius = 1.5
FEATURE [Part::Compound] Compound999
  Links = -> [Cylinder1905]
  Placement = pos=(0,0,0) rot=(0,0,1;3.92699rad)
FEATURE [Part::Cylinder] Cylinder1906  label="Válec1906"
  Angle = 360
  AttacherType = Attacher::AttachEngine3D
  Height = 50
  Placement = pos=(18,100,72) rot=(1,0,0;1.5708rad)
  Radius = 1.5
FEATURE [Part::Compound] Compound1001
  Links = -> [Cylinder1906]
  Placement = pos=(0,0,0) rot=(0,0,1;3.92699rad)
FEATURE [Part::Compound] Compound1002
  Links = -> [Compound999,Compound1001]
  Placement = pos=(0,0,1) rot=(0,0,1;0rad)
FEATURE [Part::Box] Box893  label="Krychle893"
  AttacherType = Attacher::AttachEngine3D
  Height = 6
  Length = 6
  Placement = pos=(15,64,-50) rot=(0,0,1;0rad)
  Width = 4
FEATURE [Part::Box] Box894  label="Krychle894"
  AttacherType = Attacher::AttachEngine3D
  Height = 6
  Length = 6
  Placement = pos=(-21,64,-50) rot=(0,0,1;0rad)
  Width = 4
FEATURE [Part::Compound] Compound1003
  Links = -> [Box894,Box893]
  Placement = pos=(0,0,120) rot=(0,0,1;3.92699rad)
FEATURE [Part::FeaturePython] Tube048  # WARN: FeaturePython — macro-defined, semantics opaque (R4)
  AttacherType = Attacher::AttachEngine3D
  Height = 8
  InnerRadius = 55.1
  OuterRadius = 63
  Placement = pos=(0,0,72) rot=(0,0,1;0rad)
FEATURE [Part::Cut] Cut622
  Base = -> Tube047
  Tool = -> Box876
FEATURE [Part::Cut] Cut621
  Base = -> Cut622
  Tool = -> Box877
FEATURE [Part::Cut] Cut630
  Base = -> Cut621
  Tool = -> Cut629
FEATURE [Part::Cut] Cut631
  Base = -> Cut630
  Tool = -> Compound998
FEATURE [Part::Cut] Cut632
  Base = -> Cut631
  Tool = -> Compound1000
FEATURE [Part::Cut] Cut633
  Base = -> Cut632
  Tool = -> Compound1002
FEATURE [Part::Cut] Cut634
  Base = -> Cut633
  Tool = -> Compound1003
FEATURE [Part::Cylinder] Cylinder1907  label="Válec1907"
  Angle = 360
  AttacherType = Attacher::AttachEngine3D
  Height = 50
  Placement = pos=(-9,100,59) rot=(1,0,0;1.5708rad)
  Radius = 1.5
FEATURE [Part::Compound] Compound1006
  Links = -> [Cylinder1907]
  Placement = pos=(0,0,0) rot=(0,0,1;3.92699rad)
FEATURE [Part::Cylinder] Cylinder1908  label="Válec1908"
  Angle = 360
  AttacherType = Attacher::AttachEngine3D
  Height = 50
  Placement = pos=(9,100,59) rot=(1,0,0;1.5708rad)
  Radius = 1.5
FEATURE [Part::Compound] Compound1005
  Links = -> [Cylinder1908]
  Placement = pos=(0,0,0) rot=(0,0,1;3.92699rad)
FEATURE [Part::Compound] Compound1004
  Links = -> [Compound1006,Compound1005]
  Placement = pos=(0,0,1) rot=(0,0,1;0rad)
FEATURE [Part::Cut] Cut635
  Base = -> Cut634
  Tool = -> Compound1004
FEATURE [Part::Box] Box895  label="Krychle895"
  AttacherType = Attacher::AttachEngine3D
  Height = 6
  Length = 6
  Placement = pos=(6,66,-63) rot=(0,0,1;0rad)
  Width = 4
FEATURE [Part::Box] Box896  label="Krychle896"
  AttacherType = Attacher::AttachEngine3D
  Height = 6
  Length = 6
  Placement = pos=(-12,66,-63) rot=(0,0,1;0rad)
  Width = 4
FEATURE [Part::Compound] Compound1007
  Links = -> [Box896,Box895]
  Placement = pos=(0,0,120) rot=(0,0,1;3.92699rad)
FEATURE [Part::Cut] Cut636
  Base = -> Cut635
  Tool = -> Compound1007
FEATURE [Part::Box] Box897  label="Krychle897"
  AttacherType = Attacher::AttachEngine3D
  Height = 8
  Length = 8
  Placement = pos=(-48,16,35) rot=(0,0,1;1.5708rad)
  Width = 20
FEATURE [Part::Box] Box898  label="Krychle898"
  AttacherType = Attacher::AttachEngine3D
  Height = 8
  Length = 8
  Placement = pos=(-48,-14,35) rot=(0,0,1;1.5708rad)
  Width = 20
FEATURE [Part::Box] Box899  label="Krychle899"
  AttacherType = Attacher::AttachEngine3D
  Height = 8
  Length = 8
  Placement = pos=(-48,-14,65) rot=(0,0,1;1.5708rad)
  Width = 20
FEATURE [Part::Box] Box900  label="Krychle900"
  AttacherType = Attacher::AttachEngine3D
  Height = 8
  Length = 8
  Placement = pos=(-48,-14,35) rot=(0,0,1;1.5708rad)
  Width = 20
FEATURE [Part::Box] Box901  label="Krychle901"
  AttacherType = Attacher::AttachEngine3D
  Height = 8
  Length = 8
  Placement = pos=(-48,-14,65) rot=(0,0,1;1.5708rad)
  Width = 20
FEATURE [Part::Compound] Compound1010
  Links = -> [Box900,Box901]
  Placement = pos=(1.5,0,0) rot=(0,0,1;1.5708rad)
FEATURE [Part::Box] Box902  label="Krychle902"
  AttacherType = Attacher::AttachEngine3D
  Height = 8
  Length = 8
  Placement = pos=(-48,-14,35) rot=(0,0,1;1.5708rad)
  Width = 20
FEATURE [Part::Box] Box903  label="Krychle903"
  AttacherType = Attacher::AttachEngine3D
  Height = 8
  Length = 8
  Placement = pos=(-48,-14,65) rot=(0,0,1;1.5708rad)
  Width = 20
FEATURE [Part::Cylinder] Cylinder1909  label="Válec1909"
  Angle = 360
  AttacherType = Attacher::AttachEngine3D
  Height = 40
  Placement = pos=(-86,-10,69) rot=(0,1,0;1.5708rad)
  Radius = 2.5
FEATURE [Part::Cylinder] Cylinder1910  label="Válec1910"
  Angle = 360
  AttacherType = Attacher::AttachEngine3D
  Height = 40
  Placement = pos=(-86,-10,39) rot=(0,1,0;1.5708rad)
  Radius = 2.5
FEATURE [Part::Cylinder] Cylinder1911  label="Válec1911"
  Angle = 360
  AttacherType = Attacher::AttachEngine3D
  Height = 40
  Placement = pos=(-86,20,39) rot=(0,1,0;1.5708rad)
  Radius = 2.5
FEATURE [Part::Cylinder] Cylinder1912  label="Válec1912"
  Angle = 360
  AttacherType = Attacher::AttachEngine3D
  Height = 40
  Placement = pos=(-86,16,68) rot=(0,1,0;1.5708rad)
  Radius = 2.5
FEATURE [Part::Cylinder] Cylinder1913  label="Válec1913"
  Angle = 360
  AttacherType = Attacher::AttachEngine3D
  Height = 40
  Placement = pos=(-86,-10,39) rot=(0,1,0;1.5708rad)
  Radius = 2.5
FEATURE [Part::Cylinder] Cylinder1914  label="Válec1914"
  Angle = 360
  AttacherType = Attacher::AttachEngine3D
  Height = 40
  Placement = pos=(-86,-10,69) rot=(0,1,0;1.5708rad)
  Radius = 2.5
FEATURE [Part::Cylinder] Cylinder1915  label="Válec1915"
  Angle = 360
  AttacherType = Attacher::AttachEngine3D
  Height = 40
  Placement = pos=(-86,-10,69) rot=(0,1,0;1.5708rad)
  Radius = 2.5
FEATURE [Part::Cylinder] Cylinder1916  label="Válec1916"
  Angle = 360
  AttacherType = Attacher::AttachEngine3D
  Height = 40
  Placement = pos=(-86,-10,39) rot=(0,1,0;1.5708rad)
  Radius = 2.5
FEATURE [Part::Box] Box904  label="Krychle904"
  AttacherType = Attacher::AttachEngine3D
  Height = 8
  Length = 8
  Placement = pos=(-68,-14,35) rot=(0,0,1;1.5708rad)
  Width = 2.5
FEATURE [Part::Box] Box905  label="Krychle905"
  AttacherType = Attacher::AttachEngine3D
  Height = 8
  Length = 8
  Placement = pos=(-68,16,35) rot=(0,0,1;1.5708rad)
  Width = 2.5
FEATURE [Part::Box] Box906  label="Krychle906"
  AttacherType = Attacher::AttachEngine3D
  Height = 8
  Length = 8
  Placement = pos=(-68,-14,65) rot=(0,0,1;1.5708rad)
  Width = 2.5
FEATURE [Part::Box] Box907  label="Krychle907"
  AttacherType = Attacher::AttachEngine3D
  Height = 8
  Length = 8
  Placement = pos=(-68,-14,65) rot=(0,0,1;1.5708rad)
  Width = 2.5
FEATURE [Part::Box] Box908  label="Krychle908"
  AttacherType = Attacher::AttachEngine3D
  Height = 8
  Length = 8
  Placement = pos=(-68,-14,35) rot=(0,0,1;1.5708rad)
  Width = 2.5
FEATURE [Part::Box] Box909  label="Krychle909"
  AttacherType = Attacher::AttachEngine3D
  Height = 8
  Length = 8
  Placement = pos=(-68,-14,65) rot=(0,0,1;1.5708rad)
  Width = 2.5
FEATURE [Part::Box] Box910  label="Krychle910"
  AttacherType = Attacher::AttachEngine3D
  Height = 8
  Length = 8
  Placement = pos=(-68,-14,35) rot=(0,0,1;1.5708rad)
  Width = 2.5
FEATURE [Part::Box] Box911  label="Krychle911"
  AttacherType = Attacher::AttachEngine3D
  Height = 8
  Length = 8
  Placement = pos=(-48,12,64) rot=(0,0,1;1.5708rad)
  Width = 20
FEATURE [Part::Compound] Compound1008
  Links = -> [Box898,Box897,Box899,Box911]
FEATURE [Part::Box] Box912  label="Krychle912"
  AttacherType = Attacher::AttachEngine3D
  Height = 8
  Length = 8
  Placement = pos=(-68,12,64) rot=(0,0,1;1.5708rad)
  Width = 2.5
FEATURE [Part::Cylinder] Cylinder1917  label="Válec1917"
  Angle = 360
  AttacherType = Attacher::AttachEngine3D
  Height = 51
  Placement = pos=(0,0,29) rot=(0,0,1;0rad)
  Radius = 74
FEATURE [Part::Box] Box913  label="Krychle913"
  AttacherType = Attacher::AttachEngine3D
  Height = 6
  Length = 8
  Placement = pos=(-75,38,36) rot=(0,0,1;0rad)
  Width = 2
FEATURE [Part::Box] Box914  label="Krychle914"
  AttacherType = Attacher::AttachEngine3D
  Height = 55
  Length = 148
  Placement = pos=(-74,48,29) rot=(0,0,1;0rad)
  Width = 26
FEATURE [Part::Box] Box915  label="Krychle915"
  AttacherType = Attacher::AttachEngine3D
  Height = 6
  Length = 8
  Placement = pos=(67,38,36) rot=(0,0,1;0rad)
  Width = 2
FEATURE [Part::Cylinder] Cylinder1918  label="Válec1918"
  Angle = 360
  AttacherType = Attacher::AttachEngine3D
  Height = 50
  Placement = pos=(-71,80,73) rot=(1,0,0;1.5708rad)
  Radius = 1.5
FEATURE [Part::Compound] Compound1011
  Links = -> [Box902,Box903]
  Placement = pos=(-21.5,0,0) rot=(0,0,1;1.5708rad)
FEATURE [Part::Compound] Compound1009
  Links = -> [Compound1011,Compound1010]
FEATURE [Part::Compound] Compound1012
  Links = -> [Cylinder1910,Cylinder1911,Cylinder1909,Cylinder1912]
FEATURE [Part::Compound] Compound1013
  Links = -> [Cylinder1916,Cylinder1914]
  Placement = pos=(1.5,0,0) rot=(0,0,1;1.5708rad)
FEATURE [Part::Compound] Compound1014
  Links = -> [Cylinder1913,Cylinder1915]
  Placement = pos=(-21.5,0,0) rot=(0,0,1;1.5708rad)
FEATURE [Part::Compound] Compound1015
  Links = -> [Compound1013,Compound1014]
FEATURE [Part::Compound] Compound1016
  Links = -> [Box904,Box905,Box906,Box912]
FEATURE [Part::Compound] Compound1018
  Links = -> [Box908,Box907]
  Placement = pos=(1.5,0,0) rot=(0,0,1;1.5708rad)
FEATURE [Part::Compound] Compound1019
  Links = -> [Box910,Box909]
  Placement = pos=(-21.5,0,0) rot=(0,0,1;1.5708rad)
FEATURE [Part::Compound] Compound1017
  Links = -> [Compound1019,Compound1018]
FEATURE [Part::Cylinder] Cylinder1919  label="Válec1919"
  Angle = 360
  AttacherType = Attacher::AttachEngine3D
  Height = 50
  Placement = pos=(71,80,56) rot=(1,0,0;1.5708rad)
  Radius = 1.5
FEATURE [Part::Cylinder] Cylinder1920  label="Válec1920"
  Angle = 360
  AttacherType = Attacher::AttachEngine3D
  Height = 40
  Placement = pos=(-86,-10,69) rot=(0,1,0;1.5708rad)
  Radius = 2.5
FEATURE [Part::Cylinder] Cylinder1921  label="Válec1921"
  Angle = 360
  AttacherType = Attacher::AttachEngine3D
  Height = 40
  Placement = pos=(-86,-10,39) rot=(0,1,0;1.5708rad)
  Radius = 2.5
FEATURE [Part::Box] Box916  label="Krychle916"
  AttacherType = Attacher::AttachEngine3D
  Height = 55
  Length = 148
  Placement = pos=(-74,0,29) rot=(0,0,1;0rad)
  Width = 74
FEATURE [Part::Cut] Cut638
  Base = -> Box916
  Tool = -> Cylinder1917
FEATURE [Part::Cut] Cut639
  Base = -> Cut638
  Tool = -> Box914
FEATURE [Part::Cylinder] Cylinder1922  label="Válec1922"
  Angle = 360
  AttacherType = Attacher::AttachEngine3D
  Height = 50
  Placement = pos=(71,80,73) rot=(1,0,0;1.5708rad)
  Radius = 1.5
FEATURE [Part::Cylinder] Cylinder1923  label="Válec1923"
  Angle = 360
  AttacherType = Attacher::AttachEngine3D
  Height = 50
  Placement = pos=(71,80,39) rot=(1,0,0;1.5708rad)
  Radius = 1.5
FEATURE [Part::Cylinder] Cylinder1924  label="Válec1924"
  Angle = 360
  AttacherType = Attacher::AttachEngine3D
  Height = 50
  Placement = pos=(-71,80,56) rot=(1,0,0;1.5708rad)
  Radius = 1.5
FEATURE [Part::Cylinder] Cylinder1925  label="Válec1925"
  Angle = 360
  AttacherType = Attacher::AttachEngine3D
  Height = 40
  Placement = pos=(-86,-10,69) rot=(0,1,0;1.5708rad)
  Radius = 2.5
FEATURE [Part::Cylinder] Cylinder1926  label="Válec1926"
  Angle = 360
  AttacherType = Attacher::AttachEngine3D
  Height = 40
  Placement = pos=(-86,-10,39) rot=(0,1,0;1.5708rad)
  Radius = 2.5
FEATURE [Part::Cylinder] Cylinder1927  label="Válec1927"
  Angle = 360
  AttacherType = Attacher::AttachEngine3D
  Height = 40
  Placement = pos=(-86,-10,39) rot=(0,1,0;1.5708rad)
  Radius = 2.5
FEATURE [Part::Cylinder] Cylinder1928  label="Válec1928"
  Angle = 360
  AttacherType = Attacher::AttachEngine3D
  Height = 40
  Placement = pos=(-86,20,39) rot=(0,1,0;1.5708rad)
  Radius = 2.5
FEATURE [Part::Cylinder] Cylinder1929  label="Válec1929"
  Angle = 360
  AttacherType = Attacher::AttachEngine3D
  Height = 40
  Placement = pos=(-86,-10,69) rot=(0,1,0;1.5708rad)
  Radius = 2.5
FEATURE [Part::Box] Box917  label="Krychle917"
  AttacherType = Attacher::AttachEngine3D
  Height = 8
  Length = 8
  Placement = pos=(-48,-14,65) rot=(0,0,1;1.5708rad)
  Width = 20
FEATURE [Part::Box] Box918  label="Krychle918"
  AttacherType = Attacher::AttachEngine3D
  Height = 8
  Length = 8
  Placement = pos=(-48,-14,35) rot=(0,0,1;1.5708rad)
  Width = 20
FEATURE [Part::Compound] Compound1029
  Links = -> [Box918,Box917]
  Placement = pos=(-21.5,0,0) rot=(0,0,1;1.5708rad)
FEATURE [Part::Box] Box919  label="Krychle919"
  AttacherType = Attacher::AttachEngine3D
  Height = 8
  Length = 8
  Placement = pos=(-48,-14,65) rot=(0,0,1;1.5708rad)
  Width = 20
FEATURE [Part::Cylinder] Cylinder1930  label="Válec1930"
  Angle = 360
  AttacherType = Attacher::AttachEngine3D
  Height = 40
  Placement = pos=(-86,-10,39) rot=(0,1,0;1.5708rad)
  Radius = 2.5
FEATURE [Part::Compound] Compound1022
  Links = -> [Cylinder1930,Cylinder1925]
  Placement = pos=(-21.5,0,0) rot=(0,0,1;1.5708rad)
FEATURE [Part::Cylinder] Cylinder1931  label="Válec1931"
  Angle = 360
  AttacherType = Attacher::AttachEngine3D
  Height = 40
  Placement = pos=(-86,20,39) rot=(0,1,0;1.5708rad)
  Radius = 2.5
FEATURE [Part::Cylinder] Cylinder1932  label="Válec1932"
  Angle = 360
  AttacherType = Attacher::AttachEngine3D
  Height = 6
  Placement = pos=(0,0,65) rot=(0,0,1;0rad)
  Radius = 74
FEATURE [Part::Box] Box920  label="Krychle920"
  AttacherType = Attacher::AttachEngine3D
  Height = 34
  Length = 148
  Placement = pos=(-74,68,38) rot=(0,0,1;0rad)
  Width = 20
FEATURE [Part::Cut] Cut625
  Base = -> Cylinder1932
  Placement = pos=(0,0,13) rot=(0,0,1;0rad)
  Tool = -> Box920
FEATURE [Part::Box] Box921  label="Krychle921"
  AttacherType = Attacher::AttachEngine3D
  Height = 8
  Length = 8
  Placement = pos=(-48,-14,35) rot=(0,0,1;1.5708rad)
  Width = 20
FEATURE [Part::Box] Box922  label="Krychle922"
  AttacherType = Attacher::AttachEngine3D
  Height = 8
  Length = 8
  Placement = pos=(-48,-14,35) rot=(0,0,1;1.5708rad)
  Width = 20
FEATURE [Part::Compound] Compound1032
  Links = -> [Box922,Box919]
  Placement = pos=(1.5,0,0) rot=(0,0,1;1.5708rad)
FEATURE [Part::Compound] Compound1028
  Links = -> [Compound1029,Compound1032]
FEATURE [Part::Box] Box923  label="Krychle923"
  AttacherType = Attacher::AttachEngine3D
  Height = 8
  Length = 8
  Placement = pos=(-48,-14,65) rot=(0,0,1;1.5708rad)
  Width = 20
FEATURE [Part::Box] Box924  label="Krychle924"
  AttacherType = Attacher::AttachEngine3D
  Height = 8
  Length = 8
  Placement = pos=(-48,16,35) rot=(0,0,1;1.5708rad)
  Width = 20
FEATURE [Part::Box] Box925  label="Krychle925"
  AttacherType = Attacher::AttachEngine3D
  Height = 8
  Length = 8
  Placement = pos=(-48,16,35) rot=(0,0,1;1.5708rad)
  Width = 20
FEATURE [Part::Box] Box926  label="Krychle926"
  AttacherType = Attacher::AttachEngine3D
  Height = 8
  Length = 8
  Placement = pos=(-68,12,64) rot=(0,0,1;1.5708rad)
  Width = 2.5
FEATURE [Part::Box] Box927  label="Krychle927"
  AttacherType = Attacher::AttachEngine3D
  Height = 8
  Length = 8
  Placement = pos=(-48,-14,65) rot=(0,0,1;1.5708rad)
  Width = 20
FEATURE [Part::Box] Box928  label="Krychle928"
  AttacherType = Attacher::AttachEngine3D
  Height = 8
  Length = 8
  Placement = pos=(-48,-14,35) rot=(0,0,1;1.5708rad)
  Width = 20
FEATURE [Part::Box] Box929  label="Krychle929"
  AttacherType = Attacher::AttachEngine3D
  Height = 8
  Length = 8
  Placement = pos=(-68,-14,65) rot=(0,0,1;1.5708rad)
  Width = 2.5
FEATURE [Part::Box] Box930  label="Krychle930"
  AttacherType = Attacher::AttachEngine3D
  Height = 8
  Length = 8
  Placement = pos=(-68,16,35) rot=(0,0,1;1.5708rad)
  Width = 2.5
FEATURE [Part::Box] Box931  label="Krychle931"
  AttacherType = Attacher::AttachEngine3D
  Height = 8
  Length = 8
  Placement = pos=(-68,-14,35) rot=(0,0,1;1.5708rad)
  Width = 2.5
FEATURE [Part::Box] Box932  label="Krychle932"
  AttacherType = Attacher::AttachEngine3D
  Height = 8
  Length = 8
  Placement = pos=(-48,12,64) rot=(0,0,1;1.5708rad)
  Width = 20
FEATURE [Part::Cylinder] Cylinder1933  label="Válec1933"
  Angle = 360
  AttacherType = Attacher::AttachEngine3D
  Height = 40
  Placement = pos=(-86,-10,69) rot=(0,1,0;1.5708rad)
  Radius = 2.5
FEATURE [Part::Cylinder] Cylinder1934  label="Válec1934"
  Angle = 360
  AttacherType = Attacher::AttachEngine3D
  Height = 40
  Placement = pos=(-86,-10,69) rot=(0,1,0;1.5708rad)
  Radius = 2.5
FEATURE [Part::Compound] Compound1020
  Links = -> [Cylinder1927,Cylinder1934]
  Placement = pos=(1.5,0,0) rot=(0,0,1;1.5708rad)
FEATURE [Part::Cylinder] Cylinder1935  label="Válec1935"
  Angle = 360
  AttacherType = Attacher::AttachEngine3D
  Height = 40
  Placement = pos=(-86,16,68) rot=(0,1,0;1.5708rad)
  Radius = 2.5
FEATURE [Part::Cylinder] Cylinder1936  label="Válec1936"
  Angle = 360
  AttacherType = Attacher::AttachEngine3D
  Height = 40
  Placement = pos=(-86,20,39) rot=(0,1,0;1.5708rad)
  Radius = 2.5
FEATURE [Part::Cylinder] Cylinder1937  label="Válec1937"
  Angle = 360
  AttacherType = Attacher::AttachEngine3D
  Height = 40
  Placement = pos=(-86,-10,39) rot=(0,1,0;1.5708rad)
  Radius = 2.5
FEATURE [Part::Cylinder] Cylinder1938  label="Válec1938"
  Angle = 360
  AttacherType = Attacher::AttachEngine3D
  Height = 40
  Placement = pos=(-86,-10,69) rot=(0,1,0;1.5708rad)
  Radius = 2.5
FEATURE [Part::Box] Box933  label="Krychle933"
  AttacherType = Attacher::AttachEngine3D
  Height = 8
  Length = 8
  Placement = pos=(-68,12,64) rot=(0,0,1;1.5708rad)
  Width = 2.5
FEATURE [Part::Compound] Compound1044
  Links = -> [Box931,Box930,Box929,Box933]
FEATURE [Part::Mirroring] mirror014  label="Compound999 (mirrored)001"
  Base = (0,0,0)
  Normal = (1,0,0)
  Source = -> Compound1044
FEATURE [Part::Box] Box934  label="Krychle934"
  AttacherType = Attacher::AttachEngine3D
  Height = 8
  Length = 8
  Placement = pos=(-48,16,35) rot=(0,0,1;1.5708rad)
  Width = 20
FEATURE [Part::Box] Box935  label="Krychle935"
  AttacherType = Attacher::AttachEngine3D
  Height = 8
  Length = 8
  Placement = pos=(-48,-14,35) rot=(0,0,1;1.5708rad)
  Width = 20
FEATURE [Part::Box] Box936  label="Krychle936"
  AttacherType = Attacher::AttachEngine3D
  Height = 8
  Length = 8
  Placement = pos=(-48,-14,65) rot=(0,0,1;1.5708rad)
  Width = 20
FEATURE [Part::Box] Box937  label="Krychle937"
  AttacherType = Attacher::AttachEngine3D
  Height = 8
  Length = 8
  Placement = pos=(-48,12,64) rot=(0,0,1;1.5708rad)
  Width = 20
FEATURE [Part::Compound] Compound1034
  Links = -> [Box935,Box934,Box936,Box937]
FEATURE [Part::Mirroring] mirror013  label="Compound998 (mirrored)"
  Base = (0,0,0)
  Normal = (1,0,0)
  Source = -> Compound1034
FEATURE [Part::Compound] Compound1037
  Links = -> [Compound1008,Compound1009,mirror013]
FEATURE [Part::Cut] Cut637
  Base = -> Cut636
  Tool = -> Compound1037
FEATURE [Part::Box] Box938  label="Krychle938"
  AttacherType = Attacher::AttachEngine3D
  Height = 8
  Length = 8
  Placement = pos=(-68,-14,35) rot=(0,0,1;1.5708rad)
  Width = 2.5
FEATURE [Part::Box] Box939  label="Krychle939"
  AttacherType = Attacher::AttachEngine3D
  Height = 8
  Length = 8
  Placement = pos=(-68,16,35) rot=(0,0,1;1.5708rad)
  Width = 2.5
FEATURE [Part::Box] Box940  label="Krychle940"
  AttacherType = Attacher::AttachEngine3D
  Height = 8
  Length = 8
  Placement = pos=(-68,-14,65) rot=(0,0,1;1.5708rad)
  Width = 2.5
FEATURE [Part::Box] Box941  label="Krychle941"
  AttacherType = Attacher::AttachEngine3D
  Height = 8
  Length = 8
  Placement = pos=(-68,12,64) rot=(0,0,1;1.5708rad)
  Width = 2.5
FEATURE [Part::Compound] Compound1024
  Links = -> [Box938,Box939,Box940,Box941]
FEATURE [Part::Mirroring] mirror001  label="Compound999 (mirrored)"
  Base = (0,0,0)
  Normal = (1,0,0)
  Source = -> Compound1024
FEATURE [Part::Compound] Compound1030
  Links = -> [Compound1016,Compound1017,mirror001]
FEATURE [Part::Cut] Cut623
  Base = -> Cut637
  Tool = -> Compound1030
FEATURE [Part::Cylinder] Cylinder1939  label="Válec1939"
  Angle = 360
  AttacherType = Attacher::AttachEngine3D
  Height = 40
  Placement = pos=(-86,-10,69) rot=(0,1,0;1.5708rad)
  Radius = 2.5
FEATURE [Part::Cylinder] Cylinder1940  label="Válec1940"
  Angle = 360
  AttacherType = Attacher::AttachEngine3D
  Height = 40
  Placement = pos=(-86,-10,39) rot=(0,1,0;1.5708rad)
  Radius = 2.5
FEATURE [Part::Cylinder] Cylinder1941  label="Válec1941"
  Angle = 360
  AttacherType = Attacher::AttachEngine3D
  Height = 40
  Placement = pos=(-86,20,39) rot=(0,1,0;1.5708rad)
  Radius = 2.5
FEATURE [Part::Cylinder] Cylinder1942  label="Válec1942"
  Angle = 360
  AttacherType = Attacher::AttachEngine3D
  Height = 40
  Placement = pos=(-86,16,68) rot=(0,1,0;1.5708rad)
  Radius = 2.5
FEATURE [Part::Compound] Compound1026
  Links = -> [Cylinder1940,Cylinder1941,Cylinder1939,Cylinder1942]
FEATURE [Part::Mirroring] mirror002  label="Compound1000 (mirrored)"
  Base = (0,0,0)
  Normal = (1,0,0)
  Source = -> Compound1026
FEATURE [Part::Compound] Compound1033
  Links = -> [Compound1012,Compound1015,mirror002]
FEATURE [Part::Cut] Cut624
  Base = -> Cut623
  Tool = -> Compound1033
FEATURE [Part::Cylinder] Cylinder1943  label="Válec1943"
  Angle = 360
  AttacherType = Attacher::AttachEngine3D
  Height = 40
  Placement = pos=(-86,-10,39) rot=(0,1,0;1.5708rad)
  Radius = 2.5
FEATURE [Part::Cylinder] Cylinder1944  label="Válec1944"
  Angle = 360
  AttacherType = Attacher::AttachEngine3D
  Height = 40
  Placement = pos=(-86,20,39) rot=(0,1,0;1.5708rad)
  Radius = 2.5
FEATURE [Part::Cylinder] Cylinder1945  label="Válec1945"
  Angle = 360
  AttacherType = Attacher::AttachEngine3D
  Height = 40
  Placement = pos=(-86,16,68) rot=(0,1,0;1.5708rad)
  Radius = 2.5
FEATURE [Part::Compound] Compound1036
  Links = -> [Cylinder1943,Cylinder1944,Cylinder1929,Cylinder1945]
FEATURE [Part::Cylinder] Cylinder1946  label="Válec1946"
  Angle = 360
  AttacherType = Attacher::AttachEngine3D
  Height = 40
  Placement = pos=(-86,-10,39) rot=(0,1,0;1.5708rad)
  Radius = 2.5
FEATURE [Part::Cylinder] Cylinder1947  label="Válec1947"
  Angle = 360
  AttacherType = Attacher::AttachEngine3D
  Height = 40
  Placement = pos=(-86,-10,69) rot=(0,1,0;1.5708rad)
  Radius = 2.5
FEATURE [Part::Cylinder] Cylinder1948  label="Válec1948"
  Angle = 360
  AttacherType = Attacher::AttachEngine3D
  Height = 40
  Placement = pos=(-86,-10,69) rot=(0,1,0;1.5708rad)
  Radius = 2.5
FEATURE [Part::Compound] Compound1038
  Links = -> [Cylinder1946,Cylinder1948]
  Placement = pos=(-21.5,0,0) rot=(0,0,1;1.5708rad)
FEATURE [Part::Cylinder] Cylinder1949  label="Válec1949"
  Angle = 360
  AttacherType = Attacher::AttachEngine3D
  Height = 40
  Placement = pos=(-86,-10,39) rot=(0,1,0;1.5708rad)
  Radius = 2.5
FEATURE [Part::Compound] Compound1035
  Links = -> [Cylinder1949,Cylinder1947]
  Placement = pos=(1.5,0,0) rot=(0,0,1;1.5708rad)
FEATURE [Part::Compound] Compound1039
  Links = -> [Compound1035,Compound1038]
FEATURE [Part::Box] Box942  label="Krychle942"
  AttacherType = Attacher::AttachEngine3D
  Height = 8
  Length = 8
  Placement = pos=(-68,-14,35) rot=(0,0,1;1.5708rad)
  Width = 2.5
FEATURE [Part::Box] Box943  label="Krychle943"
  AttacherType = Attacher::AttachEngine3D
  Height = 8
  Length = 8
  Placement = pos=(-68,16,35) rot=(0,0,1;1.5708rad)
  Width = 2.5
FEATURE [Part::Box] Box944  label="Krychle944"
  AttacherType = Attacher::AttachEngine3D
  Height = 8
  Length = 8
  Placement = pos=(-68,-14,65) rot=(0,0,1;1.5708rad)
  Width = 2.5
FEATURE [Part::Compound] Compound1040
  Links = -> [Box942,Box943,Box944,Box926]
FEATURE [Part::Box] Box945  label="Krychle945"
  AttacherType = Attacher::AttachEngine3D
  Height = 8
  Length = 8
  Placement = pos=(-68,-14,65) rot=(0,0,1;1.5708rad)
  Width = 2.5
FEATURE [Part::Box] Box946  label="Krychle946"
  AttacherType = Attacher::AttachEngine3D
  Height = 8
  Length = 8
  Placement = pos=(-68,-14,35) rot=(0,0,1;1.5708rad)
  Width = 2.5
FEATURE [Part::Compound] Compound1042
  Links = -> [Box946,Box945]
  Placement = pos=(1.5,0,0) rot=(0,0,1;1.5708rad)
FEATURE [Part::Box] Box947  label="Krychle947"
  AttacherType = Attacher::AttachEngine3D
  Height = 8
  Length = 8
  Placement = pos=(-68,-14,65) rot=(0,0,1;1.5708rad)
  Width = 2.5
FEATURE [Part::Box] Box948  label="Krychle948"
  AttacherType = Attacher::AttachEngine3D
  Height = 8
  Length = 8
  Placement = pos=(-68,-14,35) rot=(0,0,1;1.5708rad)
  Width = 2.5
FEATURE [Part::Compound] Compound1043
  Links = -> [Box948,Box947]
  Placement = pos=(-21.5,0,0) rot=(0,0,1;1.5708rad)
FEATURE [Part::Compound] Compound1041
  Links = -> [Compound1043,Compound1042]
FEATURE [Part::Box] Box949  label="Krychle949"
  AttacherType = Attacher::AttachEngine3D
  Height = 8
  Length = 8
  Placement = pos=(-48,12,64) rot=(0,0,1;1.5708rad)
  Width = 20
FEATURE [Part::Compound] Compound1031
  Links = -> [Box921,Box924,Box923,Box949]
FEATURE [Part::Cylinder] Cylinder1950  label="Válec1950"
  Angle = 360
  AttacherType = Attacher::AttachEngine3D
  Height = 50
  Placement = pos=(-71,80,39) rot=(1,0,0;1.5708rad)
  Radius = 1.5
FEATURE [Part::Compound] Compound1025
  Links = -> [Cylinder1918,Cylinder1923,Cylinder1950,Cylinder1922,Cylinder1924,Cylinder1919]
FEATURE [Part::Cut] Cut640
  Base = -> Cut639
  Tool = -> Compound1025
FEATURE [Part::Box] Box950  label="Krychle950"
  AttacherType = Attacher::AttachEngine3D
  Height = 6
  Length = 8
  Placement = pos=(67,38,70) rot=(0,0,1;0rad)
  Width = 2
FEATURE [Part::Box] Box951  label="Krychle951"
  AttacherType = Attacher::AttachEngine3D
  Height = 6
  Length = 8
  Placement = pos=(-75,38,70) rot=(0,0,1;0rad)
  Width = 2
FEATURE [Part::Box] Box952  label="Krychle952"
  AttacherType = Attacher::AttachEngine3D
  Height = 6
  Length = 8
  Placement = pos=(-75,38,53) rot=(0,0,1;0rad)
  Width = 2
FEATURE [Part::Box] Box953  label="Krychle953"
  AttacherType = Attacher::AttachEngine3D
  Height = 6
  Length = 8
  Placement = pos=(67,38,53) rot=(0,0,1;0rad)
  Width = 2
FEATURE [Part::Compound] Compound1021
  Links = -> [Box913,Box915,Box950,Box951,Box952,Box953]
FEATURE [Part::Cut] Cut641
  Base = -> Cut640
  Tool = -> Compound1021
FEATURE [Part::Box] Box954  label="Krychle954"
  AttacherType = Attacher::AttachEngine3D
  Height = 2
  Length = 6
  Placement = pos=(-3,-75,39) rot=(0,0,1;0rad)
  Width = 8
FEATURE [Part::Box] Box955  label="Krychle955"
  AttacherType = Attacher::AttachEngine3D
  Height = 2
  Length = 6
  Placement = pos=(34.9019,-66.4519,39) rot=(0,0,1;0.523599rad)
  Width = 8
FEATURE [Part::Box] Box956  label="Krychle956"
  AttacherType = Attacher::AttachEngine3D
  Height = 2
  Length = 6
  Placement = pos=(63.4519,-40.0981,39) rot=(0,0,1;1.0472rad)
  Width = 8
FEATURE [Part::Box] Box957  label="Krychle957"
  AttacherType = Attacher::AttachEngine3D
  Height = 2
  Length = 6
  Placement = pos=(75,-3,39) rot=(0,0,1;1.5708rad)
  Width = 8
FEATURE [Part::Box] Box958  label="Krychle958"
  AttacherType = Attacher::AttachEngine3D
  Height = 2
  Length = 6
  Placement = pos=(66.4519,34.9019,39) rot=(0,0,1;2.0944rad)
  Width = 8
FEATURE [Part::Box] Box959  label="Krychle959"
  AttacherType = Attacher::AttachEngine3D
  Height = 2
  Length = 6
  Placement = pos=(40.0981,63.4519,39) rot=(0,0,1;2.61799rad)
  Width = 8
FEATURE [Part::Box] Box960  label="Krychle960"
  AttacherType = Attacher::AttachEngine3D
  Height = 2
  Length = 6
  Placement = pos=(3,75,39) rot=(0,0,1;3.14159rad)
  Width = 8
FEATURE [Part::Box] Box961  label="Krychle961"
  AttacherType = Attacher::AttachEngine3D
  Height = 2
  Length = 6
  Placement = pos=(-34.9019,66.4519,39) rot=(0,0,1;3.66519rad)
  Width = 8
FEATURE [Part::Box] Box962  label="Krychle962"
  AttacherType = Attacher::AttachEngine3D
  Height = 2
  Length = 6
  Placement = pos=(-63.4519,40.0981,39) rot=(0,0,1;4.18879rad)
  Width = 8
FEATURE [Part::Box] Box963  label="Krychle963"
  AttacherType = Attacher::AttachEngine3D
  Height = 2
  Length = 6
  Placement = pos=(-75,3,39) rot=(0,0,-1;1.5708rad)
  Width = 8
FEATURE [Part::Box] Box964  label="Krychle964"
  AttacherType = Attacher::AttachEngine3D
  Height = 2
  Length = 6
  Placement = pos=(-66.4519,-34.9019,39) rot=(0,0,-1;1.0472rad)
  Width = 8
FEATURE [Part::Box] Box965  label="Krychle965"
  AttacherType = Attacher::AttachEngine3D
  Height = 2
  Length = 6
  Placement = pos=(-40.0981,-63.4519,39) rot=(0,0,-1;0.523599rad)
  Width = 8
FEATURE [Part::Compound] Compound1023
  Links = -> [Box954,Box955,Box956,Box957,Box958,Box959,Box960,Box961,Box962,Box963,Box964,Box965]
FEATURE [Part::Cut] Cut626
  Base = -> Cut641
  Tool = -> Compound1023
FEATURE [Part::Compound] Compound1045
  Links = -> [Cylinder1937,Cylinder1936,Cylinder1938,Cylinder1935]
FEATURE [Part::Mirroring] mirror015  label="Compound1000 (mirrored)001"
  Base = (0,0,0)
  Normal = (1,0,0)
  Source = -> Compound1045
FEATURE [Part::Compound] Compound1046
  Links = -> [Compound1040,Compound1041,mirror014]
FEATURE [Part::Compound] Compound1047
  Links = -> [Compound1036,Compound1039,mirror015]
FEATURE [Part::Compound] Compound1048
  Links = -> [Box928,Box925,Box927,Box932]
FEATURE [Part::Mirroring] mirror016  label="Compound998 (mirrored)001"
  Base = (0,0,0)
  Normal = (1,0,0)
  Source = -> Compound1048
FEATURE [Part::Compound] Compound1049
  Links = -> [Compound1031,Compound1028,mirror016]
FEATURE [Part::Compound] Compound1050
  Links = -> [Cylinder1921,Cylinder1931,Cylinder1933]
FEATURE [Part::Mirroring] mirror012  label="Compound944 (mirrored)002"
  Base = (0,0,0)
  Normal = (1,0,0)
  Source = -> Compound1050
FEATURE [Part::Compound] Compound1051
  Links = -> [Compound1020,Compound1022]
FEATURE [Part::Compound] Compound1053
  Links = -> [Cylinder1926,Cylinder1928,Cylinder1920]
FEATURE [Part::Compound] Compound1052
  Links = -> [Compound1053,Compound1051,mirror012]
FEATURE [Part::Cut] Cut627
  Base = -> Cut626
  Tool = -> Compound1052
FEATURE [Part::Cut] Cut642
  Base = -> Cut627
  Tool = -> Compound1049
FEATURE [Part::Cut] Cut643
  Base = -> Cut642
  Tool = -> Compound1047
FEATURE [Part::Cut] Cut644
  Base = -> Cut643
  Tool = -> Compound1046
FEATURE [Part::Compound] Compound1027  label="Base_bare-turret"
  Links = -> [Cut624,Cut625,Cut644,Tube048]
  Placement = pos=(0,0,2) rot=(0,0,1;0rad)
FEATURE [Part::Chamfer] Chamfer088
  Base = -> Cut732
  Edges = 5 edges r=0.9: [Edge38,Edge39,Edge41,Edge42,Edge45]
FEATURE [Part::Chamfer] Chamfer089
  Base = -> Chamfer088
  Edges = 4 edges r=0.9: [Edge2,Edge5,Edge8,Edge11]
FEATURE [Part::Chamfer] Chamfer090
  Base = -> Chamfer089
  Edges = 1 edges r=0.9: [Edge14]
FEATURE [Part::Compound] Compound1140  label="Base_inner-cylinder-belt-B"
  Links = -> [Cut731,Chamfer086,Chamfer090]
FEATURE [Part::Cylinder] Cylinder2221  label="Válec2221"
  Angle = 360
  AttacherType = Attacher::AttachEngine3D
  Height = 100
  Placement = pos=(0,-38,0) rot=(0,0,1;0rad)
  Radius = 1.5
FEATURE [Part::Cylinder] Cylinder2222  label="Válec2222"
  Angle = 360
  AttacherType = Attacher::AttachEngine3D
  Height = 100
  Placement = pos=(26.8701,-26.8701,0) rot=(0,0,1;0.785398rad)
  Radius = 1.5
FEATURE [Part::Cylinder] Cylinder2223  label="Válec2223"
  Angle = 360
  AttacherType = Attacher::AttachEngine3D
  Height = 100
  Placement = pos=(38,3e-15,0) rot=(0,0,1;1.5708rad)
  Radius = 1.5
FEATURE [Part::Cylinder] Cylinder2224  label="Válec2224"
  Angle = 360
  AttacherType = Attacher::AttachEngine3D
  Height = 100
  Placement = pos=(21.7959,31.1278,0) rot=(0,0,1;2.53073rad)
  Radius = 1.5
FEATURE [Part::Cylinder] Cylinder2225  label="Válec2225"
  Angle = 360
  AttacherType = Attacher::AttachEngine3D
  Height = 100
  Placement = pos=(-1e-15,38,0) rot=(0,0,1;3.14159rad)
  Radius = 1.5
FEATURE [Part::Cylinder] Cylinder2226  label="Válec2226"
  Angle = 360
  AttacherType = Attacher::AttachEngine3D
  Height = 100
  Placement = pos=(-26.8701,26.8701,0) rot=(0,0,1;3.92699rad)
  Radius = 1.5
FEATURE [Part::Cylinder] Cylinder2227  label="Válec2227"
  Angle = 360
  AttacherType = Attacher::AttachEngine3D
  Height = 100
  Placement = pos=(-38,-6e-15,0) rot=(0,0,-1;1.5708rad)
  Radius = 1.5
FEATURE [Part::Cylinder] Cylinder2228  label="Válec2228"
  Angle = 360
  AttacherType = Attacher::AttachEngine3D
  Height = 100
  Placement = pos=(-26.8701,-26.8701,0) rot=(0,0,-1;0.785398rad)
  Radius = 1.5
FEATURE [Part::Compound] Compound1122
  Links = -> [Cylinder2223,Cylinder2226,Cylinder2227,Cylinder2225,Cylinder2228,Cylinder2221,Cylinder2222,Cylinder2224]
FEATURE [Part::Cut] Cut710
  Base = -> Cut709
  Tool = -> Compound1122
FEATURE [Part::Cut] Cut712
  Base = -> Cut710
  Tool = -> Compound1121
FEATURE [Part::Compound] Compound1124  label="Base_inner-cylinder"
  Links = -> [Cut712,Chamfer083]
FEATURE [Part::Cylinder] Cylinder2229  label="Válec2229"
  Angle = 360
  AttacherType = Attacher::AttachEngine3D
  Height = 160
  Placement = pos=(-18,0,-60) rot=(0,0,1;0rad)
  Radius = 17
FEATURE [Part::Cylinder] Cylinder2230  label="Válec2230"
  Angle = 360
  AttacherType = Attacher::AttachEngine3D
  Height = 100
  Placement = pos=(-34,-16,-60) rot=(0,0,1;0rad)
  Radius = 1.5
FEATURE [Part::Cylinder] Cylinder2231  label="Válec2231"
  Angle = 360
  AttacherType = Attacher::AttachEngine3D
  Height = 160
  Placement = pos=(-18,0,-60) rot=(0,0,1;0rad)
  Radius = 17
FEATURE [Part::Cylinder] Cylinder2232  label="Válec2232"
  Angle = 360
  AttacherType = Attacher::AttachEngine3D
  Height = 100
  Placement = pos=(-16,-34,-60) rot=(0,0,1;0rad)
  Radius = 1.5
FEATURE [Part::Cylinder] Cylinder2233  label="Válec2233"
  Angle = 360
  AttacherType = Attacher::AttachEngine3D
  Height = 100
  Placement = pos=(16,34,-60) rot=(0,0,1;0rad)
  Radius = 1.5
FEATURE [Part::Cylinder] Cylinder2234  label="Válec2234"
  Angle = 360
  AttacherType = Attacher::AttachEngine3D
  Height = 100
  Placement = pos=(10,-36,-60) rot=(0,0,1;0rad)
  Radius = 1.5
FEATURE [Part::Cylinder] Cylinder2235  label="Válec2235"
  Angle = 360
  AttacherType = Attacher::AttachEngine3D
  Height = 100
  Placement = pos=(34,16,-60) rot=(0,0,1;0rad)
  Radius = 1.5
FEATURE [Part::Cylinder] Cylinder2236  label="Válec2236"
  Angle = 360
  AttacherType = Attacher::AttachEngine3D
  Height = 100
  Placement = pos=(34,-16,-60) rot=(0,0,1;0rad)
  Radius = 1.5
FEATURE [Part::Cylinder] Cylinder2237  label="Válec2237"
  Angle = 360
  AttacherType = Attacher::AttachEngine3D
  Height = 100
  Placement = pos=(-34,16,-60) rot=(0,0,1;0rad)
  Radius = 1.5
FEATURE [Part::Cylinder] Cylinder2238  label="Válec2238"
  Angle = 360
  AttacherType = Attacher::AttachEngine3D
  Height = 100
  Placement = pos=(-16,34,-60) rot=(0,0,1;0rad)
  Radius = 1.5
FEATURE [Part::Compound] Compound1141  label="sbouby_baze011"
  Links = -> [Cylinder2237,Cylinder2230,Cylinder2236,Cylinder2235,Cylinder2233,Cylinder2234,Cylinder2232,Cylinder2238]
  Placement = pos=(0,0,40) rot=(0,0,1;0rad)
FEATURE [Part::Box] Box1046  label="Krychle1046"
  AttacherType = Attacher::AttachEngine3D
  Height = 20
  Length = 6
  Placement = pos=(13,31,0) rot=(0,0,1;0rad)
  Width = 6
FEATURE [Part::Box] Box1047  label="Krychle1047"
  AttacherType = Attacher::AttachEngine3D
  Height = 20
  Length = 6
  Placement = pos=(-19,31,0) rot=(0,0,1;0rad)
  Width = 6
FEATURE [Part::Box] Box1048  label="Krychle1048"
  AttacherType = Attacher::AttachEngine3D
  Height = 20
  Length = 6
  Placement = pos=(-19,-37,0) rot=(0,0,1;0rad)
  Width = 6
FEATURE [Part::Box] Box1049  label="Krychle1049"
  AttacherType = Attacher::AttachEngine3D
  Height = 20
  Length = 6
  Placement = pos=(7,-39,0) rot=(0,0,1;0rad)
  Width = 6
FEATURE [Part::Box] Box1050  label="Krychle1050"
  AttacherType = Attacher::AttachEngine3D
  Height = 20
  Length = 6
  Placement = pos=(31,13,0) rot=(0,0,1;0rad)
  Width = 6
FEATURE [Part::Box] Box1051  label="Krychle1051"
  AttacherType = Attacher::AttachEngine3D
  Height = 20
  Length = 6
  Placement = pos=(31,-19,0) rot=(0,0,1;0rad)
  Width = 6
FEATURE [Part::Box] Box1052  label="Krychle1052"
  AttacherType = Attacher::AttachEngine3D
  Height = 20
  Length = 6
  Placement = pos=(-37,13,0) rot=(0,0,1;0rad)
  Width = 6
FEATURE [Part::Box] Box1053  label="Krychle1053"
  AttacherType = Attacher::AttachEngine3D
  Height = 20
  Length = 6
  Placement = pos=(-37,-19,0) rot=(0,0,1;0rad)
  Width = 6
FEATURE [Part::Compound] Compound1142
  Links = -> [Box1046,Box1047,Box1048,Box1049,Box1050,Box1051,Box1052,Box1053]
  Placement = pos=(0,0,22) rot=(0,0,1;0rad)
FEATURE [Part::Cylinder] Cylinder2239  label="Válec2239"
  Angle = 360
  AttacherType = Attacher::AttachEngine3D
  Height = 40
  Placement = pos=(91,-27,-18) rot=(0,0,1;0rad)
  Radius = 4
FEATURE [Part::Cylinder] Cylinder2240  label="Válec2240"
  Angle = 360
  AttacherType = Attacher::AttachEngine3D
  Height = 40
  Placement = pos=(1,-12,-18) rot=(0,0,1;0rad)
  Radius = 4
FEATURE [Part::Cylinder] Cylinder2241  label="Válec2241"
  Angle = 360
  AttacherType = Attacher::AttachEngine3D
  Height = 40
  Placement = pos=(76,24,-18) rot=(0,0,1;0rad)
  Radius = 4
FEATURE [Part::Cylinder] Cylinder2242  label="Válec2242"
  Angle = 360
  AttacherType = Attacher::AttachEngine3D
  Height = 40
  Placement = pos=(103,-12,-20) rot=(0,0,1;0rad)
  Radius = 4
FEATURE [Part::Cylinder] Cylinder2243  label="Válec2243"
  Angle = 360
  AttacherType = Attacher::AttachEngine3D
  Height = 40
  Placement = pos=(28,24,-18) rot=(0,0,1;0rad)
  Radius = 4
FEATURE [Part::Cylinder] Cylinder2244  label="Válec2244"
  Angle = 360
  AttacherType = Attacher::AttachEngine3D
  Height = 40
  Placement = pos=(1,12,-18) rot=(0,0,1;0rad)
  Radius = 4
FEATURE [Part::Cylinder] Cylinder2245  label="Válec2245"
  Angle = 360
  AttacherType = Attacher::AttachEngine3D
  Height = 40
  Placement = pos=(103,12,-20) rot=(0,0,1;0rad)
  Radius = 4
FEATURE [Part::Cylinder] Cylinder2246  label="Válec2246"
  Angle = 360
  AttacherType = Attacher::AttachEngine3D
  Height = 40
  Placement = pos=(13,-27,-18) rot=(0,0,1;0rad)
  Radius = 4
FEATURE [Part::Compound] Compound1143  label="srouby_monoblok_silne007"
  Links = -> [Cylinder2242,Cylinder2245,Cylinder2241,Cylinder2239,Cylinder2246,Cylinder2243,Cylinder2240,Cylinder2244]
  Placement = pos=(0,0,20) rot=(0,0,1;0rad)
FEATURE [Part::Cylinder] Cylinder2247  label="Válec2247"
  Angle = 360
  AttacherType = Attacher::AttachEngine3D
  Height = 40
  Placement = pos=(1,-12,-18) rot=(0,0,1;0rad)
  Radius = 4
FEATURE [Part::Cylinder] Cylinder2248  label="Válec2248"
  Angle = 360
  AttacherType = Attacher::AttachEngine3D
  Height = 40
  Placement = pos=(28,24,-18) rot=(0,0,1;0rad)
  Radius = 4
FEATURE [Part::Cylinder] Cylinder2249  label="Válec2249"
  Angle = 360
  AttacherType = Attacher::AttachEngine3D
  Height = 40
  Placement = pos=(103,12,-20) rot=(0,0,1;0rad)
  Radius = 4
FEATURE [Part::FeaturePython] Tube097  # WARN: FeaturePython — macro-defined, semantics opaque (R4)
  AttacherType = Attacher::AttachEngine3D
  Height = 22
  InnerRadius = 24
  OuterRadius = 42.65
  Placement = pos=(0,0,5) rot=(0,0,1;0rad)
FEATURE [Part::FeaturePython] Tube098  # WARN: FeaturePython — macro-defined, semantics opaque (R4)
  AttacherType = Attacher::AttachEngine3D
  Height = 5
  InnerRadius = 24
  OuterRadius = 58
  Placement = pos=(0,0,27) rot=(0,0,1;0rad)
FEATURE [Part::Cut] Cut735
  Base = -> Tube098
  Tool = -> Compound1142
FEATURE [Part::Cylinder] Cylinder2250  label="Válec2250"
  Angle = 360
  AttacherType = Attacher::AttachEngine3D
  Height = 40
  Placement = pos=(103,-12,-20) rot=(0,0,1;0rad)
  Radius = 4
FEATURE [Part::Cylinder] Cylinder2251  label="Válec2251"
  Angle = 360
  AttacherType = Attacher::AttachEngine3D
  Height = 40
  Placement = pos=(76,24,-18) rot=(0,0,1;0rad)
  Radius = 4
FEATURE [Part::Cylinder] Cylinder2252  label="Válec2252"
  Angle = 360
  AttacherType = Attacher::AttachEngine3D
  Height = 40
  Placement = pos=(1,12,-18) rot=(0,0,1;0rad)
  Radius = 4
FEATURE [Part::Cylinder] Cylinder2253  label="Válec2253"
  Angle = 360
  AttacherType = Attacher::AttachEngine3D
  Height = 40
  Placement = pos=(13,-27,-18) rot=(0,0,1;0rad)
  Radius = 4
FEATURE [Part::Cylinder] Cylinder2254  label="Válec2254"
  Angle = 360
  AttacherType = Attacher::AttachEngine3D
  Height = 40
  Placement = pos=(91,-27,-18) rot=(0,0,1;0rad)
  Radius = 4
FEATURE [Part::Compound] Compound1144  label="srouby_monoblok_silne008"
  Links = -> [Cylinder2250,Cylinder2249,Cylinder2251,Cylinder2254,Cylinder2253,Cylinder2248,Cylinder2247,Cylinder2252]
  Placement = pos=(0,0,20) rot=(0,0,1;0rad)
FEATURE [Part::Box] Box1054  label="Krychle1054"
  AttacherType = Attacher::AttachEngine3D
  Height = 20
  Length = 6
  Placement = pos=(13,31,0) rot=(0,0,1;0rad)
  Width = 6
FEATURE [Part::Box] Box1055  label="Krychle1055"
  AttacherType = Attacher::AttachEngine3D
  Height = 20
  Length = 6
  Placement = pos=(7,-39,0) rot=(0,0,1;0rad)
  Width = 6
FEATURE [Part::Box] Box1056  label="Krychle1056"
  AttacherType = Attacher::AttachEngine3D
  Height = 20
  Length = 6
  Placement = pos=(-37,13,0) rot=(0,0,1;0rad)
  Width = 6
FEATURE [Part::Box] Box1057  label="Krychle1057"
  AttacherType = Attacher::AttachEngine3D
  Height = 20
  Length = 6
  Placement = pos=(-19,31,0) rot=(0,0,1;0rad)
  Width = 6
FEATURE [Part::Box] Box1058  label="Krychle1058"
  AttacherType = Attacher::AttachEngine3D
  Height = 20
  Length = 6
  Placement = pos=(-19,-37,0) rot=(0,0,1;0rad)
  Width = 6
FEATURE [Part::Box] Box1059  label="Krychle1059"
  AttacherType = Attacher::AttachEngine3D
  Height = 20
  Length = 6
  Placement = pos=(31,13,0) rot=(0,0,1;0rad)
  Width = 6
FEATURE [Part::Box] Box1060  label="Krychle1060"
  AttacherType = Attacher::AttachEngine3D
  Height = 20
  Length = 6
  Placement = pos=(31,-19,0) rot=(0,0,1;0rad)
  Width = 6
FEATURE [Part::Box] Box1061  label="Krychle1061"
  AttacherType = Attacher::AttachEngine3D
  Height = 20
  Length = 6
  Placement = pos=(-37,-19,0) rot=(0,0,1;0rad)
  Width = 6
FEATURE [Part::Compound] Compound1145
  Links = -> [Box1054,Box1057,Box1058,Box1055,Box1059,Box1060,Box1056,Box1061]
  Placement = pos=(0,0,22) rot=(0,0,1;0rad)
FEATURE [Part::Cut] Cut734
  Base = -> Tube097
  Tool = -> Compound1145
FEATURE [Part::Chamfer] Chamfer091
  Base = -> Cut734
  Edges = 1 edges r=1: [Edge3]
FEATURE [Part::Cut] Cut733
  Base = -> Chamfer091
  Tool = -> Compound1141
FEATURE [Part::Box] Box1062  label="Krychle1062"
  AttacherType = Attacher::AttachEngine3D
  Height = 2
  Length = 6
  Placement = pos=(-3,-43,5) rot=(0,0,1;0rad)
  Width = 8
FEATURE [Part::Box] Box1063  label="Krychle1063"
  AttacherType = Attacher::AttachEngine3D
  Height = 2
  Length = 6
  Placement = pos=(28.2843,-32.5269,5) rot=(0,0,1;0.785398rad)
  Width = 8
FEATURE [Part::Box] Box1064  label="Krychle1064"
  AttacherType = Attacher::AttachEngine3D
  Height = 2
  Length = 6
  Placement = pos=(43,-3,5) rot=(0,0,1;1.5708rad)
  Width = 8
FEATURE [Part::Box] Box1065  label="Krychle1065"
  AttacherType = Attacher::AttachEngine3D
  Height = 2
  Length = 6
  Placement = pos=(27.1212,33.5028,5) rot=(0,0,1;2.53073rad)
  Width = 8
FEATURE [Part::Box] Box1066  label="Krychle1066"
  AttacherType = Attacher::AttachEngine3D
  Height = 2
  Length = 6
  Placement = pos=(3,43,5) rot=(0,0,1;3.14159rad)
  Width = 8
FEATURE [Part::Box] Box1067  label="Krychle1067"
  AttacherType = Attacher::AttachEngine3D
  Height = 2
  Length = 6
  Placement = pos=(-28.2843,32.5269,5) rot=(0,0,1;3.92699rad)
  Width = 8
FEATURE [Part::Box] Box1068  label="Krychle1068"
  AttacherType = Attacher::AttachEngine3D
  Height = 2
  Length = 6
  Placement = pos=(-43,3,5) rot=(0,0,-1;1.5708rad)
  Width = 8
FEATURE [Part::Box] Box1069  label="Krychle1069"
  AttacherType = Attacher::AttachEngine3D
  Height = 2
  Length = 6
  Placement = pos=(-32.5269,-28.2843,5) rot=(0,0,-1;0.785398rad)
  Width = 8
FEATURE [Part::Cylinder] Cylinder2255  label="Válec2255"
  Angle = 360
  AttacherType = Attacher::AttachEngine3D
  Height = 100
  Placement = pos=(0,-38,0) rot=(0,0,1;0rad)
  Radius = 1.5
FEATURE [Part::Cylinder] Cylinder2256  label="Válec2256"
  Angle = 360
  AttacherType = Attacher::AttachEngine3D
  Height = 100
  Placement = pos=(38,3e-15,0) rot=(0,0,1;1.5708rad)
  Radius = 1.5
FEATURE [Part::Cylinder] Cylinder2257  label="Válec2257"
  Angle = 360
  AttacherType = Attacher::AttachEngine3D
  Height = 100
  Placement = pos=(-1e-15,38,0) rot=(0,0,1;3.14159rad)
  Radius = 1.5
FEATURE [Part::Cylinder] Cylinder2258  label="Válec2258"
  Angle = 360
  AttacherType = Attacher::AttachEngine3D
  Height = 100
  Placement = pos=(26.8701,-26.8701,0) rot=(0,0,1;0.785398rad)
  Radius = 1.5
FEATURE [Part::Cylinder] Cylinder2259  label="Válec2259"
  Angle = 360
  AttacherType = Attacher::AttachEngine3D
  Height = 100
  Placement = pos=(21.7959,31.1278,0) rot=(0,0,1;2.53073rad)
  Radius = 1.5
FEATURE [Part::Cylinder] Cylinder2260  label="Válec2260"
  Angle = 360
  AttacherType = Attacher::AttachEngine3D
  Height = 100
  Placement = pos=(-26.8701,26.8701,0) rot=(0,0,1;3.92699rad)
  Radius = 1.5
FEATURE [Part::Cylinder] Cylinder2261  label="Válec2261"
  Angle = 360
  AttacherType = Attacher::AttachEngine3D
  Height = 100
  Placement = pos=(-38,-6e-15,0) rot=(0,0,-1;1.5708rad)
  Radius = 1.5
FEATURE [Part::Cylinder] Cylinder2262  label="Válec2262"
  Angle = 360
  AttacherType = Attacher::AttachEngine3D
  Height = 100
  Placement = pos=(-26.8701,-26.8701,0) rot=(0,0,-1;0.785398rad)
  Radius = 1.5
FEATURE [Part::Cylinder] Cylinder2263  label="Válec2263"
  Angle = 360
  AttacherType = Attacher::AttachEngine3D
  Height = 100
  Placement = pos=(0,-38,0) rot=(0,0,1;0rad)
  Radius = 1.5
FEATURE [Part::Cylinder] Cylinder2264  label="Válec2264"
  Angle = 360
  AttacherType = Attacher::AttachEngine3D
  Height = 100
  Placement = pos=(26.8701,-26.8701,0) rot=(0,0,1;0.785398rad)
  Radius = 1.5
FEATURE [Part::Cylinder] Cylinder2265  label="Válec2265"
  Angle = 360
  AttacherType = Attacher::AttachEngine3D
  Height = 100
  Placement = pos=(38,3e-15,0) rot=(0,0,1;1.5708rad)
  Radius = 1.5
FEATURE [Part::Cylinder] Cylinder2266  label="Válec2266"
  Angle = 360
  AttacherType = Attacher::AttachEngine3D
  Height = 100
  Placement = pos=(21.7959,31.1278,0) rot=(0,0,1;2.53073rad)
  Radius = 1.5
FEATURE [Part::Cylinder] Cylinder2267  label="Válec2267"
  Angle = 360
  AttacherType = Attacher::AttachEngine3D
  Height = 100
  Placement = pos=(-1e-15,38,0) rot=(0,0,1;3.14159rad)
  Radius = 1.5
FEATURE [Part::Cylinder] Cylinder2268  label="Válec2268"
  Angle = 360
  AttacherType = Attacher::AttachEngine3D
  Height = 100
  Placement = pos=(-26.8701,26.8701,0) rot=(0,0,1;3.92699rad)
  Radius = 1.5
FEATURE [Part::Cylinder] Cylinder2269  label="Válec2269"
  Angle = 360
  AttacherType = Attacher::AttachEngine3D
  Height = 100
  Placement = pos=(-38,-6e-15,0) rot=(0,0,-1;1.5708rad)
  Radius = 1.5
FEATURE [Part::Cylinder] Cylinder2270  label="Válec2270"
  Angle = 360
  AttacherType = Attacher::AttachEngine3D
  Height = 100
  Placement = pos=(-26.8701,-26.8701,0) rot=(0,0,-1;0.785398rad)
  Radius = 1.5
FEATURE [Part::Cut] Cut736
  Base = -> Cut735
  Tool = -> Compound1144
FEATURE [Part::Cut] Cut737
  Base = -> Cut733
  Tool = -> Compound1143
FEATURE [Part::Compound] Compound1146
  Links = -> [Box1062,Box1063,Box1064,Box1065,Box1066,Box1067,Box1068,Box1069]
  Placement = pos=(0,0,16) rot=(0,0,1;0rad)
FEATURE [Part::Compound] Compound1147
  Links = -> [Cylinder2265,Cylinder2268,Cylinder2269,Cylinder2267,Cylinder2270,Cylinder2263,Cylinder2264,Cylinder2266]
FEATURE [Part::Cut] Cut738
  Base = -> Cut737
  Tool = -> Compound1147
FEATURE [Part::Cut] Cut740
  Base = -> Cut738
  Tool = -> Compound1146
FEATURE [Part::Compound] Compound1148
  Links = -> [Cylinder2258,Cylinder2256,Cylinder2259,Cylinder2257,Cylinder2260,Cylinder2261,Cylinder2262,Cylinder2255]
FEATURE [Part::Cut] Cut739
  Base = -> Cut736
  Tool = -> Compound1148
FEATURE [Part::Chamfer] Chamfer092
  Base = -> Cut739
  Edges = 1 edges r=1: [Edge3]
FEATURE [Part::Cut] Cut741
  Base = -> Cut740
  Tool = -> Cylinder2231
FEATURE [Part::Cylinder] Cylinder2271  label="Válec2271"
  Angle = 360
  AttacherType = Attacher::AttachEngine3D
  Height = 160
  Placement = pos=(-18,0,-60) rot=(0,0,1;0rad)
  Radius = 17
FEATURE [Part::Cut] Cut742
  Base = -> Chamfer092
  Tool = -> Cylinder2271
FEATURE [Part::Fillet] Fillet005
  Base = -> Cut741
  Edges = 1 edges r=2: [Edge185]
FEATURE [Part::Fillet] Fillet006
  Base = -> Cut742
  Edges = 1 edges r=2: [Edge30]
FEATURE [Part::Compound] Compound1149  label="Base_inner-cylinder-holed-001"
  Links = -> [Fillet005,Fillet006]
FEATURE [Part::Cylinder] Cylinder2272  label="Válec2272"
  Angle = 360
  AttacherType = Attacher::AttachEngine3D
  Height = 100
  Placement = pos=(38,3e-15,0) rot=(0,0,1;1.5708rad)
  Radius = 1.5
FEATURE [Part::Cylinder] Cylinder2273  label="Válec2273"
  Angle = 360
  AttacherType = Attacher::AttachEngine3D
  Height = 100
  Placement = pos=(0,-38,0) rot=(0,0,1;0rad)
  Radius = 5
FEATURE [Part::Cylinder] Cylinder2274  label="Válec2274"
  Angle = 360
  AttacherType = Attacher::AttachEngine3D
  Height = 100
  Placement = pos=(-26.8701,26.8701,0) rot=(0,0,1;3.92699rad)
  Radius = 1.5
FEATURE [Part::Cylinder] Cylinder2275  label="Válec2275"
  Angle = 360
  AttacherType = Attacher::AttachEngine3D
  Height = 100
  Placement = pos=(-38,-6e-15,0) rot=(0,0,-1;1.5708rad)
  Radius = 5
FEATURE [Part::Cylinder] Cylinder2276  label="Válec2276"
  Angle = 360
  AttacherType = Attacher::AttachEngine3D
  Height = 100
  Placement = pos=(-38,-6e-15,0) rot=(0,0,-1;1.5708rad)
  Radius = 5
FEATURE [Part::Cylinder] Cylinder2277  label="Válec2277"
  Angle = 360
  AttacherType = Attacher::AttachEngine3D
  Height = 100
  Placement = pos=(0,-38,0) rot=(0,0,1;0rad)
  Radius = 1.5
FEATURE [Part::Cylinder] Cylinder2278  label="Válec2278"
  Angle = 360
  AttacherType = Attacher::AttachEngine3D
  Height = 100
  Placement = pos=(-1e-15,38,0) rot=(0,0,1;3.14159rad)
  Radius = 1.5
FEATURE [Part::Cylinder] Cylinder2279  label="Válec2279"
  Angle = 360
  AttacherType = Attacher::AttachEngine3D
  Height = 100
  Placement = pos=(26.8701,-26.8701,0) rot=(0,0,1;0.785398rad)
  Radius = 1.5
FEATURE [Part::Cylinder] Cylinder2280  label="Válec2280"
  Angle = 360
  AttacherType = Attacher::AttachEngine3D
  Height = 100
  Placement = pos=(26.8701,-26.8701,0) rot=(0,0,1;0.785398rad)
  Radius = 5
FEATURE [Part::Cylinder] Cylinder2281  label="Válec2281"
  Angle = 360
  AttacherType = Attacher::AttachEngine3D
  Height = 100
  Placement = pos=(-26.8701,-26.8701,0) rot=(0,0,-1;0.785398rad)
  Radius = 1.5
FEATURE [Part::Cylinder] Cylinder2282  label="Válec2282"
  Angle = 360
  AttacherType = Attacher::AttachEngine3D
  Height = 100
  Placement = pos=(38,3e-15,0) rot=(0,0,1;1.5708rad)
  Radius = 5
FEATURE [Part::Cylinder] Cylinder2283  label="Válec2283"
  Angle = 360
  AttacherType = Attacher::AttachEngine3D
  Height = 100
  Placement = pos=(-26.8701,26.8701,0) rot=(0,0,1;3.92699rad)
  Radius = 5
FEATURE [Part::Cylinder] Cylinder2284  label="Válec2284"
  Angle = 360
  AttacherType = Attacher::AttachEngine3D
  Height = 100
  Placement = pos=(21.7959,31.1278,0) rot=(0,0,1;2.53073rad)
  Radius = 5
FEATURE [Part::Cylinder] Cylinder2285  label="Válec2285"
  Angle = 360
  AttacherType = Attacher::AttachEngine3D
  Height = 100
  Placement = pos=(-38,-6e-15,0) rot=(0,0,-1;1.5708rad)
  Radius = 1.5
FEATURE [Part::Cylinder] Cylinder2286  label="Válec2286"
  Angle = 360
  AttacherType = Attacher::AttachEngine3D
  Height = 100
  Placement = pos=(26.8701,-26.8701,0) rot=(0,0,1;0.785398rad)
  Radius = 5
FEATURE [Part::Cylinder] Cylinder2287  label="Válec2287"
  Angle = 360
  AttacherType = Attacher::AttachEngine3D
  Height = 100
  Placement = pos=(21.7959,31.1278,0) rot=(0,0,1;2.53073rad)
  Radius = 1.5
FEATURE [Part::Cylinder] Cylinder2288  label="Válec2288"
  Angle = 360
  AttacherType = Attacher::AttachEngine3D
  Height = 100
  Placement = pos=(-26.8701,-26.8701,0) rot=(0,0,-1;0.785398rad)
  Radius = 5
FEATURE [Part::Cylinder] Cylinder2289  label="Válec2289"
  Angle = 360
  AttacherType = Attacher::AttachEngine3D
  Height = 100
  Placement = pos=(-1e-15,38,0) rot=(0,0,1;3.14159rad)
  Radius = 5
FEATURE [Part::Cylinder] Cylinder2290  label="Válec2290"
  Angle = 360
  AttacherType = Attacher::AttachEngine3D
  Height = 100
  Placement = pos=(38,3e-15,0) rot=(0,0,1;1.5708rad)
  Radius = 5
FEATURE [Part::Cylinder] Cylinder2291  label="Válec2291"
  Angle = 360
  AttacherType = Attacher::AttachEngine3D
  Height = 100
  Placement = pos=(21.7959,31.1278,0) rot=(0,0,1;2.53073rad)
  Radius = 5
FEATURE [Part::Cylinder] Cylinder2292  label="Válec2292"
  Angle = 360
  AttacherType = Attacher::AttachEngine3D
  Height = 100
  Placement = pos=(-1e-15,38,0) rot=(0,0,1;3.14159rad)
  Radius = 5
FEATURE [Part::Cylinder] Cylinder2293  label="Válec2293"
  Angle = 360
  AttacherType = Attacher::AttachEngine3D
  Height = 100
  Placement = pos=(0,-38,0) rot=(0,0,1;0rad)
  Radius = 5
FEATURE [Part::Cylinder] Cylinder2294  label="Válec2294"
  Angle = 360
  AttacherType = Attacher::AttachEngine3D
  Height = 100
  Placement = pos=(-26.8701,26.8701,0) rot=(0,0,1;3.92699rad)
  Radius = 5
FEATURE [Part::Cylinder] Cylinder2295  label="Válec2295"
  Angle = 360
  AttacherType = Attacher::AttachEngine3D
  Height = 100
  Placement = pos=(-26.8701,-26.8701,0) rot=(0,0,-1;0.785398rad)
  Radius = 5
FEATURE [Part::Compound] Compound1150
  Links = -> [Cylinder2286,Cylinder2282,Cylinder2284,Cylinder2289,Cylinder2283,Cylinder2275,Cylinder2288,Cylinder2273]
  Placement = pos=(0,0,56) rot=(0,0,1;0rad)
FEATURE [Part::Compound] Compound1151
  Links = -> [Cylinder2280,Cylinder2290,Cylinder2291,Cylinder2292,Cylinder2294,Cylinder2276,Cylinder2295,Cylinder2293]
  Placement = pos=(0,0,56) rot=(0,0,1;0rad)
FEATURE [Part::Compound] Compound1153
  Links = -> [Cylinder2279,Cylinder2272,Cylinder2287,Cylinder2278,Cylinder2274,Cylinder2285,Cylinder2281,Cylinder2277]
FEATURE [Part::FeaturePython] Tube099  # WARN: FeaturePython — macro-defined, semantics opaque (R4)
  AttacherType = Attacher::AttachEngine3D
  Height = 3
  InnerRadius = 54
  OuterRadius = 61
  Placement = pos=(0,0,52) rot=(0,0,1;0rad)
FEATURE [Part::Chamfer] Chamfer093
  Base = -> Tube099
  Edges = 1 edges r=1: [Edge3]
FEATURE [Part::FeaturePython] Tube100  # WARN: FeaturePython — macro-defined, semantics opaque (R4)
  AttacherType = Attacher::AttachEngine3D
  Height = 4
  InnerRadius = 32
  OuterRadius = 58
  Placement = pos=(0,0,52) rot=(0,0,1;0rad)
FEATURE [Part::Cut] Cut745
  Base = -> Tube100
  Tool = -> Compound1150
FEATURE [Part::Cut] Cut744
  Base = -> Cut745
  Tool = -> Compound1153
FEATURE [Part::FeaturePython] Tube101  # WARN: FeaturePython — macro-defined, semantics opaque (R4)
  AttacherType = Attacher::AttachEngine3D
  Height = 8
  InnerRadius = 32
  OuterRadius = 42.6
  Placement = pos=(0,0,58) rot=(0,0,1;0rad)
FEATURE [Part::Chamfer] Chamfer097
  Base = -> Tube101
  Edges = 1 edges r=1: [Edge1]
FEATURE [Part::Cut] Cut743
  Base = -> Chamfer097
  Tool = -> Compound1151
FEATURE [Part::Chamfer] Chamfer094
  Base = -> Cut743
  Edges = 5 edges r=0.9: [Edge38,Edge39,Edge41,Edge42,Edge45]
FEATURE [Part::Chamfer] Chamfer096
  Base = -> Chamfer094
  Edges = 4 edges r=0.9: [Edge2,Edge5,Edge8,Edge11]
FEATURE [Part::Chamfer] Chamfer095
  Base = -> Chamfer096
  Edges = 1 edges r=0.9: [Edge14]
  Placement = pos=(0,0,-4) rot=(0,0,1;0rad)
FEATURE [Part::Compound] Compound1152  label="Base_inner-cylinder-belt-B-low-old"
  Links = -> [Cut744,Chamfer093,Chamfer095]
FEATURE [Part::Box] Box1070  label="Krychle1070"
  AttacherType = Attacher::AttachEngine3D
  Height = 7
  Length = 60
  Placement = pos=(0,0,-22) rot=(0,0,-1;0.349066rad)
  Width = 60
FEATURE [Part::Cylinder] Cylinder2296  label="Válec2296"
  Angle = 360
  AttacherType = Attacher::AttachEngine3D
  Height = 100
  Placement = pos=(0,-38,0) rot=(0,0,1;0rad)
  Radius = 1.5
FEATURE [Part::Cylinder] Cylinder2297  label="Válec2297"
  Angle = 360
  AttacherType = Attacher::AttachEngine3D
  Height = 100
  Placement = pos=(-1e-15,38,0) rot=(0,0,1;3.14159rad)
  Radius = 1.5
FEATURE [Part::Cylinder] Cylinder2298  label="Válec2298"
  Angle = 360
  AttacherType = Attacher::AttachEngine3D
  Height = 100
  Placement = pos=(26.8701,-26.8701,0) rot=(0,0,1;0.785398rad)
  Radius = 1.5
FEATURE [Part::Cylinder] Cylinder2299  label="Válec2299"
  Angle = 360
  AttacherType = Attacher::AttachEngine3D
  Height = 100
  Placement = pos=(-38,-6e-15,0) rot=(0,0,-1;1.5708rad)
  Radius = 1.5
FEATURE [Part::Cylinder] Cylinder2300  label="Válec2300"
  Angle = 360
  AttacherType = Attacher::AttachEngine3D
  Height = 7
  Placement = pos=(0,0,-22) rot=(0,0,1;0rad)
  Radius = 51
FEATURE [Part::Cylinder] Cylinder2301  label="Válec2301"
  Angle = 360
  AttacherType = Attacher::AttachEngine3D
  Height = 100
  Placement = pos=(-26.8701,26.8701,0) rot=(0,0,1;3.92699rad)
  Radius = 1.5
FEATURE [Part::Cylinder] Cylinder2302  label="Válec2302"
  Angle = 360
  AttacherType = Attacher::AttachEngine3D
  Height = 100
  Placement = pos=(-26.8701,-26.8701,0) rot=(0,0,-1;0.785398rad)
  Radius = 1.5
FEATURE [Part::Cylinder] Cylinder2303  label="Válec2303"
  Angle = 360
  AttacherType = Attacher::AttachEngine3D
  Height = 100
  Placement = pos=(21.7959,31.1278,0) rot=(0,0,1;2.53073rad)
  Radius = 1.5
FEATURE [Part::Cylinder] Cylinder2304  label="Válec2304"
  Angle = 360
  AttacherType = Attacher::AttachEngine3D
  Height = 100
  Placement = pos=(38,3e-15,0) rot=(0,0,1;1.5708rad)
  Radius = 1.5
FEATURE [Part::Box] Box1071  label="Krychle1071"
  AttacherType = Attacher::AttachEngine3D
  Height = 7
  Length = 120
  Placement = pos=(-60,-60,-22) rot=(0,0,-1;0rad)
  Width = 60
FEATURE [Part::Box] Box1072  label="Krychle1072"
  AttacherType = Attacher::AttachEngine3D
  Height = 7
  Length = 60
  Placement = pos=(-59.9909,-1.04714,-22) rot=(0,0,1;0.017453rad)
  Width = 60
FEATURE [Part::Box] Box1073  label="Krychle1073"
  AttacherType = Attacher::AttachEngine3D
  Height = 7
  Length = 120
  Placement = pos=(-60,-60,-22) rot=(0,0,-1;0rad)
  Width = 60
FEATURE [Part::Cylinder] Cylinder2305  label="Válec2305"
  Angle = 360
  AttacherType = Attacher::AttachEngine3D
  Height = 7
  Placement = pos=(0,0,45) rot=(0,0,1;0rad)
  Radius = 56
FEATURE [Part::Box] Box1074  label="Krychle1074"
  AttacherType = Attacher::AttachEngine3D
  Height = 7
  Length = 1.4
  Placement = pos=(0,0,-22) rot=(0,0,-1;0.314159rad)
  Width = 60
FEATURE [Part::Cylinder] Cylinder2306  label="Válec2306"
  Angle = 360
  AttacherType = Attacher::AttachEngine3D
  Height = 7
  Placement = pos=(0,0,-22) rot=(0,0,1;0rad)
  Radius = 51
FEATURE [Part::Box] Box1075  label="Krychle1075"
  AttacherType = Attacher::AttachEngine3D
  Height = 7
  Length = 1.4
  Placement = pos=(0,0,-22) rot=(0,0,1;0.34383rad)
  Width = 60
FEATURE [Part::Box] Box1076  label="Krychle1076"
  AttacherType = Attacher::AttachEngine3D
  Height = 7
  Length = 1.4
  Placement = pos=(0,0,-22) rot=(0,0,1;0.047124rad)
  Width = 60
FEATURE [Part::Box] Box1077  label="Krychle1077"
  AttacherType = Attacher::AttachEngine3D
  Height = 7
  Length = 60
  Placement = pos=(-56.3816,-20.5212,-22) rot=(0,0,1;0.349066rad)
  Width = 60
FEATURE [Part::Box] Box1078  label="Krychle1078"
  AttacherType = Attacher::AttachEngine3D
  Height = 7
  Length = 60
  Placement = pos=(0,0,-22) rot=(0,0,-1;0.034907rad)
  Width = 60
FEATURE [Part::Box] Box1079  label="Krychle1079"
  AttacherType = Attacher::AttachEngine3D
  Height = 7
  Length = 1.4
  Placement = pos=(0,0,-22) rot=(0,0,-1;0.034907rad)
  Width = 60
FEATURE [Part::Compound] Compound1155
  Links = -> [Box1078,Box1072]
FEATURE [Part::Compound] Compound1156
  Links = -> [Cylinder2298,Cylinder2304,Cylinder2303,Cylinder2297,Cylinder2301,Cylinder2299,Cylinder2302,Cylinder2296]
FEATURE [Part::Compound] Compound1157
  Links = -> [Box1079,Box1076]
FEATURE [Part::Compound] Compound1158
  Links = -> [Box1070,Box1077]
FEATURE [Part::Compound] Compound1159
  Links = -> [Box1074,Box1075]
FEATURE [Part::Cut] Cut748
  Base = -> Compound1157
  Placement = pos=(0,0,67) rot=(0,0,1;0.785398rad)
  Tool = -> Cylinder2300
FEATURE [Part::Cut] Cut749
  Base = -> Compound1159
  Placement = pos=(0,0,67) rot=(0,0,1;0.785398rad)
  Tool = -> Cylinder2306
FEATURE [Part::Common] Common001
  Base = -> Cut749
  Tool = -> Cylinder2305
FEATURE [Part::FeaturePython] Tube102  # WARN: FeaturePython — macro-defined, semantics opaque (R4)
  AttacherType = Attacher::AttachEngine3D
  Height = 10
  InnerRadius = 32
  OuterRadius = 57
  Placement = pos=(0,0,42) rot=(0,0,1;0rad)
FEATURE [Part::Cut] Cut752
  Base = -> Tube102
  Tool = -> Compound1156
FEATURE [Part::Cut] Cut751
  Base = -> Cut752
  Tool = -> Cut748
FEATURE [Part::FeaturePython] Tube103  # WARN: FeaturePython — macro-defined, semantics opaque (R4)
  AttacherType = Attacher::AttachEngine3D
  Height = 7
  InnerRadius = 52
  OuterRadius = 53.4
  Placement = pos=(0,0,-22) rot=(0,0,1;0rad)
FEATURE [Part::Cut] Cut747
  Base = -> Tube103
  Tool = -> Box1071
FEATURE [Part::Cut] Cut750
  Base = -> Cut747
  Placement = pos=(0,0,-7) rot=(0,0,1;0rad)
  Tool = -> Compound1158
FEATURE [Part::FeaturePython] Tube104  # WARN: FeaturePython — macro-defined, semantics opaque (R4)
  AttacherType = Attacher::AttachEngine3D
  Height = 3
  InnerRadius = 54
  OuterRadius = 61
  Placement = pos=(0,0,42) rot=(0,0,1;0rad)
FEATURE [Part::Chamfer] Chamfer098
  Base = -> Tube104
  Edges = 1 edges r=1: [Edge1]
FEATURE [Part::FeaturePython] Tube105  # WARN: FeaturePython — macro-defined, semantics opaque (R4)
  AttacherType = Attacher::AttachEngine3D
  Height = 7
  InnerRadius = 52
  OuterRadius = 54.4
  Placement = pos=(0,0,-22) rot=(0,0,1;0rad)
FEATURE [Part::Cut] Cut753
  Base = -> Tube105
  Tool = -> Box1073
FEATURE [Part::Cut] Cut746
  Base = -> Cut753
  Placement = pos=(0,0,-7) rot=(0,0,1;0rad)
  Tool = -> Compound1155
FEATURE [Part::Cut] Cut755
  Base = -> Cut750
  Placement = pos=(0,0,74) rot=(0,0,1;0.785398rad)
  Tool = -> Cut746
FEATURE [Part::Cut] Cut754
  Base = -> Cut751
  Tool = -> Cut755
FEATURE [Part::Cut] Cut756
  Base = -> Cut754
  Tool = -> Common001
FEATURE [Part::Compound] Compound1154  label="Base_inner-cylinder-belt-A-old001"
  Links = -> [Cut756,Chamfer098]
  Placement = pos=(0,0,1) rot=(0,0,1;0rad)
FEATURE [Part::Cylinder] Cylinder2307  label="Válec2307"
  Angle = 360
  AttacherType = Attacher::AttachEngine3D
  Height = 40
  Placement = pos=(91,-27,-18) rot=(0,0,1;0rad)
  Radius = 4
FEATURE [Part::Cylinder] Cylinder2308  label="Válec2308"
  Angle = 360
  AttacherType = Attacher::AttachEngine3D
  Height = 160
  Placement = pos=(-18,0,-60) rot=(0,0,1;0rad)
  Radius = 17
FEATURE [Part::Cylinder] Cylinder2309  label="Válec2309"
  Angle = 360
  AttacherType = Attacher::AttachEngine3D
  Height = 100
  Placement = pos=(-16,-34,-60) rot=(0,0,1;0rad)
  Radius = 1.5
FEATURE [Part::Cylinder] Cylinder2310  label="Válec2310"
  Angle = 360
  AttacherType = Attacher::AttachEngine3D
  Height = 100
  Placement = pos=(10,-36,-60) rot=(0,0,1;0rad)
  Radius = 1.5
FEATURE [Part::Box] Box1080  label="Krychle1080"
  AttacherType = Attacher::AttachEngine3D
  Height = 20
  Length = 6
  Placement = pos=(13,31,0) rot=(0,0,1;0rad)
  Width = 6
FEATURE [Part::Box] Box1081  label="Krychle1081"
  AttacherType = Attacher::AttachEngine3D
  Height = 20
  Length = 6
  Placement = pos=(-19,-37,0) rot=(0,0,1;0rad)
  Width = 6
FEATURE [Part::Cylinder] Cylinder2311  label="Válec2311"
  Angle = 360
  AttacherType = Attacher::AttachEngine3D
  Height = 100
  Placement = pos=(16,34,-60) rot=(0,0,1;0rad)
  Radius = 1.5
FEATURE [Part::Cylinder] Cylinder2312  label="Válec2312"
  Angle = 360
  AttacherType = Attacher::AttachEngine3D
  Height = 100
  Placement = pos=(-34,-16,-60) rot=(0,0,1;0rad)
  Radius = 1.5
FEATURE [Part::Cylinder] Cylinder2313  label="Válec2313"
  Angle = 360
  AttacherType = Attacher::AttachEngine3D
  Height = 100
  Placement = pos=(34,16,-60) rot=(0,0,1;0rad)
  Radius = 1.5
FEATURE [Part::Cylinder] Cylinder2314  label="Válec2314"
  Angle = 360
  AttacherType = Attacher::AttachEngine3D
  Height = 100
  Placement = pos=(-34,16,-60) rot=(0,0,1;0rad)
  Radius = 1.5
FEATURE [Part::Cylinder] Cylinder2315  label="Válec2315"
  Angle = 360
  AttacherType = Attacher::AttachEngine3D
  Height = 100
  Placement = pos=(-16,34,-60) rot=(0,0,1;0rad)
  Radius = 1.5
FEATURE [Part::Box] Box1082  label="Krychle1082"
  AttacherType = Attacher::AttachEngine3D
  Height = 20
  Length = 6
  Placement = pos=(-19,31,0) rot=(0,0,1;0rad)
  Width = 6
FEATURE [Part::Box] Box1083  label="Krychle1083"
  AttacherType = Attacher::AttachEngine3D
  Height = 20
  Length = 6
  Placement = pos=(7,-39,0) rot=(0,0,1;0rad)
  Width = 6
FEATURE [Part::Cylinder] Cylinder2316  label="Válec2316"
  Angle = 360
  AttacherType = Attacher::AttachEngine3D
  Height = 100
  Placement = pos=(34,-16,-60) rot=(0,0,1;0rad)
  Radius = 1.5
FEATURE [Part::Cylinder] Cylinder2317  label="Válec2317"
  Angle = 360
  AttacherType = Attacher::AttachEngine3D
  Height = 40
  Placement = pos=(1,-12,-18) rot=(0,0,1;0rad)
  Radius = 4
FEATURE [Part::Cylinder] Cylinder2318  label="Válec2318"
  Angle = 360
  AttacherType = Attacher::AttachEngine3D
  Height = 40
  Placement = pos=(1,12,-18) rot=(0,0,1;0rad)
  Radius = 4
FEATURE [Part::Box] Box1084  label="Krychle1084"
  AttacherType = Attacher::AttachEngine3D
  Height = 20
  Length = 6
  Placement = pos=(31,-19,0) rot=(0,0,1;0rad)
  Width = 6
FEATURE [Part::Box] Box1085  label="Krychle1085"
  AttacherType = Attacher::AttachEngine3D
  Height = 20
  Length = 6
  Placement = pos=(-37,13,0) rot=(0,0,1;0rad)
  Width = 6
FEATURE [Part::Box] Box1086  label="Krychle1086"
  AttacherType = Attacher::AttachEngine3D
  Height = 20
  Length = 6
  Placement = pos=(-37,-19,0) rot=(0,0,1;0rad)
  Width = 6
FEATURE [Part::Box] Box1087  label="Krychle1087"
  AttacherType = Attacher::AttachEngine3D
  Height = 20
  Length = 6
  Placement = pos=(31,13,0) rot=(0,0,1;0rad)
  Width = 6
FEATURE [Part::Cylinder] Cylinder2319  label="Válec2319"
  Angle = 360
  AttacherType = Attacher::AttachEngine3D
  Height = 40
  Placement = pos=(91,-27,-18) rot=(0,0,1;0rad)
  Radius = 4
FEATURE [Part::FeaturePython] Tube106  # WARN: FeaturePython — macro-defined, semantics opaque (R4)
  AttacherType = Attacher::AttachEngine3D
  Height = 5
  InnerRadius = 24
  OuterRadius = 58
  Placement = pos=(0,0,27) rot=(0,0,1;0rad)
FEATURE [Part::FeaturePython] Tube107  # WARN: FeaturePython — macro-defined, semantics opaque (R4)
  AttacherType = Attacher::AttachEngine3D
  Height = 22
  InnerRadius = 24
  OuterRadius = 42.65
  Placement = pos=(0,0,5) rot=(0,0,1;0rad)
FEATURE [Part::Box] Box1088  label="Krychle1088"
  AttacherType = Attacher::AttachEngine3D
  Height = 20
  Length = 6
  Placement = pos=(-19,31,0) rot=(0,0,1;0rad)
  Width = 6
FEATURE [Part::Cylinder] Cylinder2320  label="Válec2320"
  Angle = 360
  AttacherType = Attacher::AttachEngine3D
  Height = 40
  Placement = pos=(76,24,-18) rot=(0,0,1;0rad)
  Radius = 4
FEATURE [Part::Box] Box1089  label="Krychle1089"
  AttacherType = Attacher::AttachEngine3D
  Height = 20
  Length = 6
  Placement = pos=(7,-39,0) rot=(0,0,1;0rad)
  Width = 6
FEATURE [Part::Box] Box1090  label="Krychle1090"
  AttacherType = Attacher::AttachEngine3D
  Height = 20
  Length = 6
  Placement = pos=(-37,-19,0) rot=(0,0,1;0rad)
  Width = 6
FEATURE [Part::Box] Box1091  label="Krychle1091"
  AttacherType = Attacher::AttachEngine3D
  Height = 20
  Length = 6
  Placement = pos=(13,31,0) rot=(0,0,1;0rad)
  Width = 6
FEATURE [Part::Cylinder] Cylinder2321  label="Válec2321"
  Angle = 360
  AttacherType = Attacher::AttachEngine3D
  Height = 40
  Placement = pos=(76,24,-18) rot=(0,0,1;0rad)
  Radius = 4
FEATURE [Part::Box] Box1092  label="Krychle1092"
  AttacherType = Attacher::AttachEngine3D
  Height = 20
  Length = 6
  Placement = pos=(31,13,0) rot=(0,0,1;0rad)
  Width = 6
FEATURE [Part::Cylinder] Cylinder2322  label="Válec2322"
  Angle = 360
  AttacherType = Attacher::AttachEngine3D
  Height = 40
  Placement = pos=(1,12,-18) rot=(0,0,1;0rad)
  Radius = 4
FEATURE [Part::Cylinder] Cylinder2323  label="Válec2323"
  Angle = 360
  AttacherType = Attacher::AttachEngine3D
  Height = 40
  Placement = pos=(103,-12,-20) rot=(0,0,1;0rad)
  Radius = 4
FEATURE [Part::Cylinder] Cylinder2324  label="Válec2324"
  Angle = 360
  AttacherType = Attacher::AttachEngine3D
  Height = 40
  Placement = pos=(103,-12,-20) rot=(0,0,1;0rad)
  Radius = 4
FEATURE [Part::Cylinder] Cylinder2325  label="Válec2325"
  Angle = 360
  AttacherType = Attacher::AttachEngine3D
  Height = 40
  Placement = pos=(103,12,-20) rot=(0,0,1;0rad)
  Radius = 4
FEATURE [Part::Cylinder] Cylinder2326  label="Válec2326"
  Angle = 360
  AttacherType = Attacher::AttachEngine3D
  Height = 40
  Placement = pos=(28,24,-18) rot=(0,0,1;0rad)
  Radius = 4
FEATURE [Part::Cylinder] Cylinder2327  label="Válec2327"
  Angle = 360
  AttacherType = Attacher::AttachEngine3D
  Height = 40
  Placement = pos=(103,12,-20) rot=(0,0,1;0rad)
  Radius = 4
FEATURE [Part::Cylinder] Cylinder2328  label="Válec2328"
  Angle = 360
  AttacherType = Attacher::AttachEngine3D
  Height = 40
  Placement = pos=(13,-27,-18) rot=(0,0,1;0rad)
  Radius = 4
FEATURE [Part::Cylinder] Cylinder2329  label="Válec2329"
  Angle = 360
  AttacherType = Attacher::AttachEngine3D
  Height = 40
  Placement = pos=(13,-27,-18) rot=(0,0,1;0rad)
  Radius = 4
FEATURE [Part::Cylinder] Cylinder2330  label="Válec2330"
  Angle = 360
  AttacherType = Attacher::AttachEngine3D
  Height = 40
  Placement = pos=(28,24,-18) rot=(0,0,1;0rad)
  Radius = 4
FEATURE [Part::Cylinder] Cylinder2331  label="Válec2331"
  Angle = 360
  AttacherType = Attacher::AttachEngine3D
  Height = 40
  Placement = pos=(1,-12,-18) rot=(0,0,1;0rad)
  Radius = 4
FEATURE [Part::Box] Box1093  label="Krychle1093"
  AttacherType = Attacher::AttachEngine3D
  Height = 20
  Length = 6
  Placement = pos=(-37,13,0) rot=(0,0,1;0rad)
  Width = 6
FEATURE [Part::Box] Box1094  label="Krychle1094"
  AttacherType = Attacher::AttachEngine3D
  Height = 20
  Length = 6
  Placement = pos=(-19,-37,0) rot=(0,0,1;0rad)
  Width = 6
FEATURE [Part::Box] Box1095  label="Krychle1095"
  AttacherType = Attacher::AttachEngine3D
  Height = 20
  Length = 6
  Placement = pos=(31,-19,0) rot=(0,0,1;0rad)
  Width = 6
FEATURE [Part::Cylinder] Cylinder2332  label="Válec2332"
  Angle = 360
  AttacherType = Attacher::AttachEngine3D
  Height = 100
  Placement = pos=(-26.8701,26.8701,0) rot=(0,0,1;3.92699rad)
  Radius = 1.5
FEATURE [Part::Cylinder] Cylinder2333  label="Válec2333"
  Angle = 360
  AttacherType = Attacher::AttachEngine3D
  Height = 100
  Placement = pos=(21.7959,31.1278,0) rot=(0,0,1;2.53073rad)
  Radius = 1.5
FEATURE [Part::Box] Box1096  label="Krychle1096"
  AttacherType = Attacher::AttachEngine3D
  Height = 2
  Length = 6
  Placement = pos=(27.1212,33.5028,5) rot=(0,0,1;2.53073rad)
  Width = 8
FEATURE [Part::Cylinder] Cylinder2334  label="Válec2334"
  Angle = 360
  AttacherType = Attacher::AttachEngine3D
  Height = 100
  Placement = pos=(0,-38,0) rot=(0,0,1;0rad)
  Radius = 1.5
FEATURE [Part::Box] Box1097  label="Krychle1097"
  AttacherType = Attacher::AttachEngine3D
  Height = 2
  Length = 6
  Placement = pos=(3,43,5) rot=(0,0,1;3.14159rad)
  Width = 8
FEATURE [Part::Box] Box1098  label="Krychle1098"
  AttacherType = Attacher::AttachEngine3D
  Height = 2
  Length = 6
  Placement = pos=(-3,-43,5) rot=(0,0,1;0rad)
  Width = 8
FEATURE [Part::Box] Box1099  label="Krychle1099"
  AttacherType = Attacher::AttachEngine3D
  Height = 2
  Length = 6
  Placement = pos=(-28.2843,32.5269,5) rot=(0,0,1;3.92699rad)
  Width = 8
FEATURE [Part::Box] Box1100  label="Krychle1100"
  AttacherType = Attacher::AttachEngine3D
  Height = 2
  Length = 6
  Placement = pos=(-32.5269,-28.2843,5) rot=(0,0,-1;0.785398rad)
  Width = 8
FEATURE [Part::Box] Box1101  label="Krychle1101"
  AttacherType = Attacher::AttachEngine3D
  Height = 2
  Length = 6
  Placement = pos=(43,-3,5) rot=(0,0,1;1.5708rad)
  Width = 8
FEATURE [Part::Cylinder] Cylinder2335  label="Válec2335"
  Angle = 360
  AttacherType = Attacher::AttachEngine3D
  Height = 100
  Placement = pos=(26.8701,-26.8701,0) rot=(0,0,1;0.785398rad)
  Radius = 1.5
FEATURE [Part::Cylinder] Cylinder2336  label="Válec2336"
  Angle = 360
  AttacherType = Attacher::AttachEngine3D
  Height = 100
  Placement = pos=(0,-38,0) rot=(0,0,1;0rad)
  Radius = 1.5
FEATURE [Part::Cylinder] Cylinder2337  label="Válec2337"
  Angle = 360
  AttacherType = Attacher::AttachEngine3D
  Height = 100
  Placement = pos=(-1e-15,38,0) rot=(0,0,1;3.14159rad)
  Radius = 1.5
FEATURE [Part::Cylinder] Cylinder2338  label="Válec2338"
  Angle = 360
  AttacherType = Attacher::AttachEngine3D
  Height = 100
  Placement = pos=(-26.8701,26.8701,0) rot=(0,0,1;3.92699rad)
  Radius = 1.5
FEATURE [Part::Cylinder] Cylinder2339  label="Válec2339"
  Angle = 360
  AttacherType = Attacher::AttachEngine3D
  Height = 100
  Placement = pos=(38,3e-15,0) rot=(0,0,1;1.5708rad)
  Radius = 1.5
FEATURE [Part::Cylinder] Cylinder2340  label="Válec2340"
  Angle = 360
  AttacherType = Attacher::AttachEngine3D
  Height = 100
  Placement = pos=(-26.8701,-26.8701,0) rot=(0,0,-1;0.785398rad)
  Radius = 1.5
FEATURE [Part::Box] Box1102  label="Krychle1102"
  AttacherType = Attacher::AttachEngine3D
  Height = 2
  Length = 6
  Placement = pos=(-43,3,5) rot=(0,0,-1;1.5708rad)
  Width = 8
FEATURE [Part::Box] Box1103  label="Krychle1103"
  AttacherType = Attacher::AttachEngine3D
  Height = 2
  Length = 6
  Placement = pos=(28.2843,-32.5269,5) rot=(0,0,1;0.785398rad)
  Width = 8
FEATURE [Part::Cylinder] Cylinder2341  label="Válec2341"
  Angle = 360
  AttacherType = Attacher::AttachEngine3D
  Height = 100
  Placement = pos=(-26.8701,-26.8701,0) rot=(0,0,-1;0.785398rad)
  Radius = 1.5
FEATURE [Part::Cylinder] Cylinder2342  label="Válec2342"
  Angle = 360
  AttacherType = Attacher::AttachEngine3D
  Height = 100
  Placement = pos=(-38,-6e-15,0) rot=(0,0,-1;1.5708rad)
  Radius = 1.5
FEATURE [Part::Cylinder] Cylinder2343  label="Válec2343"
  Angle = 360
  AttacherType = Attacher::AttachEngine3D
  Height = 100
  Placement = pos=(-1e-15,38,0) rot=(0,0,1;3.14159rad)
  Radius = 1.5
FEATURE [Part::Cylinder] Cylinder2344  label="Válec2344"
  Angle = 360
  AttacherType = Attacher::AttachEngine3D
  Height = 100
  Placement = pos=(38,3e-15,0) rot=(0,0,1;1.5708rad)
  Radius = 1.5
FEATURE [Part::Cylinder] Cylinder2345  label="Válec2345"
  Angle = 360
  AttacherType = Attacher::AttachEngine3D
  Height = 100
  Placement = pos=(21.7959,31.1278,0) rot=(0,0,1;2.53073rad)
  Radius = 1.5
FEATURE [Part::Cylinder] Cylinder2346  label="Válec2346"
  Angle = 360
  AttacherType = Attacher::AttachEngine3D
  Height = 100
  Placement = pos=(-38,-6e-15,0) rot=(0,0,-1;1.5708rad)
  Radius = 1.5
FEATURE [Part::Cylinder] Cylinder2347  label="Válec2347"
  Angle = 360
  AttacherType = Attacher::AttachEngine3D
  Height = 100
  Placement = pos=(26.8701,-26.8701,0) rot=(0,0,1;0.785398rad)
  Radius = 1.5
FEATURE [Part::Cylinder] Cylinder2348  label="Válec2348"
  Angle = 360
  AttacherType = Attacher::AttachEngine3D
  Height = 160
  Placement = pos=(-18,0,-60) rot=(0,0,1;0rad)
  Radius = 17
FEATURE [Part::Compound] Compound1161  label="srouby_monoblok_silne009"
  Links = -> [Cylinder2323,Cylinder2325,Cylinder2321,Cylinder2319,Cylinder2328,Cylinder2330,Cylinder2317,Cylinder2322]
  Placement = pos=(0,0,20) rot=(0,0,1;0rad)
FEATURE [Part::Compound] Compound1162  label="srouby_monoblok_silne010"
  Links = -> [Cylinder2324,Cylinder2327,Cylinder2320,Cylinder2307,Cylinder2329,Cylinder2326,Cylinder2331,Cylinder2318]
  Placement = pos=(0,0,20) rot=(0,0,1;0rad)
FEATURE [Part::Compound] Compound1163
  Links = -> [Cylinder2344,Cylinder2332,Cylinder2346,Cylinder2343,Cylinder2341,Cylinder2334,Cylinder2347,Cylinder2345]
FEATURE [Part::Compound] Compound1164
  Links = -> [Box1080,Box1082,Box1081,Box1083,Box1087,Box1084,Box1085,Box1086]
  Placement = pos=(0,0,22) rot=(0,0,1;0rad)
FEATURE [Part::Cut] Cut759
  Base = -> Tube106
  Tool = -> Compound1164
FEATURE [Part::Cut] Cut765
  Base = -> Cut759
  Tool = -> Compound1162
FEATURE [Part::Compound] Compound1165
  Links = -> [Box1098,Box1103,Box1101,Box1096,Box1097,Box1099,Box1102,Box1100]
  Placement = pos=(0,0,16) rot=(0,0,1;0rad)
FEATURE [Part::Compound] Compound1166
  Links = -> [Box1091,Box1088,Box1094,Box1089,Box1092,Box1095,Box1093,Box1090]
  Placement = pos=(0,0,22) rot=(0,0,1;0rad)
FEATURE [Part::Cut] Cut763
  Base = -> Tube107
  Tool = -> Compound1166
FEATURE [Part::Compound] Compound1167
  Links = -> [Cylinder2335,Cylinder2339,Cylinder2333,Cylinder2337,Cylinder2338,Cylinder2342,Cylinder2340,Cylinder2336]
FEATURE [Part::Cut] Cut758
  Base = -> Cut765
  Tool = -> Compound1167
FEATURE [Part::Chamfer] Chamfer099
  Base = -> Cut758
  Edges = 1 edges r=1: [Edge3]
FEATURE [Part::Cut] Cut762
  Base = -> Chamfer099
  Tool = -> Cylinder2348
FEATURE [Part::Fillet] Fillet007
  Base = -> Cut762
  Edges = 1 edges r=2: [Edge30]
FEATURE [Part::Chamfer] Chamfer100
  Base = -> Cut763
  Edges = 1 edges r=1: [Edge3]
FEATURE [Part::Compound] Compound1168  label="sbouby_baze012"
  Links = -> [Cylinder2314,Cylinder2312,Cylinder2316,Cylinder2313,Cylinder2311,Cylinder2310,Cylinder2309,Cylinder2315]
  Placement = pos=(0,0,40) rot=(0,0,1;0rad)
FEATURE [Part::Cut] Cut761
  Base = -> Chamfer100
  Tool = -> Compound1168
FEATURE [Part::Cut] Cut760
  Base = -> Cut761
  Tool = -> Compound1161
FEATURE [Part::Cut] Cut766
  Base = -> Cut760
  Tool = -> Compound1163
FEATURE [Part::Cut] Cut757
  Base = -> Cut766
  Tool = -> Compound1165
FEATURE [Part::Cut] Cut764
  Base = -> Cut757
  Tool = -> Cylinder2308
FEATURE [Part::Fillet] Fillet008
  Base = -> Cut764
  Edges = 1 edges r=2: [Edge185]
FEATURE [Part::Compound] Compound1160  label="Base_inner-cylinder-holed-002"
  Links = -> [Fillet008,Fillet007]
FEATURE [Part::Mirroring] mirror  label="Base_inner-cylinder-holed"
  Base = (0,0,0)
  Normal = (1e-16,-1,0)
  Source = -> Compound1160
FEATURE [Part::FeaturePython] Tube108  # WARN: FeaturePython — macro-defined, semantics opaque (R4)
  AttacherType = Attacher::AttachEngine3D
  Height = 4
  InnerRadius = 32
  OuterRadius = 58
  Placement = pos=(0,0,52) rot=(0,0,1;0rad)
FEATURE [Part::FeaturePython] Tube109  # WARN: FeaturePython — macro-defined, semantics opaque (R4)
  AttacherType = Attacher::AttachEngine3D
  Height = 3
  InnerRadius = 54
  OuterRadius = 61
  Placement = pos=(0,0,52) rot=(0,0,1;0rad)
FEATURE [Part::FeaturePython] Tube110  # WARN: FeaturePython — macro-defined, semantics opaque (R4)
  AttacherType = Attacher::AttachEngine3D
  Height = 8
  InnerRadius = 32
  OuterRadius = 42.6
  Placement = pos=(0,0,58) rot=(0,0,1;0rad)
FEATURE [Part::Cylinder] Cylinder2349  label="Válec2349"
  Angle = 360
  AttacherType = Attacher::AttachEngine3D
  Height = 100
  Placement = pos=(-38,-6e-15,0) rot=(0,0,-1;1.5708rad)
  Radius = 1.5
FEATURE [Part::Cylinder] Cylinder2350  label="Válec2350"
  Angle = 360
  AttacherType = Attacher::AttachEngine3D
  Height = 100
  Placement = pos=(0,-38,0) rot=(0,0,1;0rad)
  Radius = 1.5
FEATURE [Part::Cylinder] Cylinder2351  label="Válec2351"
  Angle = 360
  AttacherType = Attacher::AttachEngine3D
  Height = 100
  Placement = pos=(-38,-6e-15,0) rot=(0,0,-1;1.5708rad)
  Radius = 5
FEATURE [Part::Cylinder] Cylinder2352  label="Válec2352"
  Angle = 360
  AttacherType = Attacher::AttachEngine3D
  Height = 100
  Placement = pos=(38,3e-15,0) rot=(0,0,1;1.5708rad)
  Radius = 1.5
FEATURE [Part::Cylinder] Cylinder2353  label="Válec2353"
  Angle = 360
  AttacherType = Attacher::AttachEngine3D
  Height = 100
  Placement = pos=(0,-38,0) rot=(0,0,1;0rad)
  Radius = 5
FEATURE [Part::Cylinder] Cylinder2354  label="Válec2354"
  Angle = 360
  AttacherType = Attacher::AttachEngine3D
  Height = 100
  Placement = pos=(-26.8701,26.8701,0) rot=(0,0,1;3.92699rad)
  Radius = 1.5
FEATURE [Part::Cylinder] Cylinder2355  label="Válec2355"
  Angle = 360
  AttacherType = Attacher::AttachEngine3D
  Height = 100
  Placement = pos=(-1e-15,38,0) rot=(0,0,1;3.14159rad)
  Radius = 5
FEATURE [Part::Cylinder] Cylinder2356  label="Válec2356"
  Angle = 360
  AttacherType = Attacher::AttachEngine3D
  Height = 100
  Placement = pos=(-1e-15,38,0) rot=(0,0,1;3.14159rad)
  Radius = 1.5
FEATURE [Part::Cylinder] Cylinder2357  label="Válec2357"
  Angle = 360
  AttacherType = Attacher::AttachEngine3D
  Height = 100
  Placement = pos=(-26.8701,26.8701,0) rot=(0,0,1;3.92699rad)
  Radius = 5
FEATURE [Part::Cylinder] Cylinder2358  label="Válec2358"
  Angle = 360
  AttacherType = Attacher::AttachEngine3D
  Height = 100
  Placement = pos=(26.8701,-26.8701,0) rot=(0,0,1;0.785398rad)
  Radius = 5
FEATURE [Part::Cylinder] Cylinder2359  label="Válec2359"
  Angle = 360
  AttacherType = Attacher::AttachEngine3D
  Height = 100
  Placement = pos=(-38,-6e-15,0) rot=(0,0,-1;1.5708rad)
  Radius = 5
FEATURE [Part::Cylinder] Cylinder2360  label="Válec2360"
  Angle = 360
  AttacherType = Attacher::AttachEngine3D
  Height = 100
  Placement = pos=(-26.8701,-26.8701,0) rot=(0,0,-1;0.785398rad)
  Radius = 1.5
FEATURE [Part::Cylinder] Cylinder2361  label="Válec2361"
  Angle = 360
  AttacherType = Attacher::AttachEngine3D
  Height = 100
  Placement = pos=(21.7959,31.1278,0) rot=(0,0,1;2.53073rad)
  Radius = 1.5
FEATURE [Part::Cylinder] Cylinder2362  label="Válec2362"
  Angle = 360
  AttacherType = Attacher::AttachEngine3D
  Height = 100
  Placement = pos=(26.8701,-26.8701,0) rot=(0,0,1;0.785398rad)
  Radius = 1.5
FEATURE [Part::Cylinder] Cylinder2363  label="Válec2363"
  Angle = 360
  AttacherType = Attacher::AttachEngine3D
  Height = 100
  Placement = pos=(26.8701,-26.8701,0) rot=(0,0,1;0.785398rad)
  Radius = 5
FEATURE [Part::Cylinder] Cylinder2364  label="Válec2364"
  Angle = 360
  AttacherType = Attacher::AttachEngine3D
  Height = 100
  Placement = pos=(38,3e-15,0) rot=(0,0,1;1.5708rad)
  Radius = 5
FEATURE [Part::Cylinder] Cylinder2365  label="Válec2365"
  Angle = 360
  AttacherType = Attacher::AttachEngine3D
  Height = 100
  Placement = pos=(21.7959,31.1278,0) rot=(0,0,1;2.53073rad)
  Radius = 5
FEATURE [Part::Cylinder] Cylinder2366  label="Válec2366"
  Angle = 360
  AttacherType = Attacher::AttachEngine3D
  Height = 100
  Placement = pos=(-26.8701,-26.8701,0) rot=(0,0,-1;0.785398rad)
  Radius = 5
FEATURE [Part::Cylinder] Cylinder2367  label="Válec2367"
  Angle = 360
  AttacherType = Attacher::AttachEngine3D
  Height = 100
  Placement = pos=(21.7959,31.1278,0) rot=(0,0,1;2.53073rad)
  Radius = 5
FEATURE [Part::Cylinder] Cylinder2368  label="Válec2368"
  Angle = 360
  AttacherType = Attacher::AttachEngine3D
  Height = 100
  Placement = pos=(-26.8701,26.8701,0) rot=(0,0,1;3.92699rad)
  Radius = 5
FEATURE [Part::Cylinder] Cylinder2369  label="Válec2369"
  Angle = 360
  AttacherType = Attacher::AttachEngine3D
  Height = 100
  Placement = pos=(-1e-15,38,0) rot=(0,0,1;3.14159rad)
  Radius = 5
FEATURE [Part::Cylinder] Cylinder2370  label="Válec2370"
  Angle = 360
  AttacherType = Attacher::AttachEngine3D
  Height = 100
  Placement = pos=(-26.8701,-26.8701,0) rot=(0,0,-1;0.785398rad)
  Radius = 5
FEATURE [Part::Cylinder] Cylinder2371  label="Válec2371"
  Angle = 360
  AttacherType = Attacher::AttachEngine3D
  Height = 100
  Placement = pos=(0,-38,0) rot=(0,0,1;0rad)
  Radius = 5
FEATURE [Part::Cylinder] Cylinder2372  label="Válec2372"
  Angle = 360
  AttacherType = Attacher::AttachEngine3D
  Height = 100
  Placement = pos=(38,3e-15,0) rot=(0,0,1;1.5708rad)
  Radius = 5
FEATURE [Part::Chamfer] Chamfer101
  Base = -> Tube109
  Edges = 1 edges r=1: [Edge3]
FEATURE [Part::Compound] Compound1169
  Links = -> [Cylinder2363,Cylinder2372,Cylinder2367,Cylinder2369,Cylinder2368,Cylinder2359,Cylinder2370,Cylinder2371]
  Placement = pos=(0,0,56) rot=(0,0,1;0rad)
FEATURE [Part::Chamfer] Chamfer104
  Base = -> Tube110
  Edges = 1 edges r=1: [Edge1]
FEATURE [Part::Cut] Cut768
  Base = -> Chamfer104
  Tool = -> Compound1169
FEATURE [Part::Chamfer] Chamfer102
  Base = -> Cut768
  Edges = 5 edges r=0.9: [Edge38,Edge39,Edge41,Edge42,Edge45]
FEATURE [Part::Chamfer] Chamfer105
  Base = -> Chamfer102
  Edges = 4 edges r=0.9: [Edge2,Edge5,Edge8,Edge11]
FEATURE [Part::Chamfer] Chamfer103
  Base = -> Chamfer105
  Edges = 1 edges r=0.9: [Edge14]
  Placement = pos=(0,0,-4) rot=(0,0,1;0rad)
FEATURE [Part::Compound] Compound1170
  Links = -> [Cylinder2362,Cylinder2352,Cylinder2361,Cylinder2356,Cylinder2354,Cylinder2349,Cylinder2360,Cylinder2350]
FEATURE [Part::Compound] Compound1172
  Links = -> [Cylinder2358,Cylinder2364,Cylinder2365,Cylinder2355,Cylinder2357,Cylinder2351,Cylinder2366,Cylinder2353]
  Placement = pos=(0,0,56) rot=(0,0,1;0rad)
FEATURE [Part::Cut] Cut767
  Base = -> Tube108
  Tool = -> Compound1172
FEATURE [Part::Cut] Cut769
  Base = -> Cut767
  Tool = -> Compound1170
FEATURE [Part::Compound] Compound1171  label="Base_inner-cylinder-belt-B-low001"
  Links = -> [Cut769,Chamfer101,Chamfer103]
FEATURE [Part::Mirroring] mirror017  label="Base_inner-cylinder-belt-B-low"
  Base = (0,0,0)
  Normal = (1e-16,-1,0)
  Source = -> Compound1171
FEATURE [Mesh::Feature] Mesh  label="Base_inner-cylinder-belt-B-low (Meshed)"
FEATURE [Part::FeaturePython] Tube111  # WARN: FeaturePython — macro-defined, semantics opaque (R4)
  AttacherType = Attacher::AttachEngine3D
  Height = 7
  InnerRadius = 52
  OuterRadius = 54.4
  Placement = pos=(0,0,-22) rot=(0,0,1;0rad)
FEATURE [Part::FeaturePython] Tube112  # WARN: FeaturePython — macro-defined, semantics opaque (R4)
  AttacherType = Attacher::AttachEngine3D
  Height = 7
  InnerRadius = 52
  OuterRadius = 53.4
  Placement = pos=(0,0,-22) rot=(0,0,1;0rad)
FEATURE [Part::FeaturePython] Tube113  # WARN: FeaturePython — macro-defined, semantics opaque (R4)
  AttacherType = Attacher::AttachEngine3D
  Height = 10
  InnerRadius = 32
  OuterRadius = 57
  Placement = pos=(0,0,42) rot=(0,0,1;0rad)
FEATURE [Part::FeaturePython] Tube114  # WARN: FeaturePython — macro-defined, semantics opaque (R4)
  AttacherType = Attacher::AttachEngine3D
  Height = 3
  InnerRadius = 54
  OuterRadius = 61
  Placement = pos=(0,0,42) rot=(0,0,1;0rad)
FEATURE [Part::Chamfer] Chamfer106
  Base = -> Tube114
  Edges = 1 edges r=1: [Edge1]
FEATURE [Part::Cylinder] Cylinder2373  label="Válec2373"
  Angle = 360
  AttacherType = Attacher::AttachEngine3D
  Height = 7
  Placement = pos=(0,0,45) rot=(0,0,1;0rad)
  Radius = 56
FEATURE [Part::Cylinder] Cylinder2374  label="Válec2374"
  Angle = 360
  AttacherType = Attacher::AttachEngine3D
  Height = 100
  Placement = pos=(26.8701,-26.8701,0) rot=(0,0,1;0.785398rad)
  Radius = 1.5
FEATURE [Part::Box] Box1104  label="Krychle1104"
  AttacherType = Attacher::AttachEngine3D
  Height = 7
  Length = 60
  Placement = pos=(0,0,-22) rot=(0,0,-1;0.349066rad)
  Width = 60
FEATURE [Part::Cylinder] Cylinder2375  label="Válec2375"
  Angle = 360
  AttacherType = Attacher::AttachEngine3D
  Height = 100
  Placement = pos=(-1e-15,38,0) rot=(0,0,1;3.14159rad)
  Radius = 1.5
FEATURE [Part::Cylinder] Cylinder2376  label="Válec2376"
  Angle = 360
  AttacherType = Attacher::AttachEngine3D
  Height = 100
  Placement = pos=(0,-38,0) rot=(0,0,1;0rad)
  Radius = 1.5
FEATURE [Part::Cylinder] Cylinder2377  label="Válec2377"
  Angle = 360
  AttacherType = Attacher::AttachEngine3D
  Height = 100
  Placement = pos=(38,3e-15,0) rot=(0,0,1;1.5708rad)
  Radius = 1.5
FEATURE [Part::Box] Box1105  label="Krychle1105"
  AttacherType = Attacher::AttachEngine3D
  Height = 7
  Length = 1.4
  Placement = pos=(0,0,-22) rot=(0,0,1;0.047124rad)
  Width = 60
FEATURE [Part::Box] Box1106  label="Krychle1106"
  AttacherType = Attacher::AttachEngine3D
  Height = 7
  Length = 1.4
  Placement = pos=(0,0,-22) rot=(0,0,-1;0.034907rad)
  Width = 60
FEATURE [Part::Compound] Compound1174
  Links = -> [Box1106,Box1105]
FEATURE [Part::Box] Box1107  label="Krychle1107"
  AttacherType = Attacher::AttachEngine3D
  Height = 7
  Length = 60
  Placement = pos=(-59.9909,-1.04714,-22) rot=(0,0,1;0.017453rad)
  Width = 60
FEATURE [Part::Box] Box1108  label="Krychle1108"
  AttacherType = Attacher::AttachEngine3D
  Height = 7
  Length = 1.4
  Placement = pos=(0,0,-22) rot=(0,0,1;0.34383rad)
  Width = 60
FEATURE [Part::Cylinder] Cylinder2378  label="Válec2378"
  Angle = 360
  AttacherType = Attacher::AttachEngine3D
  Height = 100
  Placement = pos=(-26.8701,-26.8701,0) rot=(0,0,-1;0.785398rad)
  Radius = 1.5
FEATURE [Part::Cylinder] Cylinder2379  label="Válec2379"
  Angle = 360
  AttacherType = Attacher::AttachEngine3D
  Height = 7
  Placement = pos=(0,0,-22) rot=(0,0,1;0rad)
  Radius = 51
FEATURE [Part::Box] Box1109  label="Krychle1109"
  AttacherType = Attacher::AttachEngine3D
  Height = 7
  Length = 120
  Placement = pos=(-60,-60,-22) rot=(0,0,-1;0rad)
  Width = 60
FEATURE [Part::Cut] Cut772
  Base = -> Tube111
  Tool = -> Box1109
FEATURE [Part::Box] Box1110  label="Krychle1110"
  AttacherType = Attacher::AttachEngine3D
  Height = 7
  Length = 60
  Placement = pos=(0,0,-22) rot=(0,0,-1;0.034907rad)
  Width = 60
FEATURE [Part::Compound] Compound1173
  Links = -> [Box1110,Box1107]
FEATURE [Part::Cut] Cut773
  Base = -> Cut772
  Placement = pos=(0,0,-7) rot=(0,0,1;0rad)
  Tool = -> Compound1173
FEATURE [Part::Box] Box1111  label="Krychle1111"
  AttacherType = Attacher::AttachEngine3D
  Height = 7
  Length = 1.4
  Placement = pos=(0,0,-22) rot=(0,0,-1;0.314159rad)
  Width = 60
FEATURE [Part::Compound] Compound1177
  Links = -> [Box1111,Box1108]
FEATURE [Part::Cut] Cut779
  Base = -> Compound1177
  Placement = pos=(0,0,67) rot=(0,0,1;0.785398rad)
  Tool = -> Cylinder2379
FEATURE [Part::Common] Common002
  Base = -> Cut779
  Tool = -> Cylinder2373
FEATURE [Part::Cylinder] Cylinder2380  label="Válec2380"
  Angle = 360
  AttacherType = Attacher::AttachEngine3D
  Height = 100
  Placement = pos=(-38,-6e-15,0) rot=(0,0,-1;1.5708rad)
  Radius = 1.5
FEATURE [Part::Cylinder] Cylinder2381  label="Válec2381"
  Angle = 360
  AttacherType = Attacher::AttachEngine3D
  Height = 7
  Placement = pos=(0,0,-22) rot=(0,0,1;0rad)
  Radius = 51
FEATURE [Part::Cut] Cut774
  Base = -> Compound1174
  Placement = pos=(0,0,67) rot=(0,0,1;0.785398rad)
  Tool = -> Cylinder2381
FEATURE [Part::Cylinder] Cylinder2382  label="Válec2382"
  Angle = 360
  AttacherType = Attacher::AttachEngine3D
  Height = 100
  Placement = pos=(21.7959,31.1278,0) rot=(0,0,1;2.53073rad)
  Radius = 1.5
FEATURE [Part::Box] Box1112  label="Krychle1112"
  AttacherType = Attacher::AttachEngine3D
  Height = 7
  Length = 120
  Placement = pos=(-60,-60,-22) rot=(0,0,-1;0rad)
  Width = 60
FEATURE [Part::Cut] Cut777
  Base = -> Tube112
  Tool = -> Box1112
FEATURE [Part::Cylinder] Cylinder2383  label="Válec2383"
  Angle = 360
  AttacherType = Attacher::AttachEngine3D
  Height = 100
  Placement = pos=(-26.8701,26.8701,0) rot=(0,0,1;3.92699rad)
  Radius = 1.5
FEATURE [Part::Compound] Compound1175
  Links = -> [Cylinder2374,Cylinder2377,Cylinder2382,Cylinder2375,Cylinder2383,Cylinder2380,Cylinder2378,Cylinder2376]
FEATURE [Part::Cut] Cut775
  Base = -> Tube113
  Tool = -> Compound1175
FEATURE [Part::Cut] Cut778
  Base = -> Cut775
  Tool = -> Cut774
FEATURE [Part::Box] Box1113  label="Krychle1113"
  AttacherType = Attacher::AttachEngine3D
  Height = 7
  Length = 60
  Placement = pos=(-56.3816,-20.5212,-22) rot=(0,0,1;0.349066rad)
  Width = 60
FEATURE [Part::Compound] Compound1176
  Links = -> [Box1104,Box1113]
FEATURE [Part::Cut] Cut776
  Base = -> Cut777
  Placement = pos=(0,0,-7) rot=(0,0,1;0rad)
  Tool = -> Compound1176
FEATURE [Part::Cut] Cut780
  Base = -> Cut776
  Placement = pos=(0,0,74) rot=(0,0,1;0.785398rad)
  Tool = -> Cut773
FEATURE [Part::Cut] Cut770
  Base = -> Cut778
  Tool = -> Cut780
FEATURE [Part::Cut] Cut771
  Base = -> Cut770
  Tool = -> Common002
FEATURE [Part::Compound] Compound1178  label="Base_inner-cylinder-belt-A-001"
  Links = -> [Cut771,Chamfer106]
  Placement = pos=(0,0,1) rot=(0,0,1;0rad)
FEATURE [Part::Mirroring] mirror018  label="Base_inner-cylinder-belt-A"
  Base = (0,0,0)
  Normal = (1e-16,-1,0)
  Source = -> Compound1178
